FCSTD DOCUMENT  (FreeCAD 1.0R39285 (Git))
Label: pillarAssy_16.5m
License: All rights reserved
LicenseURL: https://en.wikipedia.org/wiki/All_rights_reserved
objects: Part::FeaturePython×104, Sketcher::SketchObject×88, Part::Extrusion×72, App::Part×38, Part::Cut×32, Part::Compound×21, Part::Mirroring×20, Part::Revolution×15, Spreadsheet::Sheet×13, Part::Feature×10, Part::Sweep×8, Part::MultiFuse×6, App::FeaturePython×6, Part::Cylinder×5, PartDesign::Pad×3, Part::Chamfer×2, Part::Loft×1, Assembly::JointGroup×1, Assembly::AssemblyObject×1, Part::Part2DObjectPython×1, +4 more types
note: 460 computed .brp shape members not serialized (recipe doc carries the construction recipe); baked Part::Feature solids carry a one-line shape summary decoded from their .brp

FEATURE [Sketcher::SketchObject] Sketch010
  ArcFitTolerance = 1e-06
  FullyConstrained = false
  MakeInternals = false
  Placement = pos=(0,0,0) rot=(1,0,0;1.5708rad)
  expr: Constraints[4] = Spreadsheet011.dia / 2 + 750
  sketch-geometry (3):
    g0: LineSegment StartX=-1399.77 StartY=148.205 StartZ=0 EndX=-2300 EndY=493.773 EndZ=0
    g1: LineSegment StartX=-2300 StartY=493.773 StartZ=0 EndX=-7732.99 EndY=1036.06 EndZ=0
    g2: LineSegment StartX=-7732.99 StartY=1036.06 StartZ=0 EndX=-9000 EndY=1036.06 EndZ=0
  constraints (7):
    c: Coincident(g0,g1)
    c: Coincident(g1,g2)
    c: Horizontal(g2)
    c: DistanceX(g0,g-1) = 2300
    c: DistanceX(g2,g-1) = 9000
    c: Angle(g0,g-1) = 0.366519
    c: Angle(g1,g-1) = 0.0994838
FEATURE [Sketcher::SketchObject] Sketch011
  ArcFitTolerance = 1e-06
  FullyConstrained = false
  MakeInternals = false
  Placement = pos=(-8500,0,0) rot=(0.57735,0.57735,0.57735;2.0944rad)
  sketch-geometry (1):
    g0: Circle CenterX=0.547565 CenterY=1032.56 CenterZ=0 NormalX=0 NormalY=0 NormalZ=1 AngleXU=0 Radius=108
  constraints (1):
    c: Diameter(g0) = 216
FEATURE [Part::Sweep] Sweep
  Frenet = true
  Sections = -> [Sketch011]
  Solid = true
  Spine = -> Sketch010 [Edge3,Edge2,Edge1]
  Transition = 1
FEATURE [Sketcher::SketchObject] Sketch012
  ArcFitTolerance = 1e-06
  AttachmentSupport = -> [Sweep]
  ExternalGeometry = -> [Sweep]
  FullyConstrained = true
  MakeInternals = false
  MapMode = 5
  Placement = pos=(-9000,0,0) rot=(0.57735,-0.57735,-0.57735;2.0944rad)
  sketch-geometry (1):
    g0: Circle CenterX=-0.547565 CenterY=1032.56 CenterZ=0 NormalX=0 NormalY=0 NormalZ=1 AngleXU=0 Radius=102
  constraints (2):
    c: Diameter(g0) = 204
    c: Coincident(g-3,g0)
FEATURE [Part::Sweep] Sweep001
  Frenet = true
  Sections = -> [Sketch012]
  Solid = true
  Spine = -> Sketch010 [Edge3,Edge2,Edge1]
  Transition = 1
FEATURE [Part::Cut] Cut004  label="Cut005"
  Base = -> Sweep
  Tool = -> Sweep001
FEATURE [Sketcher::SketchObject] Sketch003
  ArcFitTolerance = 1e-06
  FullyConstrained = false
  MakeInternals = false
  Placement = pos=(0,0,0) rot=(1,0,0;1.5708rad)
  sketch-geometry (4):
    g0: LineSegment StartX=-1564.35 StartY=456.2 StartZ=0 EndX=-1449.55 EndY=4.38241 EndZ=0
    g1: LineSegment StartX=-1449.55 StartY=4.38241 StartZ=0 EndX=-942.176 EndY=4.38241 EndZ=0
    g2: LineSegment StartX=-942.176 StartY=4.38241 StartZ=0 EndX=-834.777 EndY=456.2 EndZ=0
    g3: LineSegment StartX=-834.777 StartY=456.2 StartZ=0 EndX=-1564.35 EndY=456.2 EndZ=0
  constraints (6):
    c: Coincident(g0,g1)
    c: Horizontal(g1)
    c: Coincident(g1,g2)
    c: Coincident(g2,g3)
    c: Coincident(g3,g0)
    c: Horizontal(g3)
FEATURE [Part::Revolution] Revolve001
  Angle = 360
  Axis = (0,0,1)
  Base = (0,0,0)
  FaceMakerClass = Part::FaceMakerBullseye
  Solid = true
  Source = -> Sketch003
  Symmetric = false
FEATURE [Part::Cut] Cut005  label="Cut006"
  Base = -> Cut004
  Tool = -> Revolve001
FEATURE [Part::FeaturePython] Flange001  # WARN: FeaturePython — macro-defined, semantics opaque (R4)
  Placement = pos=(-9000,0.547565,1032.56) rot=(0,1,0;4.71239rad)
  dia = 4
  fittings = 00_Flange
  material = 0
  standard = 1
  expr: .Placement.Base.x = -Spreadsheet011.dia / 2 - 750
FEATURE [App::Part] Part037  label="sludgePipe"
  Group = -> [Flange001,Sketch012,Sketch003,Sketch011,Sketch010,Revolve001,Cut004,Sweep,Sweep001,Cut005]
  Origin = -> Origin061
  mass = 244.943
FEATURE [Sketcher::SketchObject] Sketch015
  ArcFitTolerance = 0
  FullyConstrained = true
  MakeInternals = false
  Placement = pos=(0,0,0) rot=(1,0,0;1.5708rad)
  expr: Constraints[11] = Spreadsheet001.dia / 2 - 460
  sketch-geometry (4):
    g0: LineSegment StartX=7785 StartY=0 StartZ=0 EndX=7790 EndY=0 EndZ=0
    g1: LineSegment StartX=7790 StartY=0 StartZ=0 EndX=7790 EndY=250 EndZ=0
    g2: LineSegment StartX=7790 StartY=250 StartZ=0 EndX=7785 EndY=250 EndZ=0
    g3: LineSegment StartX=7785 StartY=250 StartZ=0 EndX=7785 EndY=0 EndZ=0
  constraints (12):
    c: Coincident(g0,g1)
    c: Coincident(g1,g2)
    c: Coincident(g2,g3)
    c: Coincident(g3,g0)
    c: Horizontal(g0)
    c: Horizontal(g2)
    c: Vertical(g1)
    c: Vertical(g3)
    c: PointOnObject(g0,g-1)
    c: Distance(g2) = 5
    c: DistanceY(g1,g1) = 250
    c: DistanceX(g-1,g0) = 7790
FEATURE [Part::Revolution] Revolve006
  Angle = 360
  Axis = (0,0,1)
  Base = (0,0,0)
  FaceMakerClass = Part::FaceMakerBullseye
  Solid = true
  Source = -> Sketch015
  Symmetric = false
FEATURE [Sketcher::SketchObject] Sketch016
  ArcFitTolerance = 0
  FullyConstrained = true
  MakeInternals = false
  Placement = pos=(0,0,0) rot=(1,0,0;1.5708rad)
  sketch-geometry (3):
    g0: LineSegment StartX=-70 StartY=250 StartZ=0 EndX=70 EndY=250 EndZ=0
    g1: LineSegment StartX=70 StartY=250 StartZ=0 EndX=0 EndY=180 EndZ=0
    g2: LineSegment StartX=0 StartY=180 StartZ=0 EndX=-70 EndY=250 EndZ=0
  constraints (9):
    c: Horizontal(g0)
    c: Coincident(g0,g1)
    c: PointOnObject(g1,g-2)
    c: Coincident(g1,g2)
    c: Coincident(g2,g0)
    c: Angle(g1,g2) = 1.5708
    c: PointOnObject(g0,g-3)
    c: DistanceY(g1,g0) = 70
    c: Angle(g2,g-2) = 2.35619
FEATURE [Part::Extrusion] Extrude010
  Base = -> Sketch016
  Dir = (0,-1,2e-16)
  DirMode = 2
  FaceMakerClass = Part::FaceMakerBullseye
  FaceMakerMode = 3
  LengthFwd = 10000
  LengthRev = 0
  Solid = true
  Symmetric = false
FEATURE [Part::FeaturePython] Array006  # Draft array (typed FeaturePython)
  AlwaysSyncPlacement = false
  Angle = 360
  ArrayType = 1
  Axis = (0,0,1)
  Base = -> Extrude010
  Center = (0,0,0)
  Count = 300
  ExpandArray = false
  Fuse = false
  IntervalAxis = (0,0,0)
  IntervalX = (50,0,0)
  IntervalY = (0,50,0)
  IntervalZ = (0,0,50)
  NumberCircles = 3
  NumberPolar = 300
  NumberX = 2
  NumberY = 2
  NumberZ = 1
  PlacementList = 300 placements: [(0,0,0),(0,0,0),(0,0,0),(0,0,0),(0,0,0),(0,0,0),(0,0,0),(0,0,0),(0,0,0),(0,0,0),(0,0,0),(0,0,0),(0,0,0),(0,0,0),(0,0,0),(0,0,0),(0,0,0),(0,0,0),(0,0,0),(0,0,0),(0,0,0),(0,0,0),(0,0,0),(0,0,0),(0,0,0),(0,0,0),(0,0,0),(0,0,0),(0,0,0),(0,0,0),(0,0,0),(0,0,0),(0,0,0),(0,0,0),(0,0,0),(0,0,0),(0,0,0),(0,0,0),(0,0,0),(0,0,0),(0,0,0),(0,0,0),(0,0,0),(0,0,0),(0,0,0),(0,0,0),(0,0,0),(0,0,0),(0,0,0),(0,0,0),+250 more]
  RadialDistance = 50
  Symmetry = 1
  TangentialDistance = 25
  expr: NumberPolar = Spreadsheet001.dia / 55
FEATURE [Part::Cut] Cut007  label="weir"
  Base = -> Revolve006
  Placement = pos=(0,0,4730.4) rot=(0,0,1;0rad)
  Tool = -> Array006
FEATURE [Sketcher::SketchObject] Sketch017
  ArcFitTolerance = 0
  FullyConstrained = true
  MakeInternals = false
  Placement = pos=(0,0,0) rot=(1,0,0;1.5708rad)
  expr: .Constraints.h0 = Spreadsheet001.h0
  expr: Constraints[11] = Spreadsheet001.dia / 2 - (450 + 300)
  sketch-geometry (4):
    g0: LineSegment StartX=7495 StartY=80 StartZ=0 EndX=7500 EndY=80 EndZ=0
    g1: LineSegment StartX=7500 StartY=80 StartZ=0 EndX=7500 EndY=380 EndZ=0
    g2: LineSegment StartX=7500 StartY=380 StartZ=0 EndX=7495 EndY=380 EndZ=0
    g3: LineSegment StartX=7495 StartY=380 StartZ=0 EndX=7495 EndY=80 EndZ=0
  constraints (12):
    c: Coincident(g0,g1)
    c: Coincident(g1,g2)
    c: Coincident(g2,g3)
    c: Coincident(g3,g0)
    c: Horizontal(g0)
    c: Horizontal(g2)
    c: Vertical(g1)
    c: Vertical(g3)
    c: DistanceX(g2,g2) = 5
    c: DistanceY(g1,g1) = 300  'h0'
    c: DistanceY(g-3,g1) = 130
    c: Distance(g1,g-2) = 7500
FEATURE [Part::Revolution] Revolve007
  Angle = 360
  Axis = (0,0,1)
  Base = (0,0,0)
  FaceMakerClass = Part::FaceMakerBullseye
  Solid = true
  Source = -> Sketch017
  Symmetric = false
FEATURE [Part::FeaturePython] AngleSteel  # WARN: FeaturePython — macro-defined, semantics opaque (R4)
  A = 50
  B = 50
  L = 1000
  Placement = pos=(7500,0,474) rot=(0,1,0;1.5708rad)
  Solid = false
  g0 = 7.85
  mass = 0
  size = 7
  standard = SS_Equal
  t = 6
  expr: .Placement.Base.x = Spreadsheet001.dia / 2 - 750
FEATURE [Part::Revolution] Revolve008  label="Revolve002"
  Angle = 360
  Axis = (0,0,1)
  Base = (0,0,0)
  FaceMakerClass = Part::FaceMakerBullseye
  Placement = pos=(0,0,-94) rot=(0,0,1;0rad)
  Solid = false
  Source = -> AngleSteel
  Symmetric = false
FEATURE [Sketcher::SketchObject] Sketch018
  ArcFitTolerance = 0
  FullyConstrained = true
  MakeInternals = false
  Placement = pos=(0,0,0) rot=(1,0,0;1.5708rad)
  expr: Constraints[10] = Spreadsheet001.dia / 2 - (460 + 290)
  sketch-geometry (4):
    g0: LineSegment StartX=7500 StartY=80 StartZ=0 EndX=7790 EndY=-163.339 EndZ=0
    g1: LineSegment StartX=7790 StartY=-163.339 StartZ=0 EndX=7790 EndY=-6.69002 EndZ=0
    g2: LineSegment StartX=7790 StartY=-6.69002 StartZ=0 EndX=7500 EndY=236.649 EndZ=0
    g3: LineSegment StartX=7500 StartY=236.649 StartZ=0 EndX=7500 EndY=80 EndZ=0
  constraints (12):
    c: Coincident(g0,g1)
    c: Vertical(g1)
    c: Coincident(g1,g2)
    c: Coincident(g2,g3)
    c: Coincident(g3,g0)
    c: Vertical(g3)
    c: Parallel(g2,g0)
    c: DistanceX(g0,g0) = 290
    c: Distance(g1,g0) = 120
    c: Angle(g0,g3) = 2.26893
    c: Distance(g0,g-2) = 7500
    c: Distance(g0,g-1) = 80
FEATURE [Part::Extrusion] Extrude011
  Base = -> Sketch018
  Dir = (0,-1,2e-16)
  DirMode = 2
  FaceMakerClass = Part::FaceMakerBullseye
  FaceMakerMode = 3
  LengthFwd = 6
  LengthRev = 0
  Solid = true
  Symmetric = true
FEATURE [Spreadsheet::Sheet] Spreadsheet001  label="Spreadsheet"
  cells = A3='tankDia dia; B3(dia)=16500; A4='waterWay width; B4(W0)=450; A5='nonber of support; B5(n)=12; A6='buffleHight  h0; B6(h0)=300
FEATURE [Part::FeaturePython] AngleSteel001  # WARN: FeaturePython — macro-defined, semantics opaque (R4)
  A = 50
  B = 50
  L = 140
  Placement = pos=(7765,28,-150) rot=(0,0,1;3.14159rad)
  Solid = true
  g0 = 7.85
  mass = 0.620249
  size = 7
  standard = SS_Equal
  t = 6
  expr: .Placement.Base.x = Spreadsheet001.dia / 2 - 485
FEATURE [Part::Mirroring] Mirror  label="AngleSteel001 (mirrored)"
  Base = (4800,0,0)
  Normal = (0,-1,0)
  Source = -> AngleSteel001
FEATURE [Part::Compound] Compound041  label="support"
  Links = -> [AngleSteel001,Mirror,Extrude011]
FEATURE [Part::FeaturePython] Array001  # Draft array (typed FeaturePython)
  AlwaysSyncPlacement = false
  Angle = 360
  ArrayType = 1
  Axis = (0,0,1)
  Base = -> Compound041
  Center = (0,0,0)
  Count = 12
  ExpandArray = false
  Fuse = false
  IntervalAxis = (0,0,0)
  IntervalX = (50,0,0)
  IntervalY = (0,50,0)
  IntervalZ = (0,0,50)
  NumberCircles = 3
  NumberPolar = 12
  NumberX = 2
  NumberY = 2
  NumberZ = 1
  PlacementList = 12 placements: [(0,0,0),(0,0,0),(0,0,0),(0,0,0),(0,0,0),(0,0,0),(0,0,0),(0,0,0),(0,0,0),(0,0,0),(0,0,0),(0,0,0)]
  RadialDistance = 50
  ScaleList = (12) [(1,1,1),(1,1,1),(1,1,1),(1,1,1),(1,1,1),(1,1,1),(1,1,1),(1,1,1),(1,1,1),(1,1,1),(1,1,1),(1,1,1)]
  Symmetry = 1
  TangentialDistance = 25
  expr: NumberPolar = Spreadsheet001.n
FEATURE [Part::Compound] Compound042  label="buffle001"
  Links = -> [Revolve007,Revolve008]
  Placement = pos=(0,0,-20) rot=(0,0,1;0rad)
FEATURE [App::Part] Part038  label="buffle"
  Group = -> [Spreadsheet001,Revolve007,Sketch017,Sketch018,Sketch016,Extrude011,Extrude010,AngleSteel,Revolve008,AngleSteel001,Mirror,Compound041,Array001,Compound042]
  Origin = -> Origin062
  Placement = pos=(0,0,4689) rot=(0,0,1;0rad)
  mass = 804.437
FEATURE [Sketcher::SketchObject] Sketch019
  ArcFitTolerance = 0
  FullyConstrained = true
  MakeInternals = false
  Placement = pos=(0,0,0) rot=(1,0,0;1.5708rad)
  expr: .Constraints.r1 = Spreadsheet002.dia / 2 + 144
  expr: Constraints[20] = Spreadsheet002.dia / 2
  expr: Constraints[21] = .Constraints.r1
  expr: Constraints[22] = Spreadsheet002.l2
  sketch-geometry (8):
    g0: LineSegment StartX=569 StartY=0 StartZ=0 EndX=569 EndY=30 EndZ=0
    g1: LineSegment StartX=569 StartY=30 StartZ=0 EndX=425 EndY=30 EndZ=0
    g2: LineSegment StartX=415 StartY=0 StartZ=0 EndX=415 EndY=3101 EndZ=0
    g3: LineSegment StartX=415 StartY=3101 StartZ=0 EndX=569 EndY=3101 EndZ=0
    g4: LineSegment StartX=569 StartY=3101 StartZ=0 EndX=569 EndY=3071 EndZ=0
    g5: LineSegment StartX=569 StartY=3071 StartZ=0 EndX=425 EndY=3071 EndZ=0
    g6: LineSegment StartX=425 StartY=3071 StartZ=0 EndX=425 EndY=30 EndZ=0
    g7: LineSegment StartX=569 StartY=0 StartZ=0 EndX=415 EndY=0 EndZ=0
  constraints (24):
    c: Vertical(g0)
    c: Coincident(g0,g1)
    c: Horizontal(g1)
    c: Vertical(g2)
    c: Coincident(g2,g3)
    c: Horizontal(g3)
    c: Coincident(g3,g4)
    c: Vertical(g4)
    c: Coincident(g4,g5)
    c: Horizontal(g5)
    c: Coincident(g5,g6)
    c: Vertical(g6)
    c: Coincident(g0,g7)
    c: Horizontal(g7)
    c: Coincident(g1,g6)
    c: DistanceX(g-1,g0) = 569  'r1'
    c: DistanceY(g0,g0) = 30
    c: PointOnObject(g0,g-1)
    c: Coincident(g2,g7)
    c: DistanceX(g2,g1) = 10
    c: DistanceX(g-1,g1) = 425
    c: DistanceX(g-2,g3) = 569
    c: DistanceY(g-1,g3) = 3101
    c: DistanceY(g4,g4) = 30
FEATURE [Part::Revolution] Revolve009  label="bottom"
  Angle = 360
  Axis = (0,0,1)
  Base = (0,0,0)
  FaceMakerClass = Part::FaceMakerBullseye
  Solid = true
  Source = -> Sketch019
  Symmetric = false
FEATURE [Sketcher::SketchObject] Sketch020
  ArcFitTolerance = 0
  FullyConstrained = true
  MakeInternals = false
  Placement = pos=(0,0,0) rot=(1,0,0;1.5708rad)
  sketch-geometry (4):
    g0: LineSegment StartX=315 StartY=0 StartZ=0 EndX=415 EndY=0 EndZ=0
    g1: LineSegment StartX=415 StartY=0 StartZ=0 EndX=415 EndY=2950 EndZ=0
    g2: LineSegment StartX=415 StartY=2950 StartZ=0 EndX=315 EndY=2950 EndZ=0
    g3: LineSegment StartX=315 StartY=2950 StartZ=0 EndX=315 EndY=0 EndZ=0
  constraints (11):
    c: Coincident(g0,g1)
    c: Coincident(g1,g2)
    c: Coincident(g2,g3)
    c: Coincident(g3,g0)
    c: Horizontal(g0)
    c: Horizontal(g2)
    c: Vertical(g1)
    c: Vertical(g3)
    c: Distance(g0) = 100
    c: Coincident(g0,g-3)
    c: PointOnObject(g2,g-4)
FEATURE [Part::Revolution] Revolve010  label="covering"
  Angle = 360
  Axis = (0,0,1)
  Base = (0,0,0)
  FaceMakerClass = Part::FaceMakerBullseye
  Placement = pos=(0,0,936.6) rot=(0,0,1;0rad)
  Solid = true
  Source = -> Sketch020
  Symmetric = false
  mass = 1420.74
FEATURE [Sketcher::SketchObject] Sketch021
  ArcFitTolerance = 0
  FullyConstrained = true
  MakeInternals = false
  Placement = pos=(0,0,0) rot=(1,0,0;1.5708rad)
  expr: Constraints[8] = Spreadsheet002.t0
  expr: Constraints[9] = Spreadsheet002.l2
  sketch-geometry (4):
    g0: LineSegment StartX=415 StartY=3101 StartZ=0 EndX=569 EndY=3101 EndZ=0
    g1: LineSegment StartX=569 StartY=3101 StartZ=0 EndX=569 EndY=3106 EndZ=0
    g2: LineSegment StartX=569 StartY=3106 StartZ=0 EndX=415 EndY=3106 EndZ=0
    g3: LineSegment StartX=415 StartY=3106 StartZ=0 EndX=415 EndY=3101 EndZ=0
  constraints (12):
    c: Coincident(g0,g1)
    c: Coincident(g1,g2)
    c: Coincident(g2,g3)
    c: Coincident(g3,g0)
    c: Horizontal(g0)
    c: Horizontal(g2)
    c: Vertical(g1)
    c: Vertical(g3)
    c: DistanceY(g1,g1) = 5
    c: DistanceY(g-1,g0) = 3101
    c: PointOnObject(g0,g-3)
    c: PointOnObject(g-4,g1)
FEATURE [Part::Revolution] Revolve002  label="gasket"
  Angle = 360
  Axis = (0,0,1)
  Base = (0,0,0)
  FaceMakerClass = Part::FaceMakerBullseye
  Placement = pos=(0,0,1.3656e-08) rot=(0,0,1;0rad)
  Solid = true
  Source = -> Sketch021
  Symmetric = false
FEATURE [Sketcher::SketchObject] Sketch022
  ArcFitTolerance = 0
  FullyConstrained = true
  MakeInternals = false
  Placement = pos=(0,0,0) rot=(1,0,0;1.5708rad)
  expr: Constraints[12] = Spreadsheet002.l1
  sketch-geometry (6):
    g0: LineSegment StartX=569 StartY=2985 StartZ=0 EndX=425 EndY=2985 EndZ=0
    g1: LineSegment StartX=425 StartY=2985 StartZ=0 EndX=425 EndY=4405 EndZ=0
    g2: LineSegment StartX=415 StartY=4405 StartZ=0 EndX=415 EndY=2955 EndZ=0
    g3: LineSegment StartX=415 StartY=2955 StartZ=0 EndX=569 EndY=2955 EndZ=0
    g4: LineSegment StartX=569 StartY=2955 StartZ=0 EndX=569 EndY=2985 EndZ=0
    g5: LineSegment StartX=425 StartY=4405 StartZ=0 EndX=415 EndY=4405 EndZ=0
  constraints (17):
    c: Coincident(g0,g1)
    c: Vertical(g1)
    c: Vertical(g2)
    c: Coincident(g2,g3)
    c: Horizontal(g3)
    c: Coincident(g3,g4)
    c: Coincident(g4,g0)
    c: Vertical(g4)
    c: DistanceY(g4,g4) = 30
    c: Coincident(g3,g-3)
    c: DistanceX(g2,g0) = 10
    c: PointOnObject(g2,g-4)
    c: DistanceY(g3,g1) = 1450
    c: Coincident(g5,g1)
    c: Horizontal(g5)
    c: Coincident(g2,g5)
    c: Horizontal(g0)
FEATURE [Part::Revolution] Revolve003  label="top"
  Angle = 360
  Axis = (0,0,1)
  Base = (0,0,0)
  FaceMakerClass = Part::FaceMakerBullseye
  Solid = true
  Source = -> Sketch022
  Symmetric = false
FEATURE [Sketcher::SketchObject] Sketch023
  ArcFitTolerance = 0
  FullyConstrained = true
  MakeInternals = false
  Placement = pos=(0,0,0) rot=(1,0,0;1.5708rad)
  sketch-geometry (12):
    g0: LineSegment StartX=200 StartY=-1.8e-15 StartZ=0 EndX=406 EndY=-1.8e-15 EndZ=0
    g1: LineSegment StartX=406 StartY=-1.8e-15 StartZ=0 EndX=406 EndY=25 EndZ=0
    g2: LineSegment StartX=406 StartY=25 StartZ=0 EndX=200 EndY=25 EndZ=0
    g3: LineSegment StartX=0 StartY=175 StartZ=0 EndX=350 EndY=175 EndZ=0
    g4: LineSegment StartX=350 StartY=175 StartZ=0 EndX=350 EndY=200 EndZ=0
    g5: LineSegment StartX=350 StartY=200 StartZ=0 EndX=0 EndY=200 EndZ=0
    g6: LineSegment StartX=0 StartY=200 StartZ=0 EndX=0 EndY=175 EndZ=0
    g7: LineSegment StartX=242 StartY=25 StartZ=0 EndX=254 EndY=25 EndZ=0
    g8: LineSegment StartX=254 StartY=25 StartZ=0 EndX=254 EndY=175 EndZ=0
    g9: LineSegment StartX=254 StartY=175 StartZ=0 EndX=242 EndY=175 EndZ=0
    g10: LineSegment StartX=242 StartY=175 StartZ=0 EndX=242 EndY=25 EndZ=0
    g11: LineSegment StartX=200 StartY=25 StartZ=0 EndX=200 EndY=-3.6e-15 EndZ=0
  constraints (36):
    c: Coincident(g0,g1)
    c: Coincident(g1,g2)
    c: Horizontal(g0)
    c: Horizontal(g2)
    c: Vertical(g1)
    c: DistanceY(g1,g1) = 25
    c: DistanceX(g-1,g0) = 406
    c: Coincident(g3,g4)
    c: Coincident(g4,g5)
    c: Coincident(g5,g6)
    c: Coincident(g6,g3)
    c: Horizontal(g3)
    c: Horizontal(g5)
    c: Vertical(g4)
    c: Vertical(g6)
    c: PointOnObject(g3,g-2)
    c: DistanceY(g4,g4) = 25
    c: DistanceX(g5,g5) = 350
    c: DistanceY(g0,g4) = 200
    c: Coincident(g7,g8)
    c: Coincident(g8,g9)
    c: Coincident(g9,g10)
    c: Coincident(g10,g7)
    c: Horizontal(g7)
    c: Horizontal(g9)
    c: Vertical(g8)
    c: Vertical(g10)
    c: PointOnObject(g7,g2)
    c: PointOnObject(g8,g3)
    c: DistanceX(g9,g8) = 12
    c: Vertical(g11)
    c: Coincident(g2,g11)
    c: Coincident(g0,g11)
    c: DistanceX(g-1,g0) = 200
    c: DistanceX(g-2,g7) = 254
    c: PointOnObject(g0,g-1)
FEATURE [Part::Revolution] Revolve004
  Angle = 360
  Axis = (0,0,1)
  Base = (0,0,0)
  FaceMakerClass = Part::FaceMakerBullseye
  Solid = true
  Source = -> Sketch023
  Symmetric = false
FEATURE [Sketcher::SketchObject] Sketch024
  ArcFitTolerance = 0
  AttachmentSupport = -> [Revolve004]
  FullyConstrained = true
  MakeInternals = false
  MapMode = 5
  Placement = pos=(0,0,200) rot=(0,0,1;0rad)
  sketch-geometry (1):
    g0: Circle CenterX=0 CenterY=0 CenterZ=0 NormalX=0 NormalY=0 NormalZ=1 AngleXU=0 Radius=25
  constraints (2):
    c: Coincident(g0,g-1)
    c: Radius(g0) = 25
FEATURE [Part::Extrusion] Extrude012
  Base = -> Sketch024
  Dir = (0,0,1)
  DirMode = 2
  FaceMakerClass = Part::FaceMakerBullseye
  FaceMakerMode = 3
  LengthFwd = 25
  LengthRev = 0
  Reversed = true
  Solid = true
  Symmetric = false
FEATURE [Part::Cut] Cut008
  Base = -> Revolve004
  Tool = -> Extrude012
FEATURE [Sketcher::SketchObject] Sketch025
  ArcFitTolerance = 0
  AttachmentSupport = -> [Cut008]
  FullyConstrained = true
  MakeInternals = false
  MapMode = 5
  Placement = pos=(0,0,200) rot=(0,0,1;0rad)
  sketch-geometry (2):
    g0: Circle CenterX=277.164 CenterY=114.805 CenterZ=0 NormalX=0 NormalY=0 NormalZ=1 AngleXU=0 Radius=14
    g1: LineSegment [constr] StartX=0 StartY=0 StartZ=0 EndX=277.164 EndY=114.805 EndZ=0
  constraints (5):
    c: Coincident(g1,g-1)
    c: Coincident(g1,g0)
    c: Angle(g-1,g1) = 0.392699
    c: Distance(g1) = 300
    c: Radius(g0) = 14
FEATURE [Part::Extrusion] Extrude003
  Base = -> Sketch025
  Dir = (0,0,1)
  DirMode = 2
  FaceMakerClass = Part::FaceMakerBullseye
  FaceMakerMode = 3
  LengthFwd = 25
  LengthRev = 0
  Reversed = true
  Solid = true
  Symmetric = false
FEATURE [Part::FeaturePython] Array002  # Draft array (typed FeaturePython)
  AlwaysSyncPlacement = false
  Angle = 360
  ArrayType = 1
  Axis = (0,0,1)
  Base = -> Extrude003
  Center = (0,0,0)
  Count = 8
  ExpandArray = false
  Fuse = false
  IntervalAxis = (0,0,0)
  IntervalX = (50,0,0)
  IntervalY = (0,50,0)
  IntervalZ = (0,0,50)
  NumberCircles = 3
  NumberPolar = 8
  NumberX = 2
  NumberY = 2
  NumberZ = 1
  PlacementList = 8 placements: [(0,0,0),(0,0,0),(0,0,0),(0,0,0),(0,0,0),(0,0,0),(0,0,0),(0,0,0)]
  RadialDistance = 50
  ScaleList = (8) [(1,1,1),(1,1,1),(1,1,1),(1,1,1),(1,1,1),(1,1,1),(1,1,1),(1,1,1)]
  Symmetry = 1
  TangentialDistance = 25
FEATURE [Sketcher::SketchObject] Sketch026
  ArcFitTolerance = 0
  AttachmentSupport = -> [Revolve009]
  FullyConstrained = true
  MakeInternals = false
  MapMode = 5
  Placement = pos=(0,0,0) rot=(1,0,0;3.14159rad)
  sketch-geometry (2):
    g0: LineSegment [constr] StartX=0 StartY=0 StartZ=0 EndX=461.94 EndY=191.342 EndZ=0
    g1: Circle CenterX=461.94 CenterY=191.342 CenterZ=0 NormalX=0 NormalY=0 NormalZ=1 AngleXU=0 Radius=17.5
  constraints (5):
    c: Coincident(g0,g-1)
    c: Coincident(g1,g0)
    c: Radius(g1) = 17.5
    c: Distance(g0) = 500
    c: Angle(g-1,g0) = 0.392699
FEATURE [Part::Extrusion] Extrude013
  Base = -> Sketch026
  Dir = (0,0,-1)
  DirMode = 2
  FaceMakerClass = Part::FaceMakerBullseye
  FaceMakerMode = 3
  LengthFwd = 3000
  LengthRev = 0
  Reversed = true
  Solid = true
  Symmetric = false
FEATURE [Part::FeaturePython] Array003  # Draft array (typed FeaturePython)
  AlwaysSyncPlacement = false
  Angle = 360
  ArrayType = 1
  Axis = (0,0,1)
  Base = -> Extrude013
  Center = (0,0,0)
  Count = 8
  ExpandArray = false
  Fuse = false
  IntervalAxis = (0,0,0)
  IntervalX = (50,0,0)
  IntervalY = (0,50,0)
  IntervalZ = (0,0,50)
  NumberCircles = 3
  NumberPolar = 8
  NumberX = 2
  NumberY = 2
  NumberZ = 1
  PlacementList = 8 placements: [(0,0,0),(0,0,0),(0,0,0),(0,0,0),(0,0,0),(0,0,0),(0,0,0),(0,0,0)]
  RadialDistance = 50
  ScaleList = (8) [(1,1,1),(1,1,1),(1,1,1),(1,1,1),(1,1,1),(1,1,1),(1,1,1),(1,1,1)]
  Symmetry = 1
  TangentialDistance = 25
FEATURE [Part::Cut] Cut009  label="bottom001"
  Base = -> Revolve009
  Tool = -> Array003
FEATURE [Sketcher::SketchObject] Sketch027
  ArcFitTolerance = 0
  ExternalGeometry = -> [Revolve003]
  FullyConstrained = true
  MakeInternals = false
  Placement = pos=(0,0,0) rot=(1,0,0;1.5708rad)
  expr: Constraints[19] = Spreadsheet002.h0
  sketch-geometry (8):
    g0: LineSegment StartX=-45 StartY=3855 StartZ=0 EndX=45 EndY=3855 EndZ=0
    g1: LineSegment StartX=75 StartY=3885 StartZ=0 EndX=75 EndY=4125 EndZ=0
    g2: LineSegment StartX=45 StartY=4155 StartZ=0 EndX=-45 EndY=4155 EndZ=0
    g3: LineSegment StartX=-75 StartY=4125 StartZ=0 EndX=-75 EndY=3885 EndZ=0
    g4: ArcOfCircle CenterX=45 CenterY=4125 CenterZ=0 NormalX=0 NormalY=0 NormalZ=1 AngleXU=0 Radius=30 StartAngle=-1.07e-14 EndAngle=1.5708
    g5: ArcOfCircle CenterX=-45 CenterY=4125 CenterZ=0 NormalX=0 NormalY=0 NormalZ=1 AngleXU=0 Radius=30 StartAngle=1.5708 EndAngle=3.14159
    g6: ArcOfCircle CenterX=-45 CenterY=3885 CenterZ=0 NormalX=0 NormalY=0 NormalZ=1 AngleXU=0 Radius=30 StartAngle=3.14159 EndAngle=4.71239
    g7: ArcOfCircle CenterX=45 CenterY=3885 CenterZ=0 NormalX=0 NormalY=0 NormalZ=1 AngleXU=0 Radius=30 StartAngle=4.71239 EndAngle=6.28319
  constraints (20):
    c: Horizontal(g0)
    c: Horizontal(g2)
    c: Vertical(g1)
    c: Vertical(g3)
    c: Tangent(g1,g4) = -1.5708
    c: Tangent(g2,g4) = -1.5708
    c: Tangent(g2,g5) = -1.5708
    c: Tangent(g3,g5) = -1.5708
    c: Tangent(g0,g6) = -1.5708
    c: Tangent(g3,g6) = -1.5708
    c: Tangent(g0,g7) = -1.5708
    c: Tangent(g1,g7) = -1.5708
    c: DistanceY(g0,g2) = 300
    c: DistanceX(g3,g1) = 150
    c: DistanceX(g-1,g1) = 75
    c: Radius(g4) = 30
    c: Equal(g4,g5)
    c: Equal(g5,g6)
    c: Equal(g6,g7)
    c: DistanceY(g2,g-3) = 250
FEATURE [Part::Extrusion] Extrude014
  Base = -> Sketch027
  Dir = (0,-1,2e-16)
  DirMode = 2
  FaceMakerClass = Part::FaceMakerBullseye
  FaceMakerMode = 3
  LengthFwd = 500
  LengthRev = 0
  Solid = true
  Symmetric = false
FEATURE [Part::FeaturePython] Array007  # Draft array (typed FeaturePython)
  AlwaysSyncPlacement = false
  Angle = 360
  ArrayType = 1
  Axis = (0,0,1)
  Base = -> Extrude014
  Center = (0,0,0)
  Count = 4
  ExpandArray = false
  Fuse = false
  IntervalAxis = (0,0,0)
  IntervalX = (50,0,0)
  IntervalY = (0,50,0)
  IntervalZ = (0,0,50)
  NumberCircles = 3
  NumberPolar = 4
  NumberX = 2
  NumberY = 2
  NumberZ = 1
  PlacementList = 4 placements: [(0,0,0),(0,0,0),(0,0,0),(0,0,0)]
  RadialDistance = 50
  ScaleList = (4) [(1,1,1),(1,1,1),(1,1,1),(1,1,1)]
  Symmetry = 1
  TangentialDistance = 25
FEATURE [Part::Cut] Cut010  label="Cut009"
  Base = -> Revolve003
  Tool = -> Array007
FEATURE [Sketcher::SketchObject] Sketch028
  ArcFitTolerance = 0
  AttachmentSupport = -> [Cut010]
  FullyConstrained = true
  MakeInternals = false
  MapMode = 5
  Placement = pos=(0,0,2955) rot=(1,0,0;3.14159rad)
  sketch-geometry (2):
    g0: LineSegment [constr] StartX=0 StartY=0 StartZ=0 EndX=461.94 EndY=191.342 EndZ=0
    g1: Circle CenterX=461.94 CenterY=191.342 CenterZ=0 NormalX=0 NormalY=0 NormalZ=1 AngleXU=0 Radius=17.5
  constraints (5):
    c: Coincident(g0,g-1)
    c: Distance(g0) = 500
    c: Coincident(g1,g0)
    c: Radius(g1) = 17.5
    c: Angle(g-1,g0) = 0.392699
FEATURE [Part::Extrusion] Extrude015
  Base = -> Sketch028
  Dir = (0,0,-1)
  DirMode = 2
  FaceMakerClass = Part::FaceMakerBullseye
  FaceMakerMode = 3
  LengthFwd = 30
  LengthRev = 0
  Reversed = true
  Solid = true
  Symmetric = false
FEATURE [Part::Cut] Cut011
  Base = -> Cut010
  Tool = -> Extrude015
FEATURE [Part::FeaturePython] Array004  # Draft array (typed FeaturePython)
  AlwaysSyncPlacement = false
  Angle = 360
  ArrayType = 1
  Axis = (0,0,1)
  Base = -> Extrude015
  Center = (0,0,0)
  Count = 8
  ExpandArray = false
  Fuse = false
  IntervalAxis = (0,0,0)
  IntervalX = (50,0,0)
  IntervalY = (0,50,0)
  IntervalZ = (0,0,50)
  NumberCircles = 3
  NumberPolar = 8
  NumberX = 2
  NumberY = 2
  NumberZ = 1
  PlacementList = 8 placements: [(0,0,0),(0,0,0),(0,0,0),(0,0,0),(0,0,0),(0,0,0),(0,0,0),(0,0,0)]
  RadialDistance = 50
  ScaleList = (8) [(1,1,1),(1,1,1),(1,1,1),(1,1,1),(1,1,1),(1,1,1),(1,1,1),(1,1,1)]
  Symmetry = 1
  TangentialDistance = 25
FEATURE [Part::Cut] Cut012  label="top001"
  Base = -> Cut011
  Placement = pos=(0,0,151) rot=(0,0,1;0rad)
  Tool = -> Array004
  expr: .Placement.Base.z = <<Spreadsheet_centerPost>>.l2 - 2950
FEATURE [Spreadsheet::Sheet] Spreadsheet002  label="Spreadsheet_centerPost"
  cells = A2='top  l1; B2(l1)=1450; A3='bottom  l2; B3(l2)=3101; A4='base l3; B4(l3)=200; A5='gasket  t0; B5(t0)=5; A6='postDia; B6(dia)=850; A7='weirHighr h0; B7(h0)=250
FEATURE [Sketcher::SketchObject] Sketch029
  ArcFitTolerance = 1e-06
  AttachmentSupport = -> [Cut008]
  ExternalGeometry = -> [Cut008]
  FullyConstrained = false
  MakeInternals = false
  MapMode = 5
  Placement = pos=(0,0,25) rot=(0,0,1;0rad)
  sketch-geometry (4):
    g0: LineSegment StartX=-10 StartY=254 StartZ=0 EndX=10 EndY=254 EndZ=0
    g1: LineSegment StartX=10 StartY=254 StartZ=0 EndX=10 EndY=401.198 EndZ=0
    g2: LineSegment StartX=10 StartY=401.198 StartZ=0 EndX=-10 EndY=401.198 EndZ=0
    g3: LineSegment StartX=-10 StartY=401.198 StartZ=0 EndX=-10 EndY=254 EndZ=0
  constraints (10):
    c: Coincident(g0,g1)
    c: Coincident(g1,g2)
    c: Coincident(g2,g3)
    c: Coincident(g3,g0)
    c: Horizontal(g2)
    c: Vertical(g1)
    c: Vertical(g3)
    c: Symmetric(g0,g0,g-2)
    c: Distance(g2,g2) = 20
    c: Tangent(g0,g-3)
FEATURE [Part::Extrusion] Extrude016
  Base = -> Sketch029
  Dir = (0,0,1)
  DirMode = 2
  FaceMakerClass = Part::FaceMakerBullseye
  FaceMakerMode = 3
  LengthFwd = 150
  LengthRev = 0
  Solid = true
  Symmetric = false
FEATURE [Part::Chamfer] Chamfer
  Base = -> Extrude016
  EdgeLinks = -> Extrude016 [Edge10]
  Edges = 1 edges r=50: [Edge10]
FEATURE [Part::FeaturePython] Array005  # Draft array (typed FeaturePython)
  AlwaysSyncPlacement = false
  Angle = 360
  ArrayType = 1
  Axis = (0,0,1)
  Base = -> Chamfer
  Center = (0,0,200)
  Count = 8
  ExpandArray = false
  Fuse = false
  IntervalAxis = (0,0,0)
  IntervalX = (50,0,0)
  IntervalY = (0,50,0)
  IntervalZ = (0,0,50)
  NumberCircles = 3
  NumberPolar = 8
  NumberX = 2
  NumberY = 2
  NumberZ = 1
  PlacementList = 8 placements: [(0,0,0),(0,0,0),(0,0,-5.68434e-14),(0,0,0),(0,0,0),(0,0,0),(0,0,0),(0,0,0)]
  RadialDistance = 50
  ScaleList = (8) [(1,1,1),(1,1,1),(1,1,1),(1,1,1),(1,1,1),(1,1,1),(1,1,1),(1,1,1)]
  Symmetry = 1
  TangentialDistance = 25
FEATURE [App::Part] Part040  label="base"
  Group = -> [Sketch023,Extrude012,Sketch029,Chamfer,Sketch024,Extrude016,Revolve004,Cut008,Array005,Array002]
  Origin = -> Origin064
  Placement = pos=(0,0,4556) rot=(0,0,1;0rad)
  expr: .Placement.Base.z = Spreadsheet002.l1 + Spreadsheet002.l2 + 5
FEATURE [App::Part] Part039  label="centerPost001"
  Group = -> [Extrude003,Sketch025,Cut009,Cut010,Cut011,Extrude013,Revolve002,Revolve003,Revolve009,Extrude014,Extrude015,Array004,Sketch028,Sketch026,Sketch027,Sketch022,Sketch019,Sketch021,Array003,Array007,Cut012,Spreadsheet002,Part040]
  Origin = -> Origin063
  Placement = pos=(1.99e-13,0,799.9) rot=(0,0,1;0rad)
  mass = 1462.82
FEATURE [Spreadsheet::Sheet] Spreadsheet003  label="Spreadsheet_centerCage"
  cells = A2='cage width W0; B2(W0)=1800; A3='cageLength L0; B3(L0)=4736; A4='mainShape mShp; B4(mShp)='100x100x10; A5='mShp gage mg0; B5(mg0)=55; A6='mShp width mb0; B6(mb0)=100; A7='horizontalBeam hShp; B7(hShp)='150x75x9; A8='hShp gage hg; B8(hg)=75; A9='hb0; B9(hb0)=75; A10='lutticeBeam LShp; B10(LShp)='75x75x6; A11='luttice_widht Lb0; B11(Lb0)=75; A12='lutitice length ll; B12(ll)=2286.22434983485; A13='luttice angle sita; B13(sita)=42.1; A14='gusset Gta; B14(Gta)=300; A15='gussetThickness gt; B15(gt)=6; A16='lx; B16(lx)=-763.84930882715; A17='lz; B17(lz)=203.396300643037; A18='Divishon no; B18(n0)=3; A19='DivishonPitch p0; B19(p0)=1528.66666666667; A20='rakeWidth  rw; B20(rw)=750; A22='Angle; D22='Channel; A23='40x40x5; B23=40; C23=17; D23='75x40x5; E23=75; F23=40; G23=17; A24='50x50x5; B24=50; C24=30; D24='100x50x5; E24=100; F24=50; G24=30; A25='65x65x6; B25=65; C25=35; D25='125x65x6; E25=125; F25=65; G25=35; A26='75x75x6; B26=75; C26=40; D26='150x75x9; E26=150; F26=75; G26=40; A27='90x90x7; B27=90; C27=50; D27='180x75x7; E27=180; F27=75; G27=40; A28='100x100x10; B28=100; C28=55; F28=75; G28=40; A29='130x130x12; B29=130
FEATURE [Part::FeaturePython] AngleSteel002  label="mShp"  # WARN: FeaturePython — macro-defined, semantics opaque (R4)
  A = 100
  B = 100
  L = 4736
  Placement = pos=(-850,-850,0) rot=(0,0,1;1.5708rad)
  Solid = true
  g0 = 7.85
  size = 17
  standard = SS_Equal
  t = 7
  expr: .Placement.Base.x = -Spreadsheet003.W0 / 2 + Spreadsheet003.mb0 / 2
  expr: .Placement.Base.y = -Spreadsheet003.W0 / 2 + Spreadsheet003.mb0 / 2
  expr: L = Spreadsheet003.L0
FEATURE [Part::FeaturePython] Array008  # Draft array (typed FeaturePython)
  AlwaysSyncPlacement = false
  Angle = 360
  ArrayType = 1
  Axis = (0,0,1)
  Base = -> AngleSteel002
  Center = (0,0,0)
  Count = 4
  ExpandArray = false
  Fuse = false
  IntervalAxis = (0,0,0)
  IntervalX = (50,0,0)
  IntervalY = (0,50,0)
  IntervalZ = (0,0,50)
  NumberCircles = 3
  NumberPolar = 4
  NumberX = 2
  NumberY = 2
  NumberZ = 1
  PlacementList = 4 placements: [(-850,-850,0),(850,-850,0),(850,850,0),(-850,850,0)]
  RadialDistance = 50
  ScaleList = (4) [(1,1,1),(1,1,1),(1,1,1),(1,1,1)]
  Symmetry = 1
  TangentialDistance = 25
FEATURE [Part::FeaturePython] ChannelSteel  label="hShp"  # WARN: FeaturePython — macro-defined, semantics opaque (R4)
  B = 75
  H = 150
  L = 1600
  Placement = pos=(-800,-862.5,75) rot=(0.57735,0.57735,0.57735;2.0944rad)
  Solid = true
  g0 = 7.85
  size = 4
  standard = SS
  t1 = 6
  t2 = 8
  expr: .Placement.Base.x = -Spreadsheet003.W0 / 2 + Spreadsheet003.mb0
  expr: .Placement.Base.y = -Spreadsheet003.W0 / 2 + Spreadsheet003.hb0 / 2
  expr: .Placement.Base.z = Spreadsheet003.hg
  expr: L = Spreadsheet003.W0 - Spreadsheet003.mb0 * 2
FEATURE [Part::FeaturePython] Array009  label="hBeam"  # Draft array (typed FeaturePython)
  AlwaysSyncPlacement = false
  Angle = 360
  ArrayType = 0
  Axis = (0,0,1)
  Base = -> ChannelSteel
  Center = (0,0,0)
  Count = 4
  ExpandArray = false
  Fuse = false
  IntervalAxis = (0,0,0)
  IntervalX = (100,0,0)
  IntervalY = (0,100,0)
  IntervalZ = (0,0,1528.67)
  NumberCircles = 3
  NumberPolar = 5
  NumberX = 1
  NumberY = 1
  NumberZ = 4
  PlacementList = 4 placements: arithmetic series from (-800,-862.5,75) step (0,0,1528.67) to (-800,-862.5,4661)
  RadialDistance = 50
  ScaleList = (4) [(1,1,1),(1,1,1),(1,1,1),(1,1,1)]
  Symmetry = 1
  TangentialDistance = 25
  expr: .IntervalZ.z = Spreadsheet003.p0
  expr: NumberZ = Spreadsheet003.n0 + 1
FEATURE [Part::FeaturePython] AngleSteel003  label="LShp"  # WARN: FeaturePython — macro-defined, semantics opaque (R4)
  A = 75
  B = 75
  L = 1000
  Placement = pos=(0,0,0) rot=(-1,0,0;1.5708rad)
  Solid = false
  g0 = 7.85
  mass = 0
  size = 10
  standard = SS_Equal
  t = 6
FEATURE [Part::FeaturePython] ChannelSteel001  # WARN: FeaturePython — macro-defined, semantics opaque (R4)
  B = 75
  H = 150
  L = 680
  Placement = pos=(0,0,6e-15) rot=(0.57735,-0.57735,-0.57735;2.0944rad)
  Solid = true
  g0 = 7.85
  size = 4
  standard = SS
  t1 = 6
  t2 = 8
FEATURE [Sketcher::SketchObject] Sketch030
  ArcFitTolerance = 0
  AttachmentSupport = -> [ChannelSteel001]
  ExternalGeometry = -> [ChannelSteel001]
  FullyConstrained = false
  MakeInternals = false
  MapMode = 5
  Placement = pos=(7.5e-14,0,75) rot=(0,0,1;1.5708rad)
  sketch-geometry (3):
    g0: LineSegment StartX=37.5 StartY=0 StartZ=0 EndX=-38.6181 EndY=76.1181 EndZ=0
    g1: LineSegment StartX=-38.6181 StartY=0 StartZ=0 EndX=37.5 EndY=0 EndZ=0
    g2: LineSegment StartX=-38.6181 StartY=0 StartZ=0 EndX=-38.6181 EndY=76.1181 EndZ=0
  constraints (7):
    c: Coincident(g-3,g0)
    c: Coincident(g1,g0)
    c: Coincident(g2,g1)
    c: Coincident(g2,g0)
    c: Vertical(g2)
    c: Horizontal(g1)
    c: Angle(g0,g1) = 0.785398
FEATURE [Part::Extrusion] Extrude017
  Base = -> Sketch030
  Dir = (1.1e-15,0,1)
  DirMode = 2
  FaceMakerClass = Part::FaceMakerBullseye
  FaceMakerMode = 3
  LengthFwd = 150
  LengthRev = 0
  Reversed = true
  Solid = true
  Symmetric = false
FEATURE [Part::Mirroring] Mirror005  label="Extrude006 (mirrored)"
  Base = (-500,32.5,62.5)
  Normal = (-1,9e-16,0)
  Placement = pos=(299.54,0,0) rot=(0,0,1;0rad)
  Source = -> Extrude017
FEATURE [Part::Compound] Compound043  label="Compound003"
  Links = -> [Mirror005,Extrude017]
FEATURE [Part::Cut] Cut013  label="Cut010"
  Base = -> ChannelSteel001
  Placement = pos=(-363,-857,75) rot=(0,0,-1;0.785398rad)
  Tool = -> Compound043
  expr: .Placement.Base.x = -Spreadsheet003.W0 / 2 + 537
  expr: .Placement.Base.y = -Spreadsheet003.W0 / 2 + 43
FEATURE [Sketcher::SketchObject] Sketch031
  ArcFitTolerance = 0
  FullyConstrained = true
  MakeInternals = false
  MapMode = 5
  Placement = pos=(0,0,0) rot=(1,0,0;1.5708rad)
  expr: Constraints[10] = Spreadsheet003.W0 / 2
  expr: Constraints[15] = Spreadsheet003.hg
  expr: Constraints[9] = Spreadsheet003.hg * 2
  sketch-geometry (7):
    g0: LineSegment StartX=900 StartY=0 StartZ=0 EndX=900 EndY=150 EndZ=0
    g1: LineSegment StartX=900 StartY=150 StartZ=0 EndX=930 EndY=150 EndZ=0
    g2: LineSegment StartX=930 StartY=150 StartZ=0 EndX=999.298 EndY=104.199 EndZ=0
    g3: ArcOfCircle CenterX=980 CenterY=75 CenterZ=0 NormalX=0 NormalY=0 NormalZ=1 AngleXU=0 Radius=35 StartAngle=5.29641 EndAngle=7.26996
    g4: LineSegment StartX=999.298 StartY=45.8011 StartZ=0 EndX=930 EndY=0 EndZ=0
    g5: LineSegment StartX=930 StartY=0 StartZ=0 EndX=900 EndY=0 EndZ=0
    g6: Circle CenterX=980 CenterY=75 CenterZ=0 NormalX=0 NormalY=0 NormalZ=1 AngleXU=0 Radius=15
  constraints (19):
    c: Vertical(g0)
    c: Coincident(g0,g1)
    c: Horizontal(g1)
    c: Coincident(g1,g2)
    c: Tangent(g2,g3) = 1.5708
    c: Coincident(g4,g5)
    c: Coincident(g5,g0)
    c: Horizontal(g5)
    c: Coincident(g6,g3)
    c: DistanceY(g0,g0) = 150
    c: DistanceX(g-1,g0) = 900
    c: PointOnObject(g0,g-1)
    c: Vertical(g4,g1)
    c: DistanceX(g0,g3) = 80
    c: Tangent(g3,g4) = 1.5708
    c: DistanceY(g3,g1) = 75
    c: Radius(g6) = 15
    c: Radius(g3) = 35
    c: DistanceX(g0,g4) = 30
FEATURE [PartDesign::Pad] Pad
  Direction = (0,-1,0)
  Length = 48
  Length2 = 10
  Midplane = true
  Placement = pos=(0,0,0) rot=(1,0,0;1.5708rad)
  Profile = -> Sketch031
  ReferenceAxis = -> Sketch031 [N_Axis]
  Suppressed = false
  Type = 0
FEATURE [Sketcher::SketchObject] Sketch032
  ArcFitTolerance = 0
  ExternalGeometry = -> [Pad]
  FullyConstrained = true
  MakeInternals = false
  MapMode = 5
  Placement = pos=(0,0,8.9e-14) rot=(1,0,0;3.14159rad)
  sketch-geometry (4):
    g0: LineSegment StartX=900 StartY=-8 StartZ=0 EndX=1050 EndY=-8 EndZ=0
    g1: LineSegment StartX=1050 StartY=-8 StartZ=0 EndX=1050 EndY=8 EndZ=0
    g2: LineSegment StartX=1050 StartY=8 StartZ=0 EndX=900 EndY=8 EndZ=0
    g3: LineSegment StartX=900 StartY=8 StartZ=0 EndX=900 EndY=-8 EndZ=0
  constraints (12):
    c: Coincident(g0,g1)
    c: Coincident(g1,g2)
    c: Coincident(g2,g3)
    c: Coincident(g3,g0)
    c: Horizontal(g0)
    c: Horizontal(g2)
    c: Vertical(g1)
    c: Vertical(g3)
    c: Distance(g1) = 16
    c: PointOnObject(g2,g-4)
    c: DistanceY(g2,g-4) = 16
    c: DistanceX(g2,g2) = 150
FEATURE [Part::Extrusion] Extrude018
  Base = -> Sketch032
  Dir = (0,0,-1)
  DirMode = 2
  FaceMakerClass = Part::FaceMakerBullseye
  FaceMakerMode = 3
  LengthFwd = 150
  LengthRev = 0
  Reversed = true
  Solid = true
  Symmetric = false
FEATURE [Part::Cut] Cut014
  Base = -> Pad
  Placement = pos=(0,-391,0) rot=(0,0,1;0rad)
  Tool = -> Extrude018
  expr: .Placement.Base.y = -Spreadsheet003.rw / 2 - 16
FEATURE [Part::Mirroring] Mirror006  label="Cut001 (mirrored)"
  Base = (0,0,400)
  Normal = (0,-1,0)
  Source = -> Cut014
FEATURE [Part::Compound] Compound004
  Links = -> [Mirror006,Cut014]
FEATURE [Part::FeaturePython] AngleSteel004  label="LShp001"  # WARN: FeaturePython — macro-defined, semantics opaque (R4)
  A = 75
  B = 75
  L = 2286.22
  Placement = pos=(-850,-932.5,1603.67) rot=(0,1,0;2.30558rad)
  Solid = true
  g0 = 7.85
  size = 10
  standard = SS_Equal
  t = 6
  expr: .Placement.Base.x = -Spreadsheet003.W0 / 2 + Spreadsheet003.mb0 / 2
  expr: .Placement.Base.y = -Spreadsheet003.W0 / 2 - 32.5
  expr: .Placement.Base.z = Spreadsheet003.p0 + Spreadsheet003.hg
  expr: .Placement.Rotation.Angle = Spreadsheet003.sita + 90
  expr: L = Spreadsheet003.ll
FEATURE [Part::FeaturePython] Array010  # Draft array (typed FeaturePython)
  AlwaysSyncPlacement = false
  Angle = 360
  ArrayType = 0
  Axis = (0,0,1)
  Base = -> AngleSteel004
  Center = (0,0,0)
  Count = 3
  ExpandArray = false
  Fuse = false
  IntervalAxis = (0,0,0)
  IntervalX = (100,0,0)
  IntervalY = (0,100,0)
  IntervalZ = (0,0,1528.67)
  NumberCircles = 3
  NumberPolar = 5
  NumberX = 1
  NumberY = 1
  NumberZ = 3
  PlacementList = 3 placements: arithmetic series from (-850,-932.5,1603.67) step (0,0,1528.67) to (-850,-932.5,4661)
  RadialDistance = 50
  ScaleList = (3) [(1,1,1),(1,1,1),(1,1,1)]
  Symmetry = 1
  TangentialDistance = 25
  expr: .IntervalZ.z = Spreadsheet003.p0
  expr: NumberZ = Spreadsheet003.n0
FEATURE [Sketcher::SketchObject] Sketch033
  ArcFitTolerance = 0
  ExternalGeometry = -> [Compound004]
  FullyConstrained = true
  MakeInternals = false
  Placement = pos=(0,0,0) rot=(1,0,0;1.5708rad)
  expr: Constraints[17] = Spreadsheet003.p0
  sketch-geometry (7):
    g0: LineSegment StartX=900 StartY=1541.17 StartZ=0 EndX=900 EndY=1666.17 EndZ=0
    g1: LineSegment StartX=900 StartY=1666.17 StartZ=0 EndX=930 EndY=1666.17 EndZ=0
    g2: LineSegment StartX=930 StartY=1666.17 StartZ=0 EndX=995.018 EndY=1635.28 EndZ=0
    g3: ArcOfCircle CenterX=980 CenterY=1603.67 CenterZ=0 NormalX=0 NormalY=0 NormalZ=1 AngleXU=0 Radius=35 StartAngle=5.15587 EndAngle=7.41051
    g4: LineSegment StartX=995.018 StartY=1572.05 StartZ=0 EndX=930 EndY=1541.17 EndZ=0
    g5: LineSegment StartX=930 StartY=1541.17 StartZ=0 EndX=900 EndY=1541.17 EndZ=0
    g6: Circle CenterX=980 CenterY=1603.67 CenterZ=0 NormalX=0 NormalY=0 NormalZ=1 AngleXU=0 Radius=15
  constraints (19):
    c: Vertical(g0)
    c: Coincident(g0,g1)
    c: Horizontal(g1)
    c: Coincident(g1,g2)
    c: Tangent(g2,g3) = 1.5708
    c: Coincident(g4,g5)
    c: Coincident(g5,g0)
    c: Horizontal(g5)
    c: Coincident(g6,g3)
    c: Radius(g6) = 15
    c: Radius(g3) = 35
    c: DistanceX(g1,g1) = 30
    c: Distance(g3,g0) = 80
    c: Tangent(g3,g4) = 1.5708
    c: Equal(g5,g1)
    c: Equal(g4,g2)
    c: Distance(g0) = 125
    c: DistanceY(g-3,g3) = 1528.67
    c: Vertical(g-3,g3)
FEATURE [Part::Extrusion] Extrude019
  Base = -> Sketch033
  Dir = (0,-1,2e-16)
  DirMode = 2
  FaceMakerClass = Part::FaceMakerBullseye
  FaceMakerMode = 3
  LengthFwd = 16
  LengthRev = 0
  Placement = pos=(0,-391,0) rot=(0,0,1;0rad)
  Solid = true
  Symmetric = true
  expr: .Placement.Base.y = -Spreadsheet003.rw / 2 - 16
FEATURE [Part::Mirroring] Mirror007  label="Extrude (mirrored)"
  Base = (0,0,1500)
  Normal = (0,1,0)
  Source = -> Extrude019
FEATURE [Part::Compound] Compound005
  Links = -> [Mirror007,Extrude019]
FEATURE [Part::Compound] Compound006
  Links = -> [Compound005,Compound004]
FEATURE [Part::Mirroring] Mirror008  label="Compound006 (mirrored)"
  Base = (0,0,-1000)
  Normal = (1,0,0)
  Source = -> Compound006
FEATURE [Part::FeaturePython] ChannelSteel002  # WARN: FeaturePython — macro-defined, semantics opaque (R4)
  B = 75
  H = 150
  L = 1200
  Placement = pos=(500,0,4586) rot=(0,0,1;0rad)
  Solid = false
  g0 = 7.85
  mass = 0
  size = 4
  standard = SS
  t1 = 9
  t2 = 12.5
  expr: .Placement.Base.z = Spreadsheet003.L0 - 150
FEATURE [Part::Extrusion] Extrude020
  Base = -> ChannelSteel002
  Dir = (0,1,0)
  DirMode = 2
  FaceMakerClass = Part::FaceMakerBullseye
  FaceMakerMode = 3
  LengthFwd = 1334
  LengthRev = 0
  Solid = false
  Symmetric = true
FEATURE [Part::Compound] Compound008
FEATURE [Part::Cut] Cut015
  Base = -> Extrude020
  Tool = -> Compound008
FEATURE [Part::FeaturePython] Array011  # Draft array (typed FeaturePython)
  AlwaysSyncPlacement = false
  Angle = 360
  ArrayType = 1
  Axis = (0,0,1)
  Base = -> Cut013
  Center = (0,0,0)
  Count = 4
  ExpandArray = false
  Fuse = false
  IntervalAxis = (0,0,0)
  IntervalX = (50,0,0)
  IntervalY = (0,50,0)
  IntervalZ = (0,0,50)
  NumberCircles = 3
  NumberPolar = 4
  NumberX = 2
  NumberY = 2
  NumberZ = 1
  PlacementList = 4 placements: [(-363,-857,75),(857,-363,75),(363,857,75),(-857,363,75)]
  RadialDistance = 50
  ScaleList = (4) [(1,1,1),(1,1,1),(1,1,1),(1,1,1)]
  Symmetry = 1
  TangentialDistance = 25
FEATURE [Part::FeaturePython] ChannelSteel003  # WARN: FeaturePython — macro-defined, semantics opaque (R4)
  B = 75
  H = 150
  L = 1000
  Placement = pos=(-500,538,4661) rot=(0.57735,0.57735,0.57735;2.0944rad)
  Solid = true
  g0 = 7.85
  size = 4
  standard = SS
  t1 = 9
  t2 = 12.5
  expr: .Placement.Base.z = Spreadsheet003.L0 - Spreadsheet003.hg
FEATURE [Part::FeaturePython] Array012  # Draft array (typed FeaturePython)
  AlwaysSyncPlacement = false
  Angle = 360
  ArrayType = 0
  Axis = (0,0,1)
  Base = -> Array011
  Center = (0,0,0)
  Count = 4
  ExpandArray = false
  Fuse = false
  IntervalAxis = (0,0,0)
  IntervalX = (100,0,0)
  IntervalY = (0,100,0)
  IntervalZ = (0,0,1528.67)
  NumberCircles = 3
  NumberPolar = 5
  NumberX = 1
  NumberY = 1
  NumberZ = 4
  PlacementList = 4 placements: arithmetic series from (0,0,0) step (0,0,1528.67) to (0,0,4586)
  RadialDistance = 50
  ScaleList = (4) [(1,1,1),(1,1,1),(1,1,1),(1,1,1)]
  Symmetry = 1
  TangentialDistance = 25
  expr: .IntervalZ.z = Spreadsheet003.p0
FEATURE [Part::Mirroring] Mirror010  label="ChannelSteel003 (mirrored)"
  Base = (-300,0,0)
  Normal = (0,-1,0)
  Source = -> ChannelSteel003
FEATURE [Part::Feature] Part__Feature005  label="reducer"
  Placement = pos=(0,0,4586) rot=(0,0,1;0rad)
  shape: bbox 1029 x 1029 x 150 mm, 111 faces (baked)
  expr: .Placement.Base.z = Spreadsheet003.L0 - 150
FEATURE [Part::Feature] Part__Feature008  label="Compound017"
  shape: bbox 785.2 x 75 x 709.2 mm, 36 faces (baked)
FEATURE [Part::Feature] Part__Feature009  label="Compound018"
  shape: bbox 75 x 75 x 380 mm, 11 faces (baked)
FEATURE [Part::Compound] Compound044  label="Compound046"
  Links = -> [Array010,Array009]
FEATURE [Part::FeaturePython] Array013  # Draft array (typed FeaturePython)
  AlwaysSyncPlacement = false
  Angle = 360
  ArrayType = 1
  Axis = (0,0,1)
  Base = -> Compound044
  Center = (0,0,0)
  Count = 4
  ExpandArray = false
  Fuse = false
  IntervalAxis = (0,0,0)
  IntervalX = (50,0,0)
  IntervalY = (0,50,0)
  IntervalZ = (0,0,50)
  NumberCircles = 3
  NumberPolar = 4
  NumberX = 2
  NumberY = 2
  NumberZ = 1
  PlacementList = 4 placements: [(0,0,0),(0,0,0),(0,0,0),(0,0,0)]
  RadialDistance = 50
  ScaleList = (4) [(1,1,1),(1,1,1),(1,1,1),(1,1,1)]
  Symmetry = 1
  TangentialDistance = 25
FEATURE [Sketcher::SketchObject] Sketch034
  ArcFitTolerance = 1e-06
  AttachmentSupport = -> [Part__Feature009]
  FullyConstrained = false
  MakeInternals = false
  MapMode = 5
  Placement = pos=(0,0.033,0) rot=(1,0,0;1.5708rad)
  sketch-geometry (4):
    g0: LineSegment StartX=830.796 StartY=-231.462 StartZ=0 EndX=1616.25 EndY=-231.462 EndZ=0
    g1: LineSegment StartX=1616.25 StartY=-231.462 StartZ=0 EndX=1442.06 EndY=-936.829 EndZ=0
    g2: LineSegment StartX=1442.06 StartY=-936.829 StartZ=0 EndX=1006.47 EndY=-936.829 EndZ=0
    g3: LineSegment StartX=1006.47 StartY=-936.829 StartZ=0 EndX=830.796 EndY=-231.462 EndZ=0
  constraints (6):
    c: Horizontal(g0)
    c: Coincident(g0,g1)
    c: Coincident(g1,g2)
    c: Horizontal(g2)
    c: Coincident(g2,g3)
    c: Coincident(g3,g0)
FEATURE [Part::FeaturePython] AngleSteel005  label="AngleSteel003"  # WARN: FeaturePython — macro-defined, semantics opaque (R4)
  A = 75
  B = 75
  L = 5500
  Placement = pos=(1262.5,0,-231.5) rot=(0.57735,-0.57735,-0.57735;4.18879rad)
  Solid = false
  g0 = 7.85
  mass = 0
  size = 10
  standard = SS_Equal
  t = 6
  type = 00_Angle
FEATURE [Part::Sweep] Sweep002
  Frenet = true
  Placement = pos=(-44,0,1178.5) rot=(0,0,1;0rad)
  Sections = -> [AngleSteel005]
  Solid = true
  Spine = -> Sketch034 [Edge1,Edge2,Edge3,Edge4]
  Transition = 1
FEATURE [App::Part] Compound017  label="blade001"
  Group = -> [Part__Feature008,Part__Feature009,AngleSteel005,Sketch034,Sweep002]
  Origin = -> Origin066
  Placement = pos=(23,0,-1177.59) rot=(0,0,1;0rad)
FEATURE [Part::FeaturePython] Array014  # Draft array (typed FeaturePython)
  AlwaysSyncPlacement = false
  Angle = 360
  ArrayType = 1
  Axis = (0,0,1)
  Base = -> Compound017
  Center = (0,0,0)
  Count = 2
  ExpandArray = false
  Fuse = true
  IntervalAxis = (0,0,0)
  IntervalX = (50,0,0)
  IntervalY = (0,50,0)
  IntervalZ = (0,0,50)
  NumberCircles = 3
  NumberPolar = 2
  NumberX = 2
  NumberY = 2
  NumberZ = 1
  PlacementList = 2 placements: [(23,0,-1177.59),(-23,2.81669e-15,-1177.59)]
  RadialDistance = 50
  ScaleList = (2) [(1,1,1),(1,1,1)]
  Symmetry = 1
  TangentialDistance = 25
FEATURE [Part::Mirroring] Mirror011  label="Cut002 (mirrored)"
  Base = (0,0,0)
  Normal = (1,0,0)
  Source = -> Cut015
FEATURE [Part::Compound] Compound045  label="Compound047"
  Links = -> [Array008,AngleSteel003,Mirror008,Array012,Mirror010,Part__Feature005,Array013,Array014,Mirror011]
FEATURE [App::Part] Part041  label="centerCage"
  Group = -> [Spreadsheet003,ChannelSteel,Array009,AngleSteel002,Array008,AngleSteel003,ChannelSteel001,Compound043,Sketch030,Mirror005,Extrude017,Cut013,Sketch031,Pad,Sketch032,Extrude018,Cut014,Mirror006,Compound004,AngleSteel004,Array010,Sketch033,Extrude019,Mirror007,Compound005,Compound006,Mirror008,Compound008,Extrude020,ChannelSteel002,Cut015,ChannelSteel003,Array011,Array012,Mirror010,Compound017,+6 more]
  Origin = -> Origin065
  Placement = pos=(0,0,970) rot=(0,0,1;0rad)
  mass = 1513.41
FEATURE [Sketcher::SketchObject] Sketch035
  ArcFitTolerance = 0
  FullyConstrained = true
  MakeInternals = false
  sketch-geometry (5):
    g0: LineSegment StartX=-640 StartY=-650 StartZ=0 EndX=-640 EndY=650 EndZ=0
    g1: LineSegment StartX=-640 StartY=650 StartZ=0 EndX=640 EndY=650 EndZ=0
    g2: LineSegment StartX=640 StartY=650 StartZ=0 EndX=640 EndY=-650 EndZ=0
    g3: LineSegment StartX=640 StartY=-650 StartZ=0 EndX=-640 EndY=-650 EndZ=0
    g4: GeomPoint [constr] X=0 Y=0 Z=0
  constraints (12):
    c: Coincident(g0,g1)
    c: Coincident(g1,g2)
    c: Coincident(g2,g3)
    c: Coincident(g3,g0)
    c: Horizontal(g1)
    c: Horizontal(g3)
    c: Vertical(g0)
    c: Vertical(g2)
    c: Symmetric(g1,g0,g4)
    c: Coincident(g4,g-1)
    c: DistanceY(g2,g2) = 1300
    c: DistanceX(g1,g1) = 1280
FEATURE [Part::FeaturePython] HShapeSteel002  label="HShapeSteel003"  # WARN: FeaturePython — macro-defined, semantics opaque (R4)
  B = 150
  H = 150
  L = 1000
  Placement = pos=(530,0,-150) rot=(0,0,1;0rad)
  Solid = false
  g0 = 7.85
  mass = 0
  size = 2
  standard = SS_Wide
  t1 = 7
  t2 = 10
FEATURE [Part::Sweep] Sweep006
  Frenet = true
  Sections = -> [HShapeSteel002]
  Solid = true
  Spine = -> Sketch035 [Edge3,Edge2,Edge1,Edge4]
  Transition = 1
FEATURE [Part::FeaturePython] HShapeSteel003  label="HShapeSteel004"  # WARN: FeaturePython — macro-defined, semantics opaque (R4)
  B = 150
  H = 150
  L = 1000
  Placement = pos=(607.98,425,-75) rot=(0.57735,0.57735,0.57735;2.0944rad)
  Solid = true
  g0 = 7.85
  mass = 31.5089
  size = 2
  standard = SS_Wide
  t1 = 7
  t2 = 10
FEATURE [Part::FeaturePython] Clone001  label="HShapeSteel005"  # Draft clone (typed FeaturePython)
  AttacherType = Attacher::AttachEngine3D
  Fuse = false
  Objects = -> [HShapeSteel003]
  Placement = pos=(607.98,-425,-75) rot=(0.57735,0.57735,0.57735;2.0944rad)
  Scale = (1,1,1)
FEATURE [Part::FeaturePython] HShapeSteel004  label="HShapeSteel006"  # WARN: FeaturePython — macro-defined, semantics opaque (R4)
  B = 150
  H = 150
  L = 1000
  Placement = pos=(1607.98,-500,-150) rot=(0,0,1;1.5708rad)
  Solid = false
  g0 = 7.85
  mass = 0
  size = 2
  standard = SS_Wide
  t1 = 7
  t2 = 10
FEATURE [Part::FeaturePython] HShapeSteel005  label="HShapeSteel007"  # WARN: FeaturePython — macro-defined, semantics opaque (R4)
  B = 150
  H = 194
  L = 1000
  Placement = pos=(1900,-500,-194) rot=(0,0,1;1.5708rad)
  Solid = false
  g0 = 7.85
  mass = 0
  size = 1
  standard = SS_Medium
  t1 = 6
  t2 = 9
FEATURE [Part::Loft] Loft
  Closed = false
  MaxDegree = 5
  Ruled = false
  Sections = -> [HShapeSteel004,HShapeSteel005]
  Solid = true
FEATURE [Part::Extrusion] Extrude021
  Base = -> HShapeSteel005
  Dir = (-1,-2e-16,0)
  DirMode = 2
  FaceMakerClass = Part::FaceMakerBullseye
  FaceMakerMode = 3
  LengthFwd = 6600
  LengthRev = 0
  Reversed = true
  Solid = true
  Symmetric = false
  expr: LengthFwd = Spreadsheet004.L0
FEATURE [Part::MultiFuse] Fusion002  label="Fusion"
  Shapes = -> [HShapeSteel003,Clone001]
FEATURE [Part::MultiFuse] Fusion003  label="Fusion002"
  Shapes = -> [Extrude021,Loft]
FEATURE [Part::FeaturePython] Clone002  label="Fusion003"  # Draft clone (typed FeaturePython)
  AttacherType = Attacher::AttachEngine3D
  Fuse = false
  Objects = -> [Fusion003]
  Placement = pos=(-9.09e-13,850,6.6e-14) rot=(0,0,1;0rad)
  Scale = (1,1,1)
FEATURE [Part::Mirroring] Mirror012  label="Fusion (mirrored)"
  Base = (0,0,0)
  Normal = (1,0,0)
  Source = -> Fusion002
FEATURE [Spreadsheet::Sheet] Spreadsheet004  label="Spreadsheet_bridge"
  cells = A2='tankdia   dia; B2(dia)=16500; A3='L0; B3(L0)==dia / 2 - 1650; A4='no of bram n; B4(n)=9; A5='hight; B5(hight)=450
FEATURE [Sketcher::SketchObject] Sketch036
  ArcFitTolerance = 0
  FullyConstrained = true
  MakeInternals = false
  sketch-geometry (4):
    g0: LineSegment StartX=-1150 StartY=-1150 StartZ=0 EndX=-1150 EndY=1150 EndZ=0
    g1: LineSegment StartX=-1150 StartY=1150 StartZ=0 EndX=1150 EndY=1150 EndZ=0
    g2: LineSegment StartX=1150 StartY=1150 StartZ=0 EndX=1150 EndY=-1150 EndZ=0
    g3: LineSegment StartX=-1150 StartY=-1150 StartZ=0 EndX=1150 EndY=-1150 EndZ=0
  constraints (12):
    c: Vertical(g0)
    c: Coincident(g0,g1)
    c: Horizontal(g1)
    c: Coincident(g1,g2)
    c: Vertical(g2)
    c: DistanceX(g1,g1) = 2300
    c: DistanceX(g-2,g1) = 1150
    c: Coincident(g3,g0)
    c: Coincident(g3,g2)
    c: Horizontal(g3)
    c: DistanceY(g2,g2) = 2300
    c: DistanceY(g-1,g1) = 1150
FEATURE [Part::FeaturePython] ChannelSteel005  # WARN: FeaturePython — macro-defined, semantics opaque (R4)
  B = 75
  H = 150
  L = 1000
  Placement = pos=(-1150,855.871,-150) rot=(0,0,1;0rad)
  Solid = false
  g0 = 7.85
  mass = 0
  size = 3
  standard = SS
  t1 = 6.5
  t2 = 10
FEATURE [Part::Sweep] Sweep007
  Frenet = true
  Sections = -> [ChannelSteel005]
  Solid = true
  Spine = -> Sketch036 [Edge2,Edge3,Edge4,Edge1]
  Transition = 1
FEATURE [Part::FeaturePython] AngleSteel007  # WARN: FeaturePython — macro-defined, semantics opaque (R4)
  A = 75
  B = 75
  L = 700
  Placement = pos=(1800,350,-37.5) rot=(1,0,0;1.5708rad)
  Solid = true
  g0 = 7.85
  size = 10
  standard = SS_Equal
  t = 6
FEATURE [Part::FeaturePython] Array017  # Draft array (typed FeaturePython)
  AlwaysSyncPlacement = false
  Angle = 360
  ArrayType = 0
  Axis = (0,0,1)
  Base = -> AngleSteel007
  Center = (0,0,0)
  Count = 9
  ExpandArray = false
  Fuse = false
  IntervalAxis = (0,0,0)
  IntervalX = (700,0,0)
  IntervalY = (0,100,0)
  IntervalZ = (0,0,100)
  NumberCircles = 3
  NumberPolar = 5
  NumberX = 9
  NumberY = 1
  NumberZ = 1
  PlacementList = 9 placements: arithmetic series from (1800,350,-37.5) step (700,0,0) to (7400,350,-37.5)
  RadialDistance = 50
  ScaleList = (9) [(1,1,1),(1,1,1),(1,1,1),(1,1,1),(1,1,1),(1,1,1),(1,1,1),(1,1,1),(1,1,1)]
  Symmetry = 1
  TangentialDistance = 25
  expr: NumberX = Spreadsheet004.n
FEATURE [Part::Compound] Compound046  label="Compound048"
  Links = -> [Fusion003,Clone002]
FEATURE [Part::Compound] Compound047  label="Compound001"
  Links = -> [Compound046,Array017]
FEATURE [Part::FeaturePython] HShapeSteel006  label="HShapeSteel008"  # WARN: FeaturePython — macro-defined, semantics opaque (R4)
  B = 150
  H = 194
  L = 850
  Placement = pos=(8425,425,-97) rot=(1,0,0;1.5708rad)
  Solid = true
  g0 = 7.85
  size = 1
  standard = SS_Medium
  t1 = 6
  t2 = 9
  expr: .Placement.Base.x = Spreadsheet004.dia / 2 + 175
FEATURE [Sketcher::SketchObject] Sketch037
  ArcFitTolerance = 0
  ExternalGeometry = -> [Sketch036]
  FullyConstrained = false
  MakeInternals = false
  MapMode = 5
  Placement = pos=(0,0,1.342e-13) rot=(0,0,1;0rad)
  expr: Constraints[28] = Spreadsheet004.dia / 2 + 250
  sketch-geometry (12):
    g0: LineSegment StartX=0 StartY=1150 StartZ=0 EndX=1150 EndY=1150 EndZ=0
    g1: LineSegment StartX=1150 StartY=1150 StartZ=0 EndX=1150 EndY=500 EndZ=0
    g2: LineSegment StartX=1150 StartY=500 StartZ=0 EndX=8500 EndY=500 EndZ=0
    g3: LineSegment StartX=8500 StartY=-500 StartZ=0 EndX=1150 EndY=-500 EndZ=0
    g4: LineSegment StartX=1150 StartY=-500 StartZ=0 EndX=1150 EndY=-1150 EndZ=0
    g5: LineSegment StartX=1150 StartY=-1150 StartZ=0 EndX=0 EndY=-1150 EndZ=0
    g6: LineSegment StartX=0 StartY=-1150 StartZ=0 EndX=0 EndY=-600 EndZ=0
    g7: LineSegment StartX=0 StartY=600 StartZ=0 EndX=606.738 EndY=600 EndZ=0
    g8: LineSegment StartX=606.738 StartY=600 StartZ=0 EndX=606.738 EndY=-600 EndZ=0
    g9: LineSegment StartX=606.738 StartY=-600 StartZ=0 EndX=0 EndY=-600 EndZ=0
    g10: LineSegment StartX=0 StartY=600 StartZ=0 EndX=0 EndY=1150 EndZ=0
    g11: LineSegment StartX=8500 StartY=-500 StartZ=0 EndX=8500 EndY=500 EndZ=0
  constraints (31):
    c: Horizontal(g0)
    c: Coincident(g0,g1)
    c: Vertical(g1)
    c: Coincident(g1,g2)
    c: Horizontal(g2)
    c: Horizontal(g3)
    c: Coincident(g3,g4)
    c: Coincident(g4,g5)
    c: PointOnObject(g5,g-2)
    c: Horizontal(g5)
    c: Coincident(g5,g6)
    c: Coincident(g10,g0)
    c: Vertical(g6)
    c: Coincident(g-3,g0)
    c: Coincident(g4,g-3)
    c: Vertical(g4)
    c: Horizontal(g7)
    c: Coincident(g7,g8)
    c: Vertical(g8)
    c: Coincident(g8,g9)
    c: Horizontal(g9)
    c: Coincident(g6,g9)
    c: Coincident(g10,g7)
    c: Vertical(g10)
    c: Coincident(g11,g3)
    c: Coincident(g11,g2)
    c: DistanceY(g11,g11) = 1000
    c: Symmetric(g3,g2,g-1)
    c: DistanceX(g-1,g3) = 8500
    c: Symmetric(g6,g7,g-1)
    c: DistanceY(g8,g8) = 1200
FEATURE [Part::Extrusion] Extrude022
  Base = -> Sketch037
  Dir = (0,0,1)
  DirMode = 2
  FaceMakerClass = Part::FaceMakerBullseye
  FaceMakerMode = 3
  LengthFwd = 4.5
  LengthRev = 0
  Solid = true
  Symmetric = false
FEATURE [Part::FeaturePython] BasePlate  # WARN: FeaturePython — macro-defined, semantics opaque (R4)
  B = 150
  D = 20
  H = 150
  b1 = 30
  h1 = 45
  sface = 0
FEATURE [Part::Extrusion] Extrude023
  Base = -> BasePlate
  Dir = (0,0,1)
  DirMode = 2
  FaceMakerClass = Part::FaceMakerBullseye
  FaceMakerMode = 3
  LengthFwd = 10
  LengthRev = 0
  Solid = true
  Symmetric = false
FEATURE [Part::FeaturePython] H_Shape  # WARN: FeaturePython — macro-defined, semantics opaque (R4)
  B = 150
  H = 150
  L = 256
  Solid = true
  g0 = 7.85
  size = 2
  standard = SS_Wide
  expr: L = Spreadsheet004.hight - 194
FEATURE [Part::MultiFuse] Fusion007  label="PostH"
  Placement = pos=(-8425,-425,-450) rot=(0,0,1;1.5708rad)
  Shapes = -> [Extrude023,H_Shape]
  expr: .Placement.Base.x = -Spreadsheet004.dia / 2 - 175
  expr: .Placement.Base.z = -Spreadsheet004.hight
FEATURE [Sketcher::SketchObject] Sketch038
  ArcFitTolerance = 0
  FullyConstrained = false
  MakeInternals = false
  MapMode = 5
  Placement = pos=(0,0,1.342e-13) rot=(0,0,1;0rad)
  expr: Constraints[6] = Spreadsheet004.dia / 2 + 250
  sketch-geometry (3):
    g0: LineSegment StartX=8500 StartY=-425 StartZ=0 EndX=8500 EndY=-925 EndZ=0
    g1: LineSegment StartX=8500 StartY=-925 StartZ=0 EndX=7000 EndY=-925 EndZ=0
    g2: LineSegment StartX=7000 StartY=-925 StartZ=0 EndX=7000 EndY=-428 EndZ=0
  constraints (9):
    c: Vertical(g0)
    c: Coincident(g0,g1)
    c: Horizontal(g1)
    c: Coincident(g1,g2)
    c: Vertical(g2)
    c: DistanceX(g1,g1) = 1500
    c: DistanceX(g-1,g0) = 8500
    c: Distance(g0,g-1) = 425
    c: DistanceY(g0,g0) = 500
FEATURE [Part::FeaturePython] ChannelSteel006  # WARN: FeaturePython — macro-defined, semantics opaque (R4)
  B = 75
  H = 150
  L = 1000
  Placement = pos=(7075,-671.206,-150) rot=(0,0,1;3.14159rad)
  Solid = false
  g0 = 7.85
  mass = 0
  size = 3
  standard = SS
  t1 = 6.5
  t2 = 10
  expr: .Placement.Base.x = Spreadsheet004.dia / 2 - 1175
FEATURE [Part::FeaturePython] Array018  # Draft array (typed FeaturePython)
  AlwaysSyncPlacement = false
  Angle = 360
  ArrayType = 1
  Axis = (0,0,1)
  Base = -> Compound047
  Center = (0,0,0)
  Count = 2
  ExpandArray = false
  Fuse = true
  IntervalAxis = (0,0,0)
  IntervalX = (50,0,0)
  IntervalY = (0,50,0)
  IntervalZ = (0,0,50)
  NumberCircles = 3
  NumberPolar = 2
  NumberX = 2
  NumberY = 2
  NumberZ = 1
  PlacementList = 2 placements: [(0,0,0),(0,0,0)]
  RadialDistance = 50
  ScaleList = (2) [(1,1,1),(1,1,1)]
  Symmetry = 1
  TangentialDistance = 25
FEATURE [Part::FeaturePython] Channel  # WARN: FeaturePython — macro-defined, semantics opaque (R4)
  Placement = pos=(0,-1123.5,5) rot=(0,0,1;0rad)
  Reverse = false
  g0 = 7.85
  h = 1100
  k = 90
  l1 = 1120
  l2 = 245
  p = 1000
  spec = 0
  type = 6
FEATURE [Part::FeaturePython] Channel001  # WARN: FeaturePython — macro-defined, semantics opaque (R4)
  Placement = pos=(0,1125,5) rot=(0,0,1;0rad)
  Reverse = true
  g0 = 7.85
  h = 1100
  k = -90
  l1 = 1120
  l2 = 245
  p = 1000
  spec = 0
  type = 6
FEATURE [Part::FeaturePython] Channel002  # WARN: FeaturePython — macro-defined, semantics opaque (R4)
  Placement = pos=(0,1125,5) rot=(0,0,1;0rad)
  Reverse = true
  g0 = 7.85
  h = 1100
  k = -90
  l1 = 1120
  l2 = 245
  p = 1000
  spec = 0
  type = 6
FEATURE [Part::FeaturePython] Corner  # WARN: FeaturePython — macro-defined, semantics opaque (R4)
  Placement = pos=(1119.4,-870,5) rot=(0,0,-1;4.71239rad)
  Reverse = false
  g0 = 7.85
  h = 1100
  k = -90
  l1 = 400
  l2 = 4860
  p = 1000
  spec = 0
  type = 2
  expr: l2 = Spreadsheet004.dia / 2 - 3390
FEATURE [Part::FeaturePython] Channel003  # WARN: FeaturePython — macro-defined, semantics opaque (R4)
  Placement = pos=(7750,-886.772,5) rot=(0,0,1;0rad)
  Reverse = false
  g0 = 7.85
  h = 1100
  k = 90
  l1 = 720
  l2 = 245
  p = 1000
  spec = 0
  type = 6
  expr: .Placement.Base.x = Spreadsheet004.dia / 2 - 500
FEATURE [Part::FeaturePython] Corner001  # WARN: FeaturePython — macro-defined, semantics opaque (R4)
  Placement = pos=(5980,-469.271,5) rot=(0,0,1;0rad)
  Reverse = false
  g0 = 7.85
  h = 1100
  k = -90
  l1 = 1050
  l2 = 165
  p = 1000
  spec = 0
  type = 2
  expr: .Placement.Base.x = Spreadsheet004.dia / 2 - 2270
FEATURE [Part::FeaturePython] Corner002  # WARN: FeaturePython — macro-defined, semantics opaque (R4)
  Placement = pos=(1119.4,874.21,5) rot=(0,0,-1;1.5708rad)
  Reverse = true
  g0 = 7.85
  h = 1100
  k = 90
  l1 = 400
  l2 = 7375
  p = 1000
  spec = 0
  type = 2
  expr: l2 = Spreadsheet004.dia / 2 - 875
FEATURE [Part::FeaturePython] Corner003  # WARN: FeaturePython — macro-defined, semantics opaque (R4)
  Placement = pos=(-1118.86,-871.912,5) rot=(0,0,-1;4.71239rad)
  Reverse = true
  g0 = 7.85
  h = 1100
  k = 90
  l1 = 400
  l2 = 7380
  p = 1000
  spec = 0
  type = 2
  expr: l2 = Spreadsheet004.dia / 2 - 870
FEATURE [Part::FeaturePython] Corner004  # WARN: FeaturePython — macro-defined, semantics opaque (R4)
  Placement = pos=(-1120.15,876.348,5) rot=(0,0,-1;1.5708rad)
  Reverse = false
  g0 = 7.85
  h = 1100
  k = -90
  l1 = 400
  l2 = 7380
  p = 1000
  spec = 0
  type = 2
  expr: l2 = Spreadsheet004.dia / 2 - 870
FEATURE [Part::Sweep] Sweep008
  Frenet = false
  Sections = -> [ChannelSteel006]
  Solid = true
  Spine = -> Sketch038 [Edge3,Edge2,Edge1]
  Transition = 1
FEATURE [Sketcher::SketchObject] Sketch039
  ArcFitTolerance = 0
  AttachmentSupport = -> [Sweep008]
  FullyConstrained = true
  MakeInternals = false
  MapMode = 5
  Placement = pos=(0,0,-1.112e-13) rot=(0,0,1;0rad)
  expr: Constraints[9] = Spreadsheet004.dia / 2 + 250
  sketch-geometry (4):
    g0: LineSegment StartX=7000 StartY=-925 StartZ=0 EndX=8500 EndY=-925 EndZ=0
    g1: LineSegment StartX=8500 StartY=-500 StartZ=0 EndX=7000 EndY=-500 EndZ=0
    g2: LineSegment StartX=7000 StartY=-500 StartZ=0 EndX=7000 EndY=-925 EndZ=0
    g3: LineSegment StartX=8500 StartY=-925 StartZ=0 EndX=8500 EndY=-500 EndZ=0
  constraints (12):
    c: Coincident(g1,g2)
    c: Coincident(g2,g0)
    c: Horizontal(g0)
    c: Horizontal(g1)
    c: Vertical(g2)
    c: Coincident(g3,g0)
    c: Coincident(g3,g1)
    c: Vertical(g3)
    c: Distance(g1,g-1) = 500
    c: DistanceX(g-1,g0) = 8500
    c: DistanceX(g0,g0) = 1500
    c: DistanceY(g3,g3) = 425
FEATURE [Part::Extrusion] Extrude024
  Base = -> Sketch039
  Dir = (0,0,1)
  DirMode = 2
  FaceMakerClass = Part::FaceMakerBullseye
  FaceMakerMode = 3
  LengthFwd = 4.5
  LengthRev = 0
  Solid = true
  Symmetric = false
FEATURE [Part::FeaturePython] Array019  # Draft array (typed FeaturePython)
  AlwaysSyncPlacement = false
  Angle = 360
  ArrayType = 0
  Axis = (0,0,1)
  Base = -> Fusion007
  Center = (0,0,0)
  Count = 4
  ExpandArray = false
  Fuse = true
  IntervalAxis = (0,0,0)
  IntervalX = (16850,0,0)
  IntervalY = (0,850,0)
  IntervalZ = (0,0,100)
  NumberCircles = 3
  NumberPolar = 5
  NumberX = 2
  NumberY = 2
  NumberZ = 1
  PlacementList = 4 placements: [(-8425,-425,-450),(-8425,425,-450),(8425,-425,-450),(8425,425,-450)]
  RadialDistance = 50
  ScaleList = (4) [(1,1,1),(1,1,1),(1,1,1),(1,1,1)]
  Symmetry = 1
  TangentialDistance = 25
  expr: .IntervalX.x = Spreadsheet004.dia + 350
FEATURE [Part::FeaturePython] Array020  # Draft array (typed FeaturePython)
  AlwaysSyncPlacement = false
  Angle = 360
  ArrayType = 1
  Axis = (0,0,1)
  Base = -> Extrude022
  Center = (0,0,750)
  Count = 2
  ExpandArray = false
  Fuse = true
  IntervalAxis = (0,0,0)
  IntervalX = (50,0,0)
  IntervalY = (0,50,0)
  IntervalZ = (0,0,50)
  NumberCircles = 3
  NumberPolar = 2
  NumberX = 2
  NumberY = 2
  NumberZ = 1
  PlacementList = 2 placements: [(0,0,0),(0,0,0)]
  RadialDistance = 50
  ScaleList = (2) [(1,1,1),(1,1,1)]
  Symmetry = 1
  TangentialDistance = 25
FEATURE [Part::Compound] Compound048  label="Compound049"
  Links = -> [Mirror012,HShapeSteel006,Sweep007,Sweep006,Sweep008,Extrude024,Array018,Array019,Array020]
FEATURE [App::Part] Part042  label="bridge001"
  Group = -> [Sketch037,HShapeSteel002,HShapeSteel003,ChannelSteel005,AngleSteel007,Mirror012,Compound046,Compound047,Array017,Extrude021,Extrude022,HShapeSteel004,Clone001,Clone002,HShapeSteel005,HShapeSteel006,Loft,Sweep007,Sweep006,Fusion003,Fusion002,Sketch035,Sketch036,Extrude023,BasePlate,H_Shape,Fusion007,Sketch038,ChannelSteel006,Sweep008,Sketch039,Extrude024,Array018,Array019,Array020,Compound048]
  Origin = -> Origin067
FEATURE [Part::Compound] Compound049  label="Compound050"
  Links = -> [Channel,Channel001,Channel002,Corner,Channel003,Corner001,Corner002,Corner003,Corner004]
FEATURE [App::Part] Part044  label="handrail"
  Group = -> [Channel,Channel001,Channel002,Corner,Channel003,Corner001,Corner002,Corner003,Corner004,Compound049]
  Origin = -> Origin069
FEATURE [App::Part] Part043  label="bridge"
  Group = -> [Part042,Spreadsheet004,Part044]
  Origin = -> Origin068
  Placement = pos=(0,0,5896.5) rot=(0,0,1;0rad)
  mass = 2505.75
FEATURE [Part::Feature] Part__Feature027  label="driveUnit"
  Placement = pos=(0,0,5556) rot=(0,0,1;0rad)
  mass = 829.84
  shape: bbox 1200 x 1200 x 927 mm, 1930 faces, 8 solids (baked)
FEATURE [Part::FeaturePython] Single_flange_straight_pipe  # WARN: FeaturePython — macro-defined, semantics opaque (R4)
  L = 600
  Placement = pos=(8066.82,0,4883) rot=(0,0,1;0rad)
  dia = 6
  fittings = 06_Single_flange_straight_pipe
  material = 0
  standard = 0
  standard2 = 1
FEATURE [Part::FeaturePython] SquarePipe  # WARN: FeaturePython — macro-defined, semantics opaque (R4)
  A = 125
  B = 125
  L = 6500
  Placement = pos=(0,0,0) rot=(0,-1,0;1.5708rad)
  Solid = true
  g0 = 7.85
  mass = 119.175
  size = 39
  standard = SS
  t = 1
  expr: L = Spreadsheet006.L0
FEATURE [Sketcher::SketchObject] Sketch045
  ArcFitTolerance = 0
  AttachmentSupport = -> [SquarePipe]
  ExternalGeometry = -> [SquarePipe]
  FullyConstrained = true
  MakeInternals = false
  MapMode = 5
  Placement = pos=(-6500,0,0) rot=(0,-1,0;1.5708rad)
  sketch-geometry (4):
    g0: LineSegment StartX=-62.5 StartY=-62.5 StartZ=0 EndX=62.5 EndY=-62.5 EndZ=0
    g1: LineSegment StartX=62.5 StartY=-62.5 StartZ=0 EndX=62.5 EndY=62.5 EndZ=0
    g2: LineSegment StartX=62.5 StartY=62.5 StartZ=0 EndX=-62.5 EndY=62.5 EndZ=0
    g3: LineSegment StartX=-62.5 StartY=62.5 StartZ=0 EndX=-62.5 EndY=-62.5 EndZ=0
  constraints (11):
    c: Coincident(g0,g1)
    c: Coincident(g1,g2)
    c: Coincident(g2,g3)
    c: Coincident(g3,g0)
    c: Horizontal(g0)
    c: Horizontal(g2)
    c: Vertical(g3)
    c: DistanceX(g2,g2) = 125
    c: Equal(g1,g0)
    c: PointOnObject(g-4,g2)
    c: Tangent(g-3,g1) = -1.5708
FEATURE [Part::Extrusion] Extrude031
  Base = -> Sketch045
  Dir = (-1,0,2e-16)
  DirMode = 2
  FaceMakerClass = Part::FaceMakerBullseye
  FaceMakerMode = 3
  LengthFwd = 6
  LengthRev = 0
  Solid = true
  Symmetric = false
FEATURE [Part::FeaturePython] Clone  label="Extrude032"  # Draft clone (typed FeaturePython)
  AttacherType = Attacher::AttachEngine3D
  Fuse = false
  Objects = -> [Extrude031]
  Placement = pos=(6506,0,0) rot=(0,0,1;0rad)
  Scale = (1,1,1)
  expr: .Placement.Base.x = Spreadsheet006.L0 + 6
FEATURE [Spreadsheet::Sheet] Spreadsheet006
  cells = A1='tankDia   D0; B1(D0)=16500; A2='bufflePosition bp; B2(bp)=1750; A3='beamLength L; B3(L0)==D0 / 2 - bp; A4='bradeWidth W0; B4(W0)==w1 * n0; A5='brade      n0; B5(n0)=6; A6='brade     w1; B6(w1)=960; A7='senterCage width cw; B7(cw)=1620
FEATURE [Sketcher::SketchObject] Sketch046  label="skimmerBrade"
  ArcFitTolerance = 0
  FullyConstrained = true
  MakeInternals = false
  Placement = pos=(0,0,0) rot=(1,0,0;1.5708rad)
  sketch-geometry (7):
    g0: LineSegment StartX=6 StartY=62.5 StartZ=0 EndX=36 EndY=62.5 EndZ=0
    g1: LineSegment StartX=36 StartY=62.5 StartZ=0 EndX=100.694 EndY=26.1551 EndZ=0
    g2: ArcOfCircle CenterX=86 CenterY=0 CenterZ=0 NormalX=0 NormalY=0 NormalZ=1 AngleXU=0 Radius=30 StartAngle=5.22424 EndAngle=7.34213
    g3: LineSegment StartX=100.694 StartY=-26.1551 StartZ=0 EndX=36 EndY=-62.5 EndZ=0
    g4: LineSegment StartX=36 StartY=-62.5 StartZ=0 EndX=6 EndY=-62.5 EndZ=0
    g5: LineSegment StartX=6 StartY=-62.5 StartZ=0 EndX=6 EndY=62.5 EndZ=0
    g6: Circle CenterX=86 CenterY=0 CenterZ=0 NormalX=0 NormalY=0 NormalZ=1 AngleXU=0 Radius=13
  constraints (17):
    c: Horizontal(g0)
    c: Coincident(g0,g1)
    c: Tangent(g1,g2) = 1.5708
    c: Coincident(g3,g4)
    c: Coincident(g4,g5)
    c: Coincident(g5,g0)
    c: PointOnObject(g6,g-1)
    c: Coincident(g0,g-3)
    c: Coincident(g4,g-3)
    c: Horizontal(g4)
    c: DistanceX(g0,g0) = 30
    c: Equal(g0,g4)
    c: Coincident(g2,g6)
    c: DistanceX(g4,g2) = 80
    c: Diameter(g6) = 26
    c: Radius(g2) = 30
    c: Tangent(g2,g3) = 1.5708
FEATURE [Part::Extrusion] Extrude032  label="Extrude033"
  Base = -> Sketch046
  Dir = (0,-1,2e-16)
  DirMode = 2
  FaceMakerClass = Part::FaceMakerBullseye
  FaceMakerMode = 3
  LengthFwd = 10
  LengthRev = 0
  Solid = true
  Symmetric = true
FEATURE [Sketcher::SketchObject] Sketch047
  ArcFitTolerance = 0
  FullyConstrained = false
  MakeInternals = false
  Placement = pos=(0,0,0) rot=(1,0,0;1.5708rad)
  sketch-geometry (7):
    g0: ArcOfCircle CenterX=81.7032 CenterY=0 CenterZ=0 NormalX=0 NormalY=0 NormalZ=1 AngleXU=0 Radius=30 StartAngle=2.05435 EndAngle=4.1734
    g1: LineSegment StartX=67.7553 StartY=26.5604 StartZ=0 EndX=131.703 EndY=60.1419 EndZ=0
    g2: LineSegment StartX=131.703 StartY=60.1419 StartZ=0 EndX=161.703 EndY=60.1419 EndZ=0
    g3: LineSegment StartX=161.703 StartY=60.1419 StartZ=0 EndX=161.703 EndY=-64.8581 EndZ=0
    g4: LineSegment StartX=161.703 StartY=-64.8581 StartZ=0 EndX=131.703 EndY=-64.8581 EndZ=0
    g5: LineSegment StartX=131.703 StartY=-64.8581 StartZ=0 EndX=66.3053 EndY=-25.7469 EndZ=0
    g6: Circle CenterX=81.7032 CenterY=0 CenterZ=0 NormalX=0 NormalY=0 NormalZ=1 AngleXU=0 Radius=13
  constraints (17):
    c: PointOnObject(g0,g-1)
    c: Coincident(g1,g2)
    c: Horizontal(g2)
    c: Coincident(g2,g3)
    c: Coincident(g3,g4)
    c: Coincident(g4,g5)
    c: Tangent(g0,g5) = 1.5708
    c: Tangent(g0,g1) = 1.5708
    c: Vertical(g3)
    c: Distance(g0,g3) = 80
    c: Horizontal(g4)
    c: DistanceX(g2,g2) = 30
    c: Equal(g2,g4)
    c: Radius(g0) = 30
    c: Coincident(g6,g0)
    c: Diameter(g6) = 26
    c: DistanceY(g3,g3) = 125
FEATURE [Part::Extrusion] Extrude033  label="Extrude034"
  Base = -> Sketch047
  Dir = (0,-1,2e-16)
  DirMode = 2
  FaceMakerClass = Part::FaceMakerBullseye
  FaceMakerMode = 3
  LengthFwd = 6
  LengthRev = 0
  Placement = pos=(0,9,0) rot=(0,0,1;0rad)
  Solid = true
  Symmetric = true
FEATURE [Sketcher::SketchObject] Sketch048
  ArcFitTolerance = 0
  AttachmentSupport = -> [Extrude033]
  ExternalGeometry = -> [Extrude033]
  FullyConstrained = false
  MakeInternals = false
  MapMode = 5
  Placement = pos=(161.703,9,0) rot=(0.57735,0.57735,0.57735;2.0944rad)
  sketch-geometry (4):
    g0: LineSegment StartX=-59 StartY=-64.8581 StartZ=0 EndX=41 EndY=-64.8581 EndZ=0
    g1: LineSegment StartX=41 StartY=-64.8581 StartZ=0 EndX=41 EndY=60.1419 EndZ=0
    g2: LineSegment StartX=41 StartY=60.1419 StartZ=0 EndX=-59 EndY=60.1419 EndZ=0
    g3: LineSegment StartX=-59 StartY=60.1419 StartZ=0 EndX=-59 EndY=-64.8581 EndZ=0
  constraints (8):
    c: Coincident(g0,g3)
    c: Coincident(g2,g3)
    c: Coincident(g0,g1)
    c: Coincident(g1,g2)
    c: DistanceY(g1,g1) = 125
    c: Horizontal(g2)
    c: Horizontal(g0)
    c: PointOnObject(g-3,g2)
FEATURE [Part::Extrusion] Extrude034  label="Extrude035"
  Base = -> Sketch048
  Dir = (1,0,0)
  DirMode = 2
  FaceMakerClass = Part::FaceMakerBullseye
  FaceMakerMode = 3
  LengthFwd = 10
  LengthRev = 0
  Solid = true
  Symmetric = false
FEATURE [Part::Feature] Part__Feature  label="CNROK75-U_b"
  shape: bbox 47.01 x 65.51 x 70.01 mm, 58 faces (baked)
FEATURE [Part::Feature] Part__Feature028  label="CNROK75-U_w"
  shape: bbox 41.3 x 78.6 x 78.6 mm, 86 faces (baked)
FEATURE [App::Part] CNROK75_U  label="CNROK75-U"
  Group = -> [Part__Feature,Part__Feature028]
  Origin = -> Origin003
  Placement = pos=(-6450,2.9e-14,-118.52) rot=(1,0,0;1.5708rad)
  expr: .Placement.Base.x = -Spreadsheet006.L0 + 50
FEATURE [Part::FeaturePython] Clone003  label="Extrude036"  # Draft clone (typed FeaturePython)
  AttacherType = Attacher::AttachEngine3D
  Fuse = false
  Objects = -> [Extrude033]
  Placement = pos=(0,-9,0) rot=(0,0,1;0rad)
  Scale = (1,1,1)
FEATURE [App::Part] Part046  label="gusset002"
  Group = -> [Sketch047,Sketch048,Extrude033,Extrude034,Clone003]
  Origin = -> Origin071
  Placement = pos=(4,0,0) rot=(0,0,1;0rad)
FEATURE [Part::Feature] Part__Feature002  label="HNS3L_1"
  shape: bbox 64 x 7.5 x 21.75 mm, 15 faces (baked)
FEATURE [Part::Feature] Part__Feature003  label="HNS3L_2"
  shape: bbox 64 x 7.5 x 21.75 mm, 12 faces (baked)
FEATURE [App::Part] HNS3L
  Group = -> [Part__Feature002,Part__Feature003]
  Origin = -> Origin073
  Placement = pos=(-430,-8,115) rot=(1,0,0;3.14159rad)
  expr: .Placement.Base.x = -Spreadsheet006.w1 / 2 + 50
FEATURE [Sketcher::SketchObject] Sketch049
  ArcFitTolerance = 0
  FullyConstrained = true
  MakeInternals = false
  Placement = pos=(0,0,0) rot=(1,0,0;1.5708rad)
  expr: Constraints[10] = Spreadsheet006.w1
  sketch-geometry (5):
    g0: LineSegment StartX=-480 StartY=-107.5 StartZ=0 EndX=-480 EndY=107.5 EndZ=0
    g1: LineSegment StartX=-480 StartY=107.5 StartZ=0 EndX=480 EndY=107.5 EndZ=0
    g2: LineSegment StartX=480 StartY=107.5 StartZ=0 EndX=480 EndY=-107.5 EndZ=0
    g3: LineSegment StartX=480 StartY=-107.5 StartZ=0 EndX=-480 EndY=-107.5 EndZ=0
    g4: GeomPoint [constr] X=0 Y=0 Z=0
  constraints (12):
    c: Coincident(g0,g1)
    c: Coincident(g1,g2)
    c: Coincident(g2,g3)
    c: Coincident(g3,g0)
    c: Horizontal(g1)
    c: Horizontal(g3)
    c: Vertical(g0)
    c: Vertical(g2)
    c: Symmetric(g1,g0,g4)
    c: Coincident(g4,g-1)
    c: Distance(g1) = 960
    c: DistanceY(g2,g2) = 215
FEATURE [Part::Extrusion] Extrude035  label="Extrude037"
  Base = -> Sketch049
  Dir = (0,-1,2e-16)
  DirMode = 2
  FaceMakerClass = Part::FaceMakerBullseye
  FaceMakerMode = 3
  LengthFwd = 5
  LengthRev = 0
  Placement = pos=(0,-4.5,-12) rot=(0,0,1;0rad)
  Solid = true
  Symmetric = false
FEATURE [Part::FeaturePython] Clone004  label="HNS3L001"  # Draft clone (typed FeaturePython)
  AttacherType = Attacher::AttachEngine3D
  Fuse = false
  Objects = -> [HNS3L]
  Placement = pos=(366,-8,115) rot=(1,0,0;3.14159rad)
  Scale = (1,1,1)
  expr: .Placement.Base.x = Spreadsheet006.w1 / 2 - 114
FEATURE [Sketcher::SketchObject] Sketch050
  ArcFitTolerance = 0
  FullyConstrained = true
  MakeInternals = false
  Placement = pos=(0,0,0) rot=(1,0,0;1.5708rad)
  expr: Constraints[11] = Spreadsheet006.w1
  sketch-geometry (5):
    g0: LineSegment StartX=-480 StartY=-37.5 StartZ=0 EndX=-480 EndY=37.5 EndZ=0
    g1: LineSegment StartX=-480 StartY=37.5 StartZ=0 EndX=480 EndY=37.5 EndZ=0
    g2: LineSegment StartX=480 StartY=37.5 StartZ=0 EndX=480 EndY=-37.5 EndZ=0
    g3: LineSegment StartX=480 StartY=-37.5 StartZ=0 EndX=-480 EndY=-37.5 EndZ=0
    g4: GeomPoint [constr] X=0 Y=0 Z=0
  constraints (12):
    c: Coincident(g0,g1)
    c: Coincident(g1,g2)
    c: Coincident(g2,g3)
    c: Coincident(g3,g0)
    c: Horizontal(g1)
    c: Horizontal(g3)
    c: Vertical(g0)
    c: Vertical(g2)
    c: Symmetric(g1,g0,g4)
    c: Coincident(g4,g-1)
    c: DistanceY(g2,g2) = 75
    c: DistanceX(g3,g3) = 960
FEATURE [Part::Extrusion] Extrude036  label="Extrude038"
  Base = -> Sketch050
  Dir = (0,-1,2e-16)
  DirMode = 2
  FaceMakerClass = Part::FaceMakerBullseye
  FaceMakerMode = 3
  LengthFwd = 3
  LengthRev = 0
  Placement = pos=(0,-9.5,70) rot=(0,0,1;0rad)
  Solid = true
  Symmetric = false
FEATURE [Sketcher::SketchObject] Sketch051
  ArcFitTolerance = 0
  AttachmentSupport = -> [Extrude035]
  ExternalGeometry = -> [Extrude035,Extrude036]
  FullyConstrained = true
  MakeInternals = false
  MapMode = 5
  Placement = pos=(-480,-4.5,-12) rot=(0.57735,-0.57735,-0.57735;2.0944rad)
  sketch-geometry (4):
    g0: LineSegment StartX=2.4e-14 StartY=107.5 StartZ=0 EndX=-3 EndY=107.5 EndZ=0
    g1: LineSegment StartX=-3 StartY=107.5 StartZ=0 EndX=-3 EndY=44.5 EndZ=0
    g2: LineSegment StartX=-3 StartY=44.5 StartZ=0 EndX=2.4e-14 EndY=44.5 EndZ=0
    g3: LineSegment StartX=2.4e-14 StartY=44.5 StartZ=0 EndX=2.4e-14 EndY=107.5 EndZ=0
  constraints (11):
    c: Coincident(g0,g1)
    c: Coincident(g1,g2)
    c: Coincident(g2,g3)
    c: Coincident(g3,g0)
    c: Horizontal(g0)
    c: Horizontal(g2)
    c: Vertical(g1)
    c: Vertical(g3)
    c: DistanceX(g0,g0) = 3
    c: Coincident(g0,g-3)
    c: Horizontal(g1,g-4)
FEATURE [Part::Extrusion] Extrude037  label="Extrude039"
  Base = -> Sketch051
  Dir = (-1,0,0)
  DirMode = 2
  FaceMakerClass = Part::FaceMakerBullseye
  FaceMakerMode = 3
  LengthFwd = 960
  LengthRev = 0
  Reversed = true
  Solid = true
  Symmetric = false
  expr: LengthFwd = Spreadsheet006.w1
FEATURE [Sketcher::SketchObject] Sketch052
  ArcFitTolerance = 0
  AttachmentSupport = -> [Extrude035]
  FullyConstrained = false
  MakeInternals = false
  MapMode = 5
  Placement = pos=(-480,-4.5,-12) rot=(0.57735,-0.57735,-0.57735;2.0944rad)
  sketch-geometry (8):
    g0: LineSegment StartX=-104.645 StartY=156.908 StartZ=0 EndX=-4.64507 EndY=156.908 EndZ=0
    g1: LineSegment StartX=3.35493 StartY=148.908 StartZ=0 EndX=3.35493 EndY=130.908 EndZ=0
    g2: LineSegment StartX=3.35493 StartY=130.908 StartZ=0 EndX=0.354931 EndY=130.908 EndZ=0
    g3: LineSegment StartX=0.354931 StartY=130.908 StartZ=0 EndX=0.354931 EndY=148.908 EndZ=0
    g4: LineSegment StartX=-4.64507 StartY=153.908 StartZ=0 EndX=-104.645 EndY=153.908 EndZ=0
    g5: LineSegment StartX=-104.645 StartY=153.908 StartZ=0 EndX=-104.645 EndY=156.908 EndZ=0
    g6: ArcOfCircle CenterX=-4.64507 CenterY=148.908 CenterZ=0 NormalX=0 NormalY=0 NormalZ=1 AngleXU=0 Radius=5 StartAngle=3.3e-15 EndAngle=1.5708
    g7: ArcOfCircle CenterX=-4.64507 CenterY=148.908 CenterZ=0 NormalX=0 NormalY=0 NormalZ=1 AngleXU=0 Radius=8 StartAngle=-1.8e-15 EndAngle=1.5708
  constraints (19):
    c: Horizontal(g0)
    c: Vertical(g1)
    c: Coincident(g1,g2)
    c: Horizontal(g2)
    c: Coincident(g2,g3)
    c: Vertical(g3)
    c: Horizontal(g4)
    c: Coincident(g4,g5)
    c: Coincident(g5,g0)
    c: Vertical(g5)
    c: DistanceX(g2,g2) = 3
    c: Tangent(g3,g6) = -1.5708
    c: Tangent(g4,g6) = -1.5708
    c: Tangent(g1,g7) = 1.5708
    c: Tangent(g0,g7) = 1.5708
    c: Coincident(g6,g7)
    c: DistanceX(g4,g4) = 100
    c: DistanceY(g3,g3) = 18
    c: Radius(g6) = 5
FEATURE [Part::Extrusion] Extrude038  label="Extrude040"
  Base = -> Sketch052
  Dir = (-1,0,0)
  DirMode = 2
  FaceMakerClass = Part::FaceMakerBullseye
  FaceMakerMode = 3
  LengthFwd = 80
  LengthRev = 0
  Placement = pos=(34,0,0) rot=(0,0,1;0rad)
  Reversed = true
  Solid = true
  Symmetric = false
FEATURE [Part::FeaturePython] Clone005  label="Extrude041"  # Draft clone (typed FeaturePython)
  AttacherType = Attacher::AttachEngine3D
  Fuse = false
  Objects = -> [Extrude038]
  Placement = pos=(830,0,0) rot=(0,0,1;0rad)
  Scale = (1,1,1)
  expr: .Placement.Base.x = Spreadsheet006.w1 - (50 + 46 + 34)
FEATURE [App::Part] Part003  label="brade001"
  Group = -> [Sketch049,Extrude035,Clone004,HNS3L,Sketch050,Extrude036,Sketch051,Extrude037,Sketch052,Extrude038,Clone005]
  Origin = -> Origin074
  Placement = pos=(-5940,-100,-207.547) rot=(0,0,1;0rad)
  expr: .Placement.Base.x = -Spreadsheet006.L0 + 560
FEATURE [Part::FeaturePython] Array023  label="brade002"  # Draft array (typed FeaturePython)
  AlwaysSyncPlacement = false
  Angle = 360
  ArrayType = 0
  Axis = (0,0,1)
  Base = -> Part003
  Center = (0,0,0)
  Count = 6
  ExpandArray = false
  Fuse = false
  IntervalAxis = (0,0,0)
  IntervalX = (960,0,0)
  IntervalY = (0,100,0)
  IntervalZ = (0,0,100)
  NumberCircles = 3
  NumberPolar = 5
  NumberX = 6
  NumberY = 1
  NumberZ = 1
  PlacementList = 6 placements: arithmetic series from (-5940,-100,-207.547) step (960,0,0) to (-1140,-100,-207.547)
  RadialDistance = 50
  ScaleList = (6) [(1,1,1),(1,1,1),(1,1,1),(1,1,1),(1,1,1),(1,1,1)]
  Symmetry = 1
  TangentialDistance = 25
  expr: .IntervalX.x = Spreadsheet006.w1
  expr: NumberX = <<Spreadsheet006>>.n0
FEATURE [Part::FeaturePython] ChannelSteel008  # WARN: FeaturePython — macro-defined, semantics opaque (R4)
  B = 75
  H = 150
  L = 1000
  Placement = pos=(176,0,-75) rot=(0,0,1;0rad)
  Solid = false
  g0 = 7.85
  mass = 0
  size = 3
  standard = SS
  t1 = 6.5
  t2 = 10
FEATURE [Part::Extrusion] Extrude039  label="Extrude042"
  Base = -> ChannelSteel008
  Dir = (0,1,0)
  DirMode = 2
  FaceMakerClass = Part::FaceMakerBullseye
  FaceMakerMode = 3
  LengthFwd = 1620
  LengthRev = 0
  Solid = false
  Symmetric = true
  expr: LengthFwd = Spreadsheet006.cw
FEATURE [Sketcher::SketchObject] Sketch053
  ArcFitTolerance = 0
  FullyConstrained = true
  MakeInternals = false
  MapMode = 5
  Placement = pos=(0,0,62.5) rot=(0,0,1;0rad)
  sketch-geometry (6):
    g0: LineSegment StartX=-2985 StartY=62.5 StartZ=0 EndX=-2985 EndY=112.5 EndZ=0
    g1: ArcOfCircle CenterX=-3000 CenterY=112.5 CenterZ=0 NormalX=0 NormalY=0 NormalZ=1 AngleXU=0 Radius=15 StartAngle=0 EndAngle=1.98689
    g2: LineSegment StartX=-3006.06 StartY=126.22 StartZ=0 EndX=-3105 EndY=82.5 EndZ=0
    g3: LineSegment StartX=-3105 StartY=82.5 StartZ=0 EndX=-3105 EndY=62.5 EndZ=0
    g4: LineSegment StartX=-3105 StartY=62.5 StartZ=0 EndX=-2985 EndY=62.5 EndZ=0
    g5: Circle CenterX=-3000 CenterY=112.5 CenterZ=0 NormalX=0 NormalY=0 NormalZ=1 AngleXU=0 Radius=7.5
  constraints (16):
    c: Tangent(g0,g1) = -1.5708
    c: Coincident(g2,g3)
    c: Vertical(g3)
    c: Coincident(g3,g4)
    c: Coincident(g4,g0)
    c: Coincident(g5,g1)
    c: Diameter(g5) = 15
    c: Radius(g1) = 15
    c: Vertical(g0)
    c: Tangent(g1,g2) = -1.5708
    c: Horizontal(g4)
    c: DistanceY(g3,g3) = 20
    c: DistanceX(g4,g4) = 120
    c: DistanceY(g0,g1) = 50
    c: DistanceY(g-1,g0) = 62.5
    c: DistanceX(g-2,g1) = -3000
FEATURE [Part::Extrusion] Extrude040  label="Extrude043"
  Base = -> Sketch053
  Dir = (0,0,1)
  DirMode = 2
  FaceMakerClass = Part::FaceMakerBullseye
  FaceMakerMode = 3
  LengthFwd = 6
  LengthRev = 0
  Placement = pos=(0,0,-62.5) rot=(0,0,1;0rad)
  Solid = true
  Symmetric = true
FEATURE [Part::Mirroring] Mirror018  label="Extrude020 (mirrored)"
  Base = (-3100,0,0)
  Normal = (0,-1,0)
  Source = -> Extrude040
FEATURE [App::Part] Part045  label="hontai"
  Group = -> [Sketch046,Clone,SquarePipe,Sketch045,Extrude031,Extrude032,Sketch053,Extrude040,Mirror018]
  Origin = -> Origin070
FEATURE [Part::Compound] Compound051  label="hontai001"
  Links = -> [Part045]
FEATURE [Sketcher::SketchObject] Sketch054
  ArcFitTolerance = 0
  AttachmentSupport = -> [Extrude039]
  FullyConstrained = false
  MakeInternals = false
  MapMode = 5
  Placement = pos=(0,0,75) rot=(0,0,1;0rad)
  sketch-geometry (7):
    g0: LineSegment StartX=176 StartY=810 StartZ=0 EndX=156 EndY=810 EndZ=0
    g1: LineSegment StartX=156 StartY=810 StartZ=0 EndX=118.097 EndY=782.845 EndZ=0
    g2: ArcOfCircle CenterX=126 CenterY=771.813 CenterZ=0 NormalX=0 NormalY=0 NormalZ=1 AngleXU=0 Radius=13.5708 StartAngle=2.19246 EndAngle=4.21323
    g3: LineSegment StartX=119.504 StartY=759.898 StartZ=0 EndX=156 EndY=740 EndZ=0
    g4: LineSegment StartX=156 StartY=740 StartZ=0 EndX=176 EndY=740 EndZ=0
    g5: LineSegment StartX=176 StartY=740 StartZ=0 EndX=176 EndY=810 EndZ=0
    g6: Circle CenterX=126 CenterY=771.813 CenterZ=0 NormalX=0 NormalY=0 NormalZ=1 AngleXU=0 Radius=7.5
  constraints (16):
    c: Horizontal(g0)
    c: Coincident(g0,g1)
    c: Tangent(g1,g2) = -1.5708
    c: Coincident(g3,g4)
    c: Horizontal(g4)
    c: Coincident(g4,g5)
    c: Coincident(g5,g0)
    c: Vertical(g5)
    c: Coincident(g6,g2)
    c: Diameter(g6) = 15
    c: Coincident(g0,g-3)
    c: DistanceY(g5,g5) = 70
    c: Tangent(g2,g3) = -1.5708
    c: Vertical(g0,g3)
    c: DistanceX(g0,g0) = 20
    c: Distance(g2,g5) = 50
FEATURE [Part::Extrusion] Extrude041  label="Extrude044"
  Base = -> Sketch054
  Dir = (0,0,1)
  DirMode = 2
  FaceMakerClass = Part::FaceMakerBullseye
  FaceMakerMode = 3
  LengthFwd = 6
  LengthRev = 0
  Placement = pos=(0,0,-75) rot=(0,0,1;0rad)
  Solid = true
  Symmetric = true
FEATURE [Part::Mirroring] Mirror002  label="Extrude021 (mirrored)"
  Base = (1000,0,0)
  Normal = (0,-1,0)
  Source = -> Extrude041
FEATURE [Spreadsheet::Sheet] Spreadsheet007  label="Spreadsheet002"
  cells = A2='rodDia dia; B2(dia)=12; C2='thickness; D2(t0)=6; A3='length L0; B3(L0)=3195; C3='l1; D3(l1)==L0 - (dia * 5 + 500); B4='l; C4='l1; D4='a; E4='b; F4='c; G4='e; H4='f; I4='g; J4='h; K4='i; L4='r; A5='forkEndR; B5=80; D5=25; E5=10; F5=14; G5=16; H5=13; I5=40; J5=5; K5=13; L5=15; A6='turnBackle; B6=100; C6=20; D6=30; E6=16; F6=22; A7='forkEndL; B7=60; D7=25; E7=10; F7=13; G7=16; H7=13; I7=20; L7=15; A8=1; B8=2; C8=3; D8=4; E8=5; F8=6; G8=7; H8=8; I8=9; J8=10; K8=11; L8=12; A9='turnBackle; A10='d; B10='l; C10='l1; D10='a; E10='b; F10='c; G10='t0; A11=10; B11=75; C11=15; D11=24; E11=13; F11=17; G11=6; A12=12; B12=100; C12=20; D12=30; E12=16; F12=22; G12=6; A13=16; B13=125; C13=24; D13=36; E13=20; F13=27; G13=9; A14=20; B14=150; C14=28; D14=42; E14=23; F14=33; G14=9; A15=22; B15=175; C15=33; D15=48; E15=27; F15=37; G15=9; A16=24; B16=200; C16=38; D16=54; E16=30; F16=42; G16=12; A17=30; B17=250; C17=47; D17=66; E17=37; F17=52; G17=12; A18='forkEnd_L; A19='d; B19='l; C19='a; D19='b; E19='c; F19='e; G19='f; H19='g; I19='r; A20=10; B20=50; C20=20; D20=7; E20=10; F20=12; G20=10; H20=15; I20=12; A21=12; B21=60; C21=25; D21=10; E21=13; F21=16; G21=13; H21=20; I21=15; A22=16; B22=75; C22=30; D22=13; E22=16; F22=20; G22=16; H22=25; I22=19; A23=20; B23=90; C23=40; D23=16; E23=20; F23=24; G23=20; H23=30; I23=23; A24=22; B24=100; C24=45; D24=20; E24=23; F24=28; G24=23; H24=35; I24=27; A25=24; B25=115; C25=50; D25=23; E25=26; F25=32; G25=26; H25=40; I25=30; A26=30; B26=140; C26=65; D26=30; E26=33; F26=40; G26=33; H26=50; I26=38; A27='forkEnd_R; A28='d; B28='l; C28='a; D28='b; E28='c; F28='r; G28='e; H28='f; I28='g; J28='h; K28='i; A29=10; +76 more cells
FEATURE [Sketcher::SketchObject] Sketch055
  ArcFitTolerance = 0
  FullyConstrained = true
  MakeInternals = false
  Placement = pos=(0,0,0) rot=(1,0,0;1.5708rad)
  expr: Constraints[11] = Spreadsheet007.I5 + Spreadsheet007.dia * 2
  expr: Constraints[1] = Spreadsheet007.F5 / 2
  expr: Constraints[3] = Spreadsheet007.L5
  sketch-geometry (5):
    g0: Circle CenterX=0 CenterY=0 CenterZ=0 NormalX=0 NormalY=0 NormalZ=1 AngleXU=0 Radius=7
    g1: ArcOfCircle CenterX=0 CenterY=0 CenterZ=0 NormalX=0 NormalY=0 NormalZ=1 AngleXU=0 Radius=15 StartAngle=4.71239 EndAngle=7.85398
    g2: LineSegment StartX=-4.87e-14 StartY=15 StartZ=0 EndX=-64 EndY=15 EndZ=0
    g3: LineSegment StartX=-64 StartY=15 StartZ=0 EndX=-64 EndY=-15 EndZ=0
    g4: LineSegment StartX=-64 StartY=-15 StartZ=0 EndX=0 EndY=-15 EndZ=0
  constraints (12):
    c: Coincident(g0,g-1)
    c: Radius(g0) = 7
    c: Coincident(g1,g0)
    c: Radius(g1) = 15
    c: Horizontal(g2)
    c: Coincident(g2,g3)
    c: Vertical(g3)
    c: Coincident(g3,g4)
    c: Horizontal(g4)
    c: Tangent(g1,g2) = -1.5708
    c: Tangent(g1,g4) = -1.5708
    c: Distance(g2) = 64
FEATURE [Part::Cylinder] Cylinder002  label="円柱001"
  Angle = 360
  AttacherType = Attacher::AttachEngine3D
  FirstAngle = 0
  Height = 500
  Placement = pos=(-24,0,0) rot=(0,-1,0;1.5708rad)
  Radius = 6
  SecondAngle = 0
  expr: .Placement.Base.x = -Spreadsheet007.dia * 2
  expr: Radius = Spreadsheet007.dia / 2
FEATURE [Sketcher::SketchObject] Sketch056
  ArcFitTolerance = 0
  FullyConstrained = true
  MakeInternals = false
  Placement = pos=(0,0,0) rot=(1,0,0;1.5708rad)
  expr: Constraints[10] = Spreadsheet007.C6
  expr: Constraints[11] = Spreadsheet007.B6
  expr: Constraints[12] = Spreadsheet007.D6 / 2
  expr: Constraints[13] = Spreadsheet007.F6 / 2
  expr: Constraints[14] = Spreadsheet007.B6 / 2
  expr: Constraints[17] = Spreadsheet007.C6
  sketch-geometry (6):
    g0: LineSegment StartX=-50 StartY=0 StartZ=0 EndX=-50 EndY=11 EndZ=0
    g1: LineSegment StartX=-50 StartY=11 StartZ=0 EndX=-30 EndY=15 EndZ=0
    g2: LineSegment StartX=-30 StartY=15 StartZ=0 EndX=30 EndY=15 EndZ=0
    g3: LineSegment StartX=30 StartY=15 StartZ=0 EndX=50 EndY=11 EndZ=0
    g4: LineSegment StartX=50 StartY=11 StartZ=0 EndX=50 EndY=0 EndZ=0
    g5: LineSegment StartX=50 StartY=0 StartZ=0 EndX=-50 EndY=0 EndZ=0
  constraints (18):
    c: PointOnObject(g0,g-1)
    c: Vertical(g0)
    c: Coincident(g0,g1)
    c: Coincident(g1,g2)
    c: Horizontal(g2)
    c: Coincident(g2,g3)
    c: Coincident(g3,g4)
    c: PointOnObject(g4,g-1)
    c: Vertical(g4)
    c: Coincident(g4,g5)
    c: DistanceX(g2,g3) = 20
    c: DistanceX(g0,g3) = 100
    c: Distance(g1,g5) = 15
    c: Distance(g4) = 11
    c: DistanceX(g-1,g4) = 50
    c: Horizontal(g0,g3)
    c: Coincident(g5,g0)
    c: DistanceX(g0,g1) = 20
FEATURE [Part::Revolution] Revolve013
  Angle = 360
  Axis = (-1,0,0)
  AxisLink = -> Sketch056 [Edge6]
  Base = (-50,0,0)
  FaceMakerClass = Part::FaceMakerBullseye
  Solid = true
  Source = -> Sketch056
  Symmetric = false
FEATURE [Sketcher::SketchObject] Sketch057
  ArcFitTolerance = 0
  FullyConstrained = false
  MakeInternals = false
  Placement = pos=(0,0,0) rot=(0.57735,0.57735,0.57735;2.0944rad)
  expr: Constraints[16] = Spreadsheet007.F6
  expr: Constraints[17] = Spreadsheet007.F6 / 2
  sketch-geometry (8):
    g0: LineSegment StartX=-11 StartY=39.685 StartZ=0 EndX=-26 EndY=39.685 EndZ=0
    g1: LineSegment StartX=-26 StartY=39.685 StartZ=0 EndX=-26 EndY=-39.3666 EndZ=0
    g2: LineSegment StartX=-26 StartY=-39.3666 StartZ=0 EndX=-11 EndY=-39.3666 EndZ=0
    g3: LineSegment StartX=-11 StartY=-39.3666 StartZ=0 EndX=-11 EndY=39.685 EndZ=0
    g4: LineSegment StartX=11 StartY=39.685 StartZ=0 EndX=26 EndY=39.685 EndZ=0
    g5: LineSegment StartX=26 StartY=39.685 StartZ=0 EndX=26 EndY=-40.315 EndZ=0
    g6: LineSegment StartX=26 StartY=-40.315 StartZ=0 EndX=11 EndY=-40.315 EndZ=0
    g7: LineSegment StartX=11 StartY=-40.315 StartZ=0 EndX=11 EndY=39.685 EndZ=0
  constraints (22):
    c: Coincident(g0,g1)
    c: Coincident(g1,g2)
    c: Coincident(g2,g3)
    c: Coincident(g3,g0)
    c: Horizontal(g0)
    c: Horizontal(g2)
    c: Vertical(g1)
    c: Vertical(g3)
    c: Coincident(g4,g5)
    c: Coincident(g5,g6)
    c: Coincident(g6,g7)
    c: Coincident(g7,g4)
    c: Horizontal(g4)
    c: Horizontal(g6)
    c: Vertical(g5)
    c: Vertical(g7)
    c: DistanceX(g0,g4) = 22
    c: Distance(g-1,g7) = 11
    c: Distance(g5) = 80
    c: Distance(g4) = 15
    c: Distance(g0) = 15
    c: Horizontal(g0,g4)
FEATURE [Part::Extrusion] Extrude042  label="Extrude045"
  Base = -> Sketch057
  Dir = (1,0,0)
  DirMode = 2
  FaceMakerClass = Part::FaceMakerBullseye
  FaceMakerMode = 3
  LengthFwd = 300
  LengthRev = 0
  Solid = true
  Symmetric = true
FEATURE [Part::Cut] Cut016
  Base = -> Revolve013
  Tool = -> Extrude042
FEATURE [Sketcher::SketchObject] Sketch058
  ArcFitTolerance = 0
  FullyConstrained = true
  MakeInternals = false
  Placement = pos=(0,0,0) rot=(1,0,0;1.5708rad)
  expr: Constraints[17] = Spreadsheet007.E6
  expr: Constraints[18] = Spreadsheet007.B6 - 2 * Spreadsheet007.C6
  expr: Constraints[19] = (Spreadsheet007.B6 - 2 * Spreadsheet007.C6) / 2
  expr: Constraints[20] = Spreadsheet007.E6 / 2
  sketch-geometry (9):
    g0: LineSegment StartX=30 StartY=3 StartZ=0 EndX=30 EndY=-3 EndZ=0
    g1: LineSegment StartX=25 StartY=-8 StartZ=0 EndX=-25 EndY=-8 EndZ=0
    g2: LineSegment StartX=-30 StartY=-3 StartZ=0 EndX=-30 EndY=3 EndZ=0
    g3: LineSegment StartX=-25 StartY=8 StartZ=0 EndX=25 EndY=8 EndZ=0
    g4: GeomPoint [constr] X=0 Y=0 Z=0
    g5: ArcOfCircle CenterX=-25 CenterY=3 CenterZ=0 NormalX=0 NormalY=0 NormalZ=1 AngleXU=0 Radius=5 StartAngle=1.5708 EndAngle=3.14159
    g6: ArcOfCircle CenterX=-25 CenterY=-3 CenterZ=0 NormalX=0 NormalY=0 NormalZ=1 AngleXU=0 Radius=5 StartAngle=3.14159 EndAngle=4.71239
    g7: ArcOfCircle CenterX=25 CenterY=-3 CenterZ=0 NormalX=0 NormalY=0 NormalZ=1 AngleXU=0 Radius=5 StartAngle=4.71239 EndAngle=6.28319
    g8: ArcOfCircle CenterX=25 CenterY=3 CenterZ=0 NormalX=0 NormalY=0 NormalZ=1 AngleXU=0 Radius=5 StartAngle=-4.09e-14 EndAngle=1.5708
  constraints (21):
    c: Horizontal(g1)
    c: Horizontal(g3)
    c: Vertical(g0)
    c: Vertical(g2)
    c: Coincident(g4,g-1)
    c: Tangent(g3,g5) = 1.5708
    c: Tangent(g2,g5) = 1.5708
    c: Tangent(g1,g6) = 1.5708
    c: Tangent(g2,g6) = 1.5708
    c: Tangent(g1,g7) = 1.5708
    c: Tangent(g0,g7) = 1.5708
    c: Tangent(g0,g8) = 1.5708
    c: Tangent(g3,g8) = 1.5708
    c: Radius(g8) = 5
    c: Equal(g8,g7)
    c: Equal(g7,g6)
    c: Equal(g6,g5)
    c: DistanceY(g1,g3) = 16
    c: DistanceX(g2,g0) = 60
    c: Distance(g4,g2) = 30
    c: Distance(g4,g1) = 8
FEATURE [Part::Extrusion] Extrude043  label="Extrude046"
  Base = -> Sketch058
  Dir = (0,-1,2e-16)
  DirMode = 2
  FaceMakerClass = Part::FaceMakerBullseye
  FaceMakerMode = 3
  LengthFwd = 60
  LengthRev = 0
  Solid = true
  Symmetric = true
FEATURE [Part::Cut] Cut017
  Base = -> Cut016
  Tool = -> Extrude043
FEATURE [Sketcher::SketchObject] Sketch059
  ArcFitTolerance = 0
  FullyConstrained = true
  MakeInternals = false
  Placement = pos=(0,0,0) rot=(0.57735,0.57735,0.57735;2.0944rad)
  expr: Constraints[1] = Spreadsheet007.dia / 2
  sketch-geometry (1):
    g0: Circle CenterX=0 CenterY=0 CenterZ=0 NormalX=0 NormalY=0 NormalZ=1 AngleXU=0 Radius=6
  constraints (2):
    c: Coincident(g0,g-1)
    c: Radius(g0) = 6
FEATURE [Part::Extrusion] Extrude044  label="Extrude047"
  Base = -> Sketch059
  Dir = (1,0,0)
  DirMode = 2
  FaceMakerClass = Part::FaceMakerBullseye
  FaceMakerMode = 3
  LengthFwd = 300
  LengthRev = 0
  Solid = true
  Symmetric = true
FEATURE [Part::Cut] Cut018  label="turnBackle001"
  Base = -> Cut017
  Placement = pos=(-530,0,0) rot=(0,0,1;0rad)
  Tool = -> Extrude044
  expr: .Placement.Base.x = -(Spreadsheet007.dia * 2.5 + 500)
FEATURE [Part::Cylinder] Cylinder003  label="rod001"
  Angle = 360
  AttacherType = Attacher::AttachEngine3D
  FirstAngle = 0
  Height = 2635
  Placement = pos=(-536,0,-1.37e-13) rot=(0,-1,0;1.5708rad)
  Radius = 6
  SecondAngle = 0
  expr: .Placement.Base.x = -(Spreadsheet007.dia * 3 + 500)
  expr: Height = Spreadsheet007.l1
  expr: Radius = Spreadsheet007.dia / 2
FEATURE [Part::Extrusion] Extrude045  label="Extrude048"
  Base = -> Sketch055
  Dir = (0,-1,2e-16)
  DirMode = 2
  FaceMakerClass = Part::FaceMakerBullseye
  FaceMakerMode = 3
  LengthFwd = 6
  LengthRev = 0
  Placement = pos=(0,9,0) rot=(0,0,1;0rad)
  Solid = true
  Symmetric = true
  expr: .Placement.Base.y = Spreadsheet007.dia / 2 + Spreadsheet007.t0 / 2
  expr: LengthFwd = Spreadsheet007.t0
FEATURE [Part::FeaturePython] Clone006  label="Extrude049"  # Draft clone (typed FeaturePython)
  AttacherType = Attacher::AttachEngine3D
  Fuse = false
  Objects = -> [Extrude045]
  Placement = pos=(-3195,9,0) rot=(0,1,0;3.14159rad)
  Scale = (1,1,1)
  expr: .Placement.Base.x = -Spreadsheet007.L0
  expr: .Placement.Base.y = Spreadsheet007.t0 / 2 + Spreadsheet007.dia / 2
FEATURE [App::Part] Part048  label="TurnBackleB"
  Group = -> [Spreadsheet007,Sketch055,Cylinder002,Extrude045,Revolve013,Sketch057,Cut017,Cut016,Extrude042,Extrude043,Extrude044,Sketch058,Sketch056,Sketch059,Cut018,Cylinder003,Clone006]
  Origin = -> Origin007
  Placement = pos=(-1778.27,238.926,0) rot=(1,0,0;4.71239rad)
FEATURE [Part::Compound] Compound052  label="trunBackle"
  Links = -> [Part048]
  Placement = pos=(-4690.78,487.977,0) rot=(0,0,1;2.9339rad)
FEATURE [Part::Mirroring] Mirror003  label="trunBackle (mirrored)"
  Base = (1000,0,0)
  Normal = (0,-1,0)
  Source = -> Compound052
FEATURE [App::Part] Part047  label="skimmerBrade001"
  Group = -> [Part046,Part045,CNROK75_U,Compound051,Spreadsheet006,Part003,Array023,ChannelSteel008,Extrude039,Sketch054,Extrude041,Mirror002,Part048,Compound052,Mirror003]
  Origin = -> Origin072
  Placement = pos=(-1076.02,0,5204.79) rot=(0,0,1;0rad)
  mass = 104.213
FEATURE [Part::FeaturePython] Flange  # WARN: FeaturePython — macro-defined, semantics opaque (R4)
  Placement = pos=(0,0,0) rot=(0.57735,0.57735,0.57735;2.0944rad)
  dia = 6
  fittings = 00_Flange
  material = 0
  standard = 1
FEATURE [Part::FeaturePython] Ring  # WARN: FeaturePython — macro-defined, semantics opaque (R4)
  D = 360
  Placement = pos=(0,0,0) rot=(0,1,0;1.5708rad)
  d = 315
  sface = 0
FEATURE [Part::Extrusion] Extrude046  label="Extrude050"
  Base = -> Ring
  Dir = (1,0,0)
  DirMode = 2
  FaceMakerClass = Part::FaceMakerBullseye
  FaceMakerMode = 3
  LengthFwd = 380
  LengthRev = 0
  Reversed = true
  Solid = true
  Symmetric = false
FEATURE [App::Part] Part049  label="pipeSkimmerBrg"
  Group = -> [Ring,Extrude046,Flange]
  Origin = -> Origin075
  Placement = pos=(7931,-1.1983e-12,0) rot=(0,0,1;0rad)
  mass = 86.9914
  expr: .Placement.Base.x = Spreadsheet008.L0 - Spreadsheet008.l1 + Spreadsheet008.l1 - 300 + Spreadsheet008.l4 - 19
FEATURE [Part::FeaturePython] Straight_tube  # WARN: FeaturePython — macro-defined, semantics opaque (R4)
  L = 6150
  Placement = pos=(1480,0,0) rot=(0,0,1;0rad)
  dia = 16
  fittings = 05_Straight pipe
  material = 1
  standard = 1
  expr: .Placement.Base.x = Spreadsheet008.l4 - 320
  expr: L = Spreadsheet008.L0 - 300
FEATURE [Sketcher::SketchObject] Sketch060
  ArcFitTolerance = 0
  FullyConstrained = true
  MakeInternals = false
  Placement = pos=(0,0,0) rot=(1,0,0;1.5708rad)
  expr: Constraints[35] = Spreadsheet008.L0 - 400
  sketch-geometry (12):
    g0: LineSegment StartX=6030 StartY=159.25 StartZ=0 EndX=6050 EndY=159.25 EndZ=0
    g1: LineSegment StartX=6050 StartY=159.25 StartZ=0 EndX=6050 EndY=164.25 EndZ=0
    g2: LineSegment StartX=6050 StartY=164.25 StartZ=0 EndX=6030 EndY=164.25 EndZ=0
    g3: LineSegment StartX=6030 StartY=164.25 StartZ=0 EndX=6030 EndY=159.25 EndZ=0
    g4: LineSegment StartX=0 StartY=159.25 StartZ=0 EndX=0 EndY=169.25 EndZ=0
    g5: LineSegment StartX=0 StartY=169.25 StartZ=0 EndX=19 EndY=169.25 EndZ=0
    g6: LineSegment StartX=19 StartY=169.25 StartZ=0 EndX=19 EndY=164.25 EndZ=0
    g7: LineSegment StartX=19 StartY=164.25 StartZ=0 EndX=31 EndY=164.25 EndZ=0
    g8: LineSegment StartX=31 StartY=164.25 StartZ=0 EndX=31 EndY=169.25 EndZ=0
    g9: LineSegment StartX=31 StartY=169.25 StartZ=0 EndX=50 EndY=169.25 EndZ=0
    g10: LineSegment StartX=50 StartY=169.25 StartZ=0 EndX=50 EndY=159.25 EndZ=0
    g11: LineSegment StartX=50 StartY=159.25 StartZ=0 EndX=0 EndY=159.25 EndZ=0
  constraints (36):
    c: Coincident(g0,g1)
    c: Coincident(g1,g2)
    c: Coincident(g2,g3)
    c: Coincident(g3,g0)
    c: Horizontal(g0)
    c: Horizontal(g2)
    c: Vertical(g1)
    c: Vertical(g3)
    c: DistanceY(g-1,g0) = 159.25
    c: DistanceY(g1,g1) = 5
    c: DistanceX(g2,g2) = 20
    c: Vertical(g4)
    c: Coincident(g4,g5)
    c: Horizontal(g5)
    c: Coincident(g5,g6)
    c: Vertical(g6)
    c: Coincident(g6,g7)
    c: Coincident(g7,g8)
    c: Coincident(g8,g9)
    c: Coincident(g9,g10)
    c: Coincident(g10,g11)
    c: Coincident(g11,g4)
    c: Horizontal(g11)
    c: Vertical(g10)
    c: Horizontal(g7)
    c: Horizontal(g9)
    c: Vertical(g8)
    c: DistanceY(g10,g10) = 10
    c: DistanceY(g7,g8) = 5
    c: Horizontal(g8,g5)
    c: DistanceX(g11,g11) = 50
    c: DistanceX(g7,g7) = 12
    c: DistanceX(g5,g5) = 19
    c: DistanceY(g-1,g4) = 159.25
    c: Vertical(g-1,g4)
    c: DistanceX(g-1,g0) = 6050
FEATURE [Part::Revolution] Revolve014
  Angle = 360
  Axis = (1,0,0)
  Base = (0,0,0)
  FaceMakerClass = Part::FaceMakerBullseye
  Placement = pos=(1500,0,0) rot=(0,0,1;0rad)
  Solid = true
  Source = -> Sketch060
  Symmetric = false
  expr: .Placement.Base.x = Spreadsheet008.l4 - 300
FEATURE [Spreadsheet::Sheet] Spreadsheet008  label="Spreadsheet_pipeSkimmer"
  cells = A2='tankDia  D0; B2(D0)=13000; A3='fullLength L0; B3(L0)=6450; A4='length       l1; B4(l1)=170; A5='越流堰数 n0; B5(n0)=4; A6='越流堰長 l3; B6(l3)=1200; A7='開閉台  h2; B7(h2)=1061; A8='開閉台 位置 l2; B8(l2)=430; A9='軸受位置 l4; B9(l4)=1800
FEATURE [Sketcher::SketchObject] Sketch061
  ArcFitTolerance = 0
  FullyConstrained = false
  MakeInternals = false
  Placement = pos=(0,0,0) rot=(0.57735,0.57735,0.57735;2.0944rad)
  sketch-geometry (3):
    g0: LineSegment StartX=0 StartY=0 StartZ=0 EndX=114.659 EndY=220.257 EndZ=0
    g1: LineSegment StartX=0 StartY=0 StartZ=0 EndX=-114.659 EndY=220.257 EndZ=0
    g2: ArcOfCircle CenterX=0 CenterY=0 CenterZ=0 NormalX=0 NormalY=0 NormalZ=1 AngleXU=0 Radius=248.314 StartAngle=1.09083 EndAngle=2.05076
  constraints (7):
    c: Coincident(g-1,g0)
    c: Coincident(g1,g0)
    c: Coincident(g2,g0)
    c: Coincident(g2,g1)
    c: Coincident(g2,g0)
    c: Angle(g0,g-2) = 0.479966
    c: Angle(g0,g1) = 0.959931
FEATURE [Part::Extrusion] Extrude047  label="Extrude051"
  Base = -> Sketch061
  Dir = (1,0,0)
  DirMode = 2
  FaceMakerClass = Part::FaceMakerBullseye
  FaceMakerMode = 3
  LengthFwd = 1200
  LengthRev = 0
  Placement = pos=(-200,0,0) rot=(0,0,1;0rad)
  Solid = true
  Symmetric = false
  expr: LengthFwd = Spreadsheet008.l3
FEATURE [Part::FeaturePython] Array024  # Draft array (typed FeaturePython)
  AlwaysSyncPlacement = false
  Angle = 360
  ArrayType = 0
  Axis = (0,0,1)
  Base = -> Extrude047
  Center = (0,0,0)
  Count = 4
  ExpandArray = false
  Fuse = false
  IntervalAxis = (0,0,0)
  IntervalX = (1250,0,0)
  IntervalY = (0,100,0)
  IntervalZ = (0,0,100)
  NumberCircles = 3
  NumberPolar = 5
  NumberX = 4
  NumberY = 1
  NumberZ = 1
  Placement = pos=(1781,0,0) rot=(0,0,1;0rad)
  PlacementList = 4 placements: arithmetic series from (-200,0,0) step (1250,0,0) to (3550,0,0)
  RadialDistance = 50
  ScaleList = (4) [(1,1,1),(1,1,1),(1,1,1),(1,1,1)]
  Symmetry = 1
  TangentialDistance = 25
  expr: .IntervalX.x = Spreadsheet008.l3 + 50
  expr: .Placement.Base.x = Spreadsheet008.l4 - 19
  expr: NumberX = Spreadsheet008.n0
FEATURE [Part::Cut] Cut019
  Base = -> Straight_tube
  Tool = -> Array024
FEATURE [Sketcher::SketchObject] Sketch062
  ArcFitTolerance = 0
  FullyConstrained = false
  MakeInternals = false
  Placement = pos=(-30,0,0) rot=(0.57735,0.57735,0.57735;2.0944rad)
  expr: .Placement.Base.x = -30
  sketch-geometry (3):
    g0: LineSegment StartX=0 StartY=0 StartZ=0 EndX=-124.513 EndY=239.188 EndZ=0
    g1: LineSegment StartX=0 StartY=0 StartZ=0 EndX=124.513 EndY=239.188 EndZ=0
    g2: ArcOfCircle CenterX=0 CenterY=0 CenterZ=0 NormalX=0 NormalY=0 NormalZ=1 AngleXU=0 Radius=269.656 StartAngle=1.09083 EndAngle=2.05076
  constraints (7):
    c: Coincident(g0,g-1)
    c: Coincident(g1,g0)
    c: Coincident(g2,g1)
    c: Coincident(g2,g0)
    c: Coincident(g2,g0)
    c: Angle(g1,g0) = 0.959931
    c: Angle(g1,g-2) = 0.479966
FEATURE [Part::Extrusion] Extrude048  label="Extrude052"
  Base = -> Sketch062
  Dir = (1,0,0)
  DirMode = 2
  FaceMakerClass = Part::FaceMakerBullseye
  FaceMakerMode = 3
  LengthFwd = 70
  LengthRev = 0
  Placement = pos=(1455,0,0) rot=(0,0,1;0rad)
  Reversed = true
  Solid = true
  Symmetric = false
  expr: .Placement.Base.x = -25 + Spreadsheet008.l4 - 320
  expr: LengthFwd = Spreadsheet008.l1 - 100
FEATURE [Part::Cut] Cut020
  Base = -> Cut019
  Tool = -> Extrude048
FEATURE [Sketcher::SketchObject] Sketch063
  ArcFitTolerance = 0
  FullyConstrained = true
  MakeInternals = false
  Placement = pos=(0,0,0) rot=(0.57735,0.57735,0.57735;2.0944rad)
  sketch-geometry (6):
    g0: LineSegment [constr] StartX=0 StartY=0 StartZ=0 EndX=247.487 EndY=247.487 EndZ=0
    g1: Circle CenterX=247.487 CenterY=247.487 CenterZ=0 NormalX=0 NormalY=0 NormalZ=1 AngleXU=0 Radius=7.5
    g2: ArcOfCircle CenterX=247.487 CenterY=247.487 CenterZ=0 NormalX=0 NormalY=0 NormalZ=1 AngleXU=0 Radius=20 StartAngle=5.62869 EndAngle=8.50848
    g3: LineSegment StartX=235.312 StartY=263.354 StartZ=0 EndX=74.8903 EndY=140.258 EndZ=0
    g4: LineSegment StartX=263.354 StartY=235.312 StartZ=0 EndX=140.258 EndY=74.8903 EndZ=0
    g5: ArcOfCircle CenterX=0 CenterY=0 CenterZ=0 NormalX=0 NormalY=0 NormalZ=1 AngleXU=0 Radius=159 StartAngle=0.490434 EndAngle=1.08036
  constraints (15):
    c: Coincident(g0,g-1)
    c: Angle(g-1,g0) = 0.785398
    c: Coincident(g1,g0)
    c: Radius(g1) = 7.5
    c: Coincident(g2,g1)
    c: Coincident(g5,g3)
    c: Coincident(g5,g4)
    c: Coincident(g5,g0)
    c: Tangent(g2,g3) = -1.5708
    c: Tangent(g2,g4) = 1.5708
    c: Equal(g4,g3)
    c: Radius(g5) = 159
    c: Angle(g3,g4) = 0.261799
    c: Distance(g5,g1) = 350
    c: Radius(g2) = 20
FEATURE [Part::Extrusion] Extrude049  label="Extrude053"
  Base = -> Sketch063
  Dir = (1,0,0)
  DirMode = 2
  FaceMakerClass = Part::FaceMakerBullseye
  FaceMakerMode = 3
  LengthFwd = 6
  LengthRev = 0
  Placement = pos=(0,0,0) rot=(0,-0.977851,0.209302;0rad)
  Solid = true
  Symmetric = true
FEATURE [App::Part] Part052  label="arm"
  Group = -> [Sketch063,Extrude049]
  Origin = -> Origin078
  Placement = pos=(7490,0,0) rot=(1,0,0;1.8326rad)
  expr: .Placement.Base.x = Spreadsheet008.L0 - Spreadsheet008.l2 + Spreadsheet008.l4 - 330
FEATURE [Sketcher::SketchObject] Sketch064
  ArcFitTolerance = 0
  FullyConstrained = false
  MakeInternals = false
  MapMode = 5
  Placement = pos=(1611,0,0) rot=(0.57735,-0.57735,-0.57735;2.0944rad)
  expr: .Placement.Base.x = -Spreadsheet008.l1 + Spreadsheet008.l4 - 19
  sketch-geometry (1):
    g0: Circle CenterX=0 CenterY=0 CenterZ=0 NormalX=0 NormalY=0 NormalZ=1 AngleXU=0 Radius=159.25
  constraints (1):
    c: Coincident(g0,g-1)
FEATURE [Part::Extrusion] Extrude050  label="Extrude054"
  Base = -> Sketch064
  Dir = (-1,0,0)
  DirMode = 2
  FaceMakerClass = Part::FaceMakerBullseye
  FaceMakerMode = 3
  LengthFwd = 6
  LengthRev = 0
  Placement = pos=(-301,0.8,0) rot=(0,0,1;0rad)
  Solid = true
  Symmetric = false
FEATURE [Part::Feature] Part__Feature029  label="電動トップハンドル_LTKD-01 v5"
  Placement = pos=(0,-389.711,-5.7e-14) rot=(1,0,0;1.5708rad)
  shape: bbox 555.2 x 557.2 x 1150 mm, 73 faces (baked)
FEATURE [App::Part] Part053  label="開閉台"
  Group = -> [Part__Feature029]
  Origin = -> Origin079
  Placement = pos=(0,-400,0) rot=(0,0,1;3.14159rad)
FEATURE [Sketcher::SketchObject] Sketch065
  ArcFitTolerance = 0
  FullyConstrained = false
  MakeInternals = false
  Placement = pos=(0,0,0) rot=(0.57735,0.57735,0.57735;2.0944rad)
  sketch-geometry (5):
    g0: Circle CenterX=0 CenterY=0 CenterZ=0 NormalX=0 NormalY=0 NormalZ=1 AngleXU=0 Radius=7.5
    g1: ArcOfCircle CenterX=0 CenterY=0 CenterZ=0 NormalX=0 NormalY=0 NormalZ=1 AngleXU=0 Radius=20 StartAngle=3.14159 EndAngle=6.28319
    g2: LineSegment StartX=-20 StartY=9.32106e-06 StartZ=0 EndX=-20 EndY=80 EndZ=0
    g3: LineSegment StartX=-20 StartY=80 StartZ=0 EndX=20 EndY=80 EndZ=0
    g4: LineSegment StartX=20 StartY=80 StartZ=0 EndX=20 EndY=3.56439e-05 EndZ=0
  constraints (13):
    c: Coincident(g0,g-1)
    c: Coincident(g1,g0)
    c: Radius(g1) = 20
    c: Radius(g0) = 7.5
    c: Vertical(g2)
    c: Coincident(g2,g3)
    c: Horizontal(g3)
    c: Coincident(g3,g4)
    c: Vertical(g4)
    c: Coincident(g1,g4)
    c: Coincident(g1,g2)
    c: DistanceY(g-1,g3) = 80
    c: DistanceX(g3,g3) = 40
FEATURE [Part::Extrusion] Extrude051  label="Extrude055"
  Base = -> Sketch065
  Dir = (1,0,0)
  DirMode = 2
  FaceMakerClass = Part::FaceMakerBullseye
  FaceMakerMode = 3
  LengthFwd = 40
  LengthRev = 0
  Solid = true
  Symmetric = true
FEATURE [Sketcher::SketchObject] Sketch066
  ArcFitTolerance = 0
  ExternalGeometry = -> [Extrude051]
  FullyConstrained = false
  MakeInternals = false
  MapMode = 5
  Placement = pos=(0,-20,0) rot=(1,0,0;1.5708rad)
  sketch-geometry (4):
    g0: LineSegment StartX=-5 StartY=-25.0355 StartZ=0 EndX=5 EndY=-25.0355 EndZ=0
    g1: LineSegment StartX=5 StartY=-25.0355 StartZ=0 EndX=5 EndY=60 EndZ=0
    g2: LineSegment StartX=5 StartY=60 StartZ=0 EndX=-5 EndY=60 EndZ=0
    g3: LineSegment StartX=-5 StartY=60 StartZ=0 EndX=-5 EndY=-25.0355 EndZ=0
  constraints (11):
    c: Coincident(g0,g1)
    c: Coincident(g1,g2)
    c: Coincident(g2,g3)
    c: Coincident(g3,g0)
    c: Horizontal(g0)
    c: Horizontal(g2)
    c: Vertical(g1)
    c: Vertical(g3)
    c: Distance(g1,g-3) = 20
    c: DistanceX(g0,g0) = 10
    c: DistanceX(g0,g-1) = 5
FEATURE [Part::Extrusion] Extrude052  label="Extrude056"
  Base = -> Sketch066
  Dir = (0,-1,2e-16)
  DirMode = 2
  FaceMakerClass = Part::FaceMakerBullseye
  FaceMakerMode = 3
  LengthFwd = 50
  LengthRev = 0
  Reversed = true
  Solid = true
  Symmetric = false
FEATURE [Part::Cut] Cut021
  Base = -> Extrude051
  Tool = -> Extrude052
FEATURE [Sketcher::SketchObject] Sketch067
  ArcFitTolerance = 0
  FullyConstrained = true
  MakeInternals = false
  MapMode = 5
  Placement = pos=(0,0,80) rot=(0,0,1;0rad)
  sketch-geometry (1):
    g0: Circle CenterX=0 CenterY=0 CenterZ=0 NormalX=0 NormalY=0 NormalZ=1 AngleXU=0 Radius=15
  constraints (2):
    c: Coincident(g0,g-1)
    c: Radius(g0) = 15
FEATURE [Part::Extrusion] Extrude053  label="Extrude057"
  Base = -> Sketch067
  Dir = (0,0,1)
  DirMode = 2
  FaceMakerClass = Part::FaceMakerBullseye
  FaceMakerMode = 3
  LengthFwd = 350
  LengthRev = 0
  Solid = true
  Symmetric = false
FEATURE [Part::FeaturePython] Clone007  label="Cut022"  # Draft clone (typed FeaturePython)
  AttacherType = Attacher::AttachEngine3D
  Fuse = false
  Objects = -> [Cut021]
  Placement = pos=(-1.83e-13,0,510) rot=(0,1,0;3.14159rad)
  Scale = (1,1,1)
FEATURE [App::Part] Part054  label="rod"
  Group = -> [Cut021,Clone007,Sketch066,Sketch065,Sketch067,Extrude051,Extrude052,Extrude053]
  Origin = -> Origin080
  Placement = pos=(7801,-303,175) rot=(1,0,0;6.17882rad)
  expr: .Placement.Base.x = Spreadsheet008.L0 - Spreadsheet008.l2 + Spreadsheet008.l4 - 19
FEATURE [Sketcher::SketchObject] Sketch068
  ArcFitTolerance = 0
  FullyConstrained = false
  MakeInternals = false
  Placement = pos=(0,0,0) rot=(0.57735,0.57735,0.57735;2.0944rad)
  sketch-geometry (5):
    g0: Circle CenterX=0 CenterY=0 CenterZ=0 NormalX=0 NormalY=0 NormalZ=1 AngleXU=0 Radius=7.5
    g1: ArcOfCircle CenterX=0 CenterY=0 CenterZ=0 NormalX=0 NormalY=0 NormalZ=1 AngleXU=0 Radius=20 StartAngle=3.14864 EndAngle=6.2925
    g2: LineSegment StartX=-19.9995 StartY=-0.141043 StartZ=0 EndX=-19.9995 EndY=80 EndZ=0
    g3: LineSegment StartX=-19.9995 StartY=80 StartZ=0 EndX=19.9991 EndY=80 EndZ=0
    g4: LineSegment StartX=19.9991 StartY=80 StartZ=0 EndX=19.9991 EndY=0.186233 EndZ=0
  constraints (12):
    c: Coincident(g0,g-1)
    c: Coincident(g1,g0)
    c: Vertical(g2)
    c: Coincident(g2,g3)
    c: Horizontal(g3)
    c: Coincident(g3,g4)
    c: Vertical(g4)
    c: Coincident(g1,g4)
    c: Coincident(g1,g2)
    c: Radius(g0) = 7.5
    c: Radius(g1) = 20
    c: DistanceY(g-1,g3) = 80
FEATURE [Part::Extrusion] Extrude054  label="Extrude058"
  Base = -> Sketch068
  Dir = (1,0,0)
  DirMode = 2
  FaceMakerClass = Part::FaceMakerBullseye
  FaceMakerMode = 3
  LengthFwd = 9
  LengthRev = 0
  Solid = true
  Symmetric = true
FEATURE [Part::Cylinder] Cylinder  label="円柱"
  Angle = 360
  AttacherType = Attacher::AttachEngine3D
  FirstAngle = 0
  Height = 1061
  Placement = pos=(0,0,80) rot=(0,0,1;0rad)
  Radius = 15
  SecondAngle = 0
  expr: Height = Spreadsheet008.h2
FEATURE [App::Part] Part006  label="rod002"
  Group = -> [Sketch068,Cylinder,Extrude054]
  Origin = -> Origin006
  Placement = pos=(7801,-250,682) rot=(0,0,1;0rad)
  expr: .Placement.Base.x = Spreadsheet008.L0 - Spreadsheet008.l2 + Spreadsheet008.l4 - 19
FEATURE [Part::Compound] Compound003  label="開閉台01"
  Links = -> [Part053]
  Placement = pos=(7801,-250,1061) rot=(0.999778,-0.016584,0;2e-06rad)
  expr: .Placement.Base.x = Spreadsheet008.L0 - Spreadsheet008.l2 + Spreadsheet008.l4 - 19
  expr: .Placement.Base.z = Spreadsheet008.h2
FEATURE [Part::FeaturePython] Straight_tube001  # WARN: FeaturePython — macro-defined, semantics opaque (R4)
  L = 170
  Placement = pos=(1480,0,0) rot=(0,0,1;3.14159rad)
  dia = 16
  fittings = 05_Straight pipe
  material = 0
  standard = 0
  expr: .Placement.Base.x = Spreadsheet008.l4 - 320
  expr: L = Spreadsheet008.l1
FEATURE [Part::Cut] Cut022  label="Cut004"
  Base = -> Straight_tube001
  Refine = true
  Tool = -> Extrude048
FEATURE [App::Part] Part050  label="pipe"
  Group = -> [Sketch060,Revolve014,Part052,Extrude047,Extrude048,Cut020,Cut019,Straight_tube,Array024,Sketch061,Sketch062,Sketch064,Straight_tube001,Cut022,Extrude050]
  Origin = -> Origin076
FEATURE [Part::Compound] Compound001  label="pipeSkimmerBody"
  Links = -> [Part050]
  Placement = pos=(-7.28528e-06,0,0) rot=(0,-0.552174,0.703636;0rad)
  mass = 288.081
FEATURE [App::Part] Part007  label="pipeSkimmerControlDevice"
  Group = -> [Part053,Compound003,Part054,Part006]
  Origin = -> Origin081
  Placement = pos=(-311,0,0) rot=(0,0,1;0rad)
  mass = 120
FEATURE [App::Part] Part051  label="pipeSkimmer"
  Group = -> [Part050,Part049,Spreadsheet008,Compound001,Part007]
  Origin = -> Origin077
  Placement = pos=(107.59,0,4883) rot=(0,0,1;0rad)
FEATURE [Part::FeaturePython] AngleSteel012  label="AngleSteel014"  # WARN: FeaturePython — macro-defined, semantics opaque (R4)
  A = 75
  B = 75
  L = 650
  Placement = pos=(487.5,-325,712.5) rot=(0.57735,-0.57735,-0.57735;4.18879rad)
  Solid = true
  g0 = 7.85
  mass = 4.45263
  size = 10
  standard = SS_Equal
  t = 6
  expr: .Placement.Base.x = Spreadsheet009.H0 - Spreadsheet009.h1 + 37.5
  expr: .Placement.Base.y = -Spreadsheet009.W0 / 2 + 75
  expr: .Placement.Base.z = Spreadsheet009.H0 - 37.5
  expr: L = Spreadsheet009.W0 - 150
FEATURE [Part::FeaturePython] Clone008  label="AngleSteel011"  # Draft clone (typed FeaturePython)
  AttacherType = Attacher::AttachEngine3D
  Fuse = false
  Objects = -> [AngleSteel012]
  Placement = pos=(37.5,-325,262.5) rot=(0.57735,-0.57735,-0.57735;4.18879rad)
  Scale = (1,1,1)
  expr: .Placement.Base.y = -Spreadsheet009.W0 / 2 + 75
  expr: .Placement.Base.z = Spreadsheet009.h1 - 37.5
FEATURE [Part::FeaturePython] Clone009  label="AngleSteel012"  # Draft clone (typed FeaturePython)
  AttacherType = Attacher::AttachEngine3D
  Fuse = false
  Objects = -> [AngleSteel012]
  Placement = pos=(37.5,-325,37.5) rot=(-1,0,0;1.5708rad)
  Scale = (1,1,1)
  expr: .Placement.Base.y = -Spreadsheet009.W0 / 2 + 75
FEATURE [Part::FeaturePython] Clone010  label="AngleSteel006"  # Draft clone (typed FeaturePython)
  AttacherType = Attacher::AttachEngine3D
  Fuse = false
  Objects = -> [AngleSteel012]
  Placement = pos=(7062.5,-325,37.54) rot=(0.57735,0.57735,0.57735;4.18879rad)
  Scale = (1,1,1)
  expr: .Placement.Base.x = Spreadsheet009.L0 - 37.5
  expr: .Placement.Base.y = -Spreadsheet009.W0 / 2 + 75
FEATURE [Part::FeaturePython] Clone011  label="AngleSteel005"  # Draft clone (typed FeaturePython)
  AttacherType = Attacher::AttachEngine3D
  Fuse = false
  Objects = -> [AngleSteel012]
  Placement = pos=(487.5,-325,37.5) rot=(-1,0,0;1.5708rad)
  Scale = (1,1,1)
  expr: .Placement.Base.x = Spreadsheet009.H0 - Spreadsheet009.h1 + 37.5
  expr: .Placement.Base.y = -Spreadsheet009.W0 / 2 + 75
FEATURE [Part::FeaturePython] Array025  label="bottmMember"  # Draft array (typed FeaturePython)
  AlwaysSyncPlacement = false
  Angle = 360
  ArrayType = 0
  Axis = (0,0,1)
  Base = -> Clone011
  Center = (0,0,0)
  Count = 10
  ExpandArray = false
  Fuse = false
  IntervalAxis = (0,0,0)
  IntervalX = (680.556,0,0)
  IntervalY = (0,100,0)
  IntervalZ = (0,0,100)
  NumberCircles = 3
  NumberPolar = 5
  NumberX = 10
  NumberY = 1
  NumberZ = 1
  PlacementList = 10 placements: arithmetic series from (487.5,-325,37.5) step (680.556,0,0) to (6612.5,-325,37.5)
  RadialDistance = 50
  ScaleList = (10) [(1,1,1),(1,1,1),(1,1,1),(1,1,1),(1,1,1),(1,1,1),(1,1,1),(1,1,1),(1,1,1),(1,1,1)]
  Symmetry = 1
  TangentialDistance = 25
  expr: .IntervalX.x = Spreadsheet009.p0
  expr: NumberX = Spreadsheet009.n0
FEATURE [Part::FeaturePython] Clone012  label="AngleSteel013"  # Draft clone (typed FeaturePython)
  AttacherType = Attacher::AttachEngine3D
  Fuse = false
  Objects = -> [AngleSteel012]
  Placement = pos=(6612.5,-325,712.5) rot=(0,0.707107,0.707107;3.14159rad)
  Scale = (1,1,1)
  expr: .Placement.Base.x = Spreadsheet009.L0 - (Spreadsheet009.H0 - Spreadsheet009.h1) - 37.5
  expr: .Placement.Base.y = -Spreadsheet009.W0 / 2 + 75
  expr: .Placement.Base.z = Spreadsheet009.H0 - 37.5
FEATURE [Part::FeaturePython] Array026  label="topMember"  # Draft array (typed FeaturePython)
  AlwaysSyncPlacement = false
  Angle = 360
  ArrayType = 0
  Axis = (0,0,1)
  Base = -> AngleSteel012
  Center = (0,0,0)
  Count = 9
  ExpandArray = false
  Fuse = false
  IntervalAxis = (0,0,0)
  IntervalX = (680.556,0,0)
  IntervalY = (0,100,0)
  IntervalZ = (0,0,100)
  NumberCircles = 3
  NumberPolar = 5
  NumberX = 9
  NumberY = 1
  NumberZ = 1
  PlacementList = 9 placements: arithmetic series from (487.5,-325,712.5) step (680.556,0,0) to (5931.94,-325,712.5)
  RadialDistance = 50
  ScaleList = (9) [(1,1,1),(1,1,1),(1,1,1),(1,1,1),(1,1,1),(1,1,1),(1,1,1),(1,1,1),(1,1,1)]
  Symmetry = 1
  TangentialDistance = 25
  expr: .IntervalX.x = <<Spreadsheet009>>.p0
  expr: NumberX = Spreadsheet009.n0 - 1
FEATURE [Sketcher::SketchObject] Sketch070
  ArcFitTolerance = 0
  FullyConstrained = false
  MakeInternals = false
  Placement = pos=(0,0,0) rot=(1,0,0;1.5708rad)
  sketch-geometry (7):
    g0: LineSegment StartX=0 StartY=36.614 StartZ=0 EndX=0 EndY=161.614 EndZ=0
    g1: LineSegment StartX=0 StartY=161.614 StartZ=0 EndX=-30 EndY=161.614 EndZ=0
    g2: LineSegment StartX=-30 StartY=161.614 StartZ=0 EndX=-95.0179 EndY=130.728 EndZ=0
    g3: ArcOfCircle CenterX=-80 CenterY=99.114 CenterZ=0 NormalX=0 NormalY=0 NormalZ=1 AngleXU=0 Radius=35 StartAngle=2.01427 EndAngle=4.26891
    g4: LineSegment StartX=-95.0179 StartY=67.4997 StartZ=0 EndX=-30 EndY=36.614 EndZ=0
    g5: LineSegment StartX=-30 StartY=36.614 StartZ=0 EndX=0 EndY=36.614 EndZ=0
    g6: Circle CenterX=-80 CenterY=99.114 CenterZ=0 NormalX=0 NormalY=0 NormalZ=1 AngleXU=0 Radius=15
  constraints (18):
    c: Vertical(g0)
    c: Coincident(g0,g1)
    c: Horizontal(g1)
    c: Coincident(g1,g2)
    c: Tangent(g2,g3) = -1.5708
    c: Coincident(g4,g5)
    c: Coincident(g5,g0)
    c: Coincident(g6,g3)
    c: Horizontal(g5)
    c: PointOnObject(g0,g-2)
    c: DistanceY(g0,g0) = 125
    c: Equal(g1,g5)
    c: DistanceX(g1,g1) = 30
    c: Tangent(g3,g4) = -1.5708
    c: Distance(g3,g0) = 80
    c: Radius(g6) = 15
    c: Radius(g3) = 35
    c: Equal(g2,g4)
FEATURE [Part::Extrusion] Extrude056  label="bracketBottom"
  Base = -> Sketch070
  Dir = (0,-1,2e-16)
  DirMode = 2
  FaceMakerClass = Part::FaceMakerBullseye
  FaceMakerMode = 3
  LengthFwd = 16
  LengthRev = 0
  Reversed = true
  Solid = true
  Symmetric = false
FEATURE [Part::FeaturePython] AngleSteel013  label="AngleSteel002"  # WARN: FeaturePython — macro-defined, semantics opaque (R4)
  A = 75
  B = 75
  L = 972.747
  Placement = pos=(471.291,-37.5,728.865) rot=(0,1,0;2.35256rad)
  Solid = true
  g0 = 7.85
  mass = 6.66352
  size = 10
  standard = SS_Equal
  t = 6
  expr: .Placement.Base.x = Spreadsheet009.H0 - Spreadsheet009.h1 + Spreadsheet009.lx
  expr: .Placement.Base.z = Spreadsheet009.H0 - Spreadsheet009.lz
  expr: .Placement.Rotation.Angle = Spreadsheet009.sita + 90
  expr: L = Spreadsheet009.l2 - 40
FEATURE [Part::FeaturePython] Array027  label="diagonalMember"  # Draft array (typed FeaturePython)
  AlwaysSyncPlacement = false
  Angle = 360
  ArrayType = 0
  Axis = (0,0,1)
  Base = -> AngleSteel013
  Center = (0,0,0)
  Count = 9
  ExpandArray = false
  Fuse = false
  IntervalAxis = (0,0,0)
  IntervalX = (680.556,0,0)
  IntervalY = (0,100,0)
  IntervalZ = (0,0,100)
  NumberCircles = 3
  NumberPolar = 5
  NumberX = 9
  NumberY = 1
  NumberZ = 1
  PlacementList = 9 placements: arithmetic series from (471.291,-37.5,728.865) step (680.556,0,0) to (5915.74,-37.5,728.865)
  RadialDistance = 50
  ScaleList = (9) [(1,1,1),(1,1,1),(1,1,1),(1,1,1),(1,1,1),(1,1,1),(1,1,1),(1,1,1),(1,1,1)]
  Symmetry = 1
  TangentialDistance = 25
  expr: .IntervalX.x = Spreadsheet009.p0
  expr: NumberX = Spreadsheet009.n0 - 1
FEATURE [Part::FeaturePython] AngleSteel014  label="AngleSteel015"  # WARN: FeaturePython — macro-defined, semantics opaque (R4)
  A = 75
  B = 75
  L = 720
  Placement = pos=(487.5,43.5,15) rot=(0,0,1;1.5708rad)
  Solid = true
  g0 = 7.85
  mass = 4.93215
  size = 10
  standard = SS_Equal
  t = 6
  expr: .Placement.Base.x = Spreadsheet009.H0 - Spreadsheet009.h1 + 37.5
  expr: L = Spreadsheet009.H0 - 30
FEATURE [Part::FeaturePython] Array028  label="verticalMember"  # Draft array (typed FeaturePython)
  AlwaysSyncPlacement = false
  Angle = 360
  ArrayType = 0
  Axis = (0,0,1)
  Base = -> AngleSteel014
  Center = (0,0,0)
  Count = 10
  ExpandArray = false
  Fuse = false
  IntervalAxis = (0,0,0)
  IntervalX = (680.556,0,0)
  IntervalY = (0,100,0)
  IntervalZ = (0,0,100)
  NumberCircles = 3
  NumberPolar = 5
  NumberX = 10
  NumberY = 1
  NumberZ = 1
  PlacementList = 10 placements: arithmetic series from (487.5,43.5,15) step (680.556,0,0) to (6612.5,43.5,15)
  RadialDistance = 50
  ScaleList = (10) [(1,1,1),(1,1,1),(1,1,1),(1,1,1),(1,1,1),(1,1,1),(1,1,1),(1,1,1),(1,1,1),(1,1,1)]
  Symmetry = 1
  TangentialDistance = 25
  expr: .IntervalX.x = Spreadsheet009.p0
  expr: NumberX = Spreadsheet009.n0
FEATURE [Sketcher::SketchObject] Sketch071
  ArcFitTolerance = 0
  AttachmentSupport = -> [XZ_Plane083]
  FullyConstrained = true
  MakeInternals = false
  MapMode = 5
  Placement = pos=(0,0,0) rot=(1,0,0;1.5708rad)
  expr: Constraints[12] = Spreadsheet009.L0
  expr: Constraints[15] = Spreadsheet009.h1
  expr: Constraints[16] = Spreadsheet009.H0
  sketch-geometry (6):
    g0: LineSegment StartX=0 StartY=0 StartZ=0 EndX=0 EndY=300 EndZ=0
    g1: LineSegment StartX=0 StartY=300 StartZ=0 EndX=450 EndY=750 EndZ=0
    g2: LineSegment StartX=450 StartY=750 StartZ=0 EndX=6650 EndY=750 EndZ=0
    g3: LineSegment StartX=6650 StartY=750 StartZ=0 EndX=7100 EndY=300 EndZ=0
    g4: LineSegment StartX=7100 StartY=300 StartZ=0 EndX=7100 EndY=0 EndZ=0
    g5: LineSegment StartX=7100 StartY=0 StartZ=0 EndX=0 EndY=0 EndZ=0
  constraints (18):
    c: PointOnObject(g0,g-2)
    c: PointOnObject(g0,g-2)
    c: Coincident(g0,g1)
    c: Coincident(g1,g2)
    c: Horizontal(g2)
    c: Coincident(g2,g3)
    c: Coincident(g3,g4)
    c: PointOnObject(g4,g-1)
    c: Vertical(g4)
    c: Coincident(g4,g5)
    c: Coincident(g5,g0)
    c: Horizontal(g5)
    c: Distance(g5) = 7100
    c: Angle(g-2,g1) = 2.35619
    c: Angle(g2,g3) = 2.35619
    c: DistanceY(g0,g0) = 300
    c: Distance(g2,g5) = 750
    c: Equal(g4,g0)
FEATURE [Sketcher::SketchObject] Sketch069
  ArcFitTolerance = 0
  ExternalGeometry = -> [Sketch071,AngleSteel012]
  FullyConstrained = true
  MakeInternals = false
  Placement = pos=(0,0,0) rot=(1,0,0;1.5708rad)
  expr: Constraints[12] = (Spreadsheet009.L0 - (Spreadsheet009.H0 - Spreadsheet009.h1)) / (Spreadsheet009.n0 - 1) - 150
  sketch-geometry (6):
    g0: LineSegment StartX=1238.89 StartY=750 StartZ=0 EndX=1238.89 EndY=780 EndZ=0
    g1: LineSegment StartX=1238.89 StartY=780 StartZ=0 EndX=1093.59 EndY=878.931 EndZ=0
    g2: ArcOfCircle CenterX=1073.89 CenterY=850 CenterZ=0 NormalX=0 NormalY=0 NormalZ=1 AngleXU=0 Radius=35 StartAngle=0.97303 EndAngle=3.14159
    g3: Circle CenterX=1073.89 CenterY=850 CenterZ=0 NormalX=0 NormalY=0 NormalZ=1 AngleXU=0 Radius=15
    g4: LineSegment StartX=1038.89 StartY=850 StartZ=0 EndX=1038.89 EndY=750 EndZ=0
    g5: LineSegment StartX=1038.89 StartY=750 StartZ=0 EndX=1238.89 EndY=750 EndZ=0
  constraints (16):
    c: Coincident(g0,g1)
    c: Tangent(g1,g2) = -1.5708
    c: Coincident(g3,g2)
    c: Vertical(g0)
    c: DistanceY(g0,g0) = 30
    c: Radius(g3) = 15
    c: Radius(g2) = 35
    c: DistanceX(g2,g0) = 200
    c: PointOnObject(g4,g-3)
    c: PointOnObject(g0,g-3)
    c: Coincident(g5,g4)
    c: Coincident(g5,g0)
    c: DistanceX(g-4,g4) = 588.889
    c: Vertical(g4)
    c: Tangent(g4,g2) = -1.5708
    c: DistanceY(g4,g2) = 100
FEATURE [Part::Extrusion] Extrude055  label="bracketTop"
  Base = -> Sketch069
  Dir = (0,-1,2e-16)
  DirMode = 2
  FaceMakerClass = Part::FaceMakerBullseye
  FaceMakerMode = 3
  LengthFwd = 16
  LengthRev = 0
  Reversed = true
  Solid = true
  Symmetric = false
FEATURE [Spreadsheet::Sheet] Spreadsheet009
  cells = A2='L0; B2(L0)=7100; A3='H0; B3(H0)=750; A4='h1; B4(h1)=300; A5='W0; B5(W0)=800; A6='div n0; B6(n0)=10; A7='p0; B7(p0)=680.555555555556; A8='sita; B8(sita)=44.7918766079527; A9='l2; B9(l2)=1012.74669300745; A10='lx; B10(lx)=21.2913359841632; A11='lz; B11(lz)=21.1347820431032; A12='beta; B12(beta)=5.7; A13='picketFence  pl; B13(pk)=1000; A14='bradePosition br; B14(br)=800; A15='no of brade n0; B15(n00)=7; A16='bradeSpacing; B16(brs)=960
FEATURE [Part::FeaturePython] AngleSteel015  label="AngleSteel016"  # WARN: FeaturePython — macro-defined, semantics opaque (R4)
  A = 75
  B = 75
  L = 1000
  Placement = pos=(0,0,0) rot=(0,0,1;1.5708rad)
  Solid = false
  g0 = 7.85
  mass = 0
  size = 10
  standard = SS_Equal
  t = 6
FEATURE [Part::Sweep] Sweep009  label="mainMaterial"
  Frenet = false
  Sections = -> [AngleSteel015]
  Solid = true
  Spine = -> Sketch071 [Edge6,Edge5,Edge4,Edge3,Edge2,Edge1]
  Transition = 1
FEATURE [Part::Compound] Compound054  label="rake"
  Links = -> [Sweep009,Array028,Array027,Extrude056,Extrude055]
  Placement = pos=(0,-400,0) rot=(0,0,1;0rad)
  expr: .Placement.Base.y = -Spreadsheet009.W0 / 2
FEATURE [Part::Mirroring] Mirror019  label="rake001"
  Base = (0,-8.88e-14,400)
  Normal = (0,-1,0)
  Source = -> Compound054
FEATURE [Part::FeaturePython] AngleSteel016  label="AngleSteel017"  # WARN: FeaturePython — macro-defined, semantics opaque (R4)
  A = 50
  B = 50
  L = 200
  Placement = pos=(25,0,0) rot=(0,0,1;0rad)
  Solid = true
  g0 = 7.85
  mass = 0.88607
  size = 7
  standard = SS_Equal
  t = 6
FEATURE [Sketcher::SketchObject] Sketch072
  ArcFitTolerance = 0
  FullyConstrained = false
  MakeInternals = false
  Placement = pos=(0,0,0) rot=(1,0,0;1.5708rad)
  expr: Constraints[6] = Spreadsheet009.beta
  sketch-geometry (3):
    g0: LineSegment StartX=0 StartY=0 StartZ=0 EndX=64.1183 EndY=6.39986 EndZ=0
    g1: LineSegment StartX=64.1183 StartY=6.39986 StartZ=0 EndX=64.1183 EndY=0 EndZ=0
    g2: LineSegment StartX=64.1183 StartY=0 StartZ=0 EndX=0 EndY=0 EndZ=0
  constraints (7):
    c: Coincident(g-1,g0)
    c: Coincident(g0,g1)
    c: Vertical(g1)
    c: Coincident(g1,g2)
    c: Coincident(g2,g0)
    c: Horizontal(g2)
    c: Angle(g2,g0) = 0.0994838
FEATURE [Part::Extrusion] Extrude057  label="Extrude059"
  Base = -> Sketch072
  Dir = (0,-1,2e-16)
  DirMode = 2
  FaceMakerClass = Part::FaceMakerBullseye
  FaceMakerMode = 3
  LengthFwd = 50
  LengthRev = 0
  Solid = true
  Symmetric = true
FEATURE [Part::Cut] Cut023
  Base = -> AngleSteel016
  Placement = pos=(450,0,750) rot=(0,1,0;0.099484rad)
  Tool = -> Extrude057
  expr: .Placement.Base.x = Spreadsheet009.H0 - Spreadsheet009.h1
  expr: .Placement.Base.z = Spreadsheet009.H0
FEATURE [Part::FeaturePython] Array029  label="picketFenceReciever"  # Draft array (typed FeaturePython)
  AlwaysSyncPlacement = false
  Angle = 360
  ArrayType = 0
  Axis = (0,0,1)
  Base = -> Cut023
  Center = (0,0,0)
  Count = 10
  ExpandArray = false
  Fuse = false
  IntervalAxis = (0,0,0)
  IntervalX = (680.556,0,0)
  IntervalY = (0,100,0)
  IntervalZ = (0,0,100)
  NumberCircles = 3
  NumberPolar = 5
  NumberX = 10
  NumberY = 1
  NumberZ = 1
  PlacementList = 10 placements: arithmetic series from (450,0,750) step (680.556,0,0) to (6575,0,750)
  RadialDistance = 50
  ScaleList = (10) [(1,1,1),(1,1,1),(1,1,1),(1,1,1),(1,1,1),(1,1,1),(1,1,1),(1,1,1),(1,1,1),(1,1,1)]
  Symmetry = 1
  TangentialDistance = 25
  expr: .IntervalX.x = Spreadsheet009.p0
  expr: NumberX = Spreadsheet009.n0
FEATURE [Part::FeaturePython] AngleSteel017  label="AngleSteel018"  # WARN: FeaturePython — macro-defined, semantics opaque (R4)
  A = 50
  B = 50
  L = 1500
  Placement = pos=(25,0,0) rot=(0,0,1;1.5708rad)
  Solid = true
  g0 = 7.85
  mass = 6.64552
  size = 7
  standard = SS_Equal
  t = 6
FEATURE [App::Part] Part057  label="Part001"
  Group = -> [AngleSteel017]
  Origin = -> Origin084
  Placement = pos=(450.993,50,760) rot=(0,1,0;0.099484rad)
  expr: .Placement.Base.x = Spreadsheet009.H0 - Spreadsheet009.h1 + 10 * sin(Spreadsheet009.beta)
  expr: .Placement.Base.z = Spreadsheet009.H0 + 10
FEATURE [Part::FeaturePython] Array030  # Draft array (typed FeaturePython)
  AlwaysSyncPlacement = false
  Angle = 360
  ArrayType = 0
  Axis = (0,0,1)
  Base = -> Part057
  Center = (0,0,0)
  Count = 10
  ExpandArray = false
  Fuse = false
  IntervalAxis = (0,0,0)
  IntervalX = (680.556,0,0)
  IntervalY = (0,100,0)
  IntervalZ = (0,0,100)
  NumberCircles = 3
  NumberPolar = 5
  NumberX = 10
  NumberY = 1
  NumberZ = 1
  PlacementList = 10 placements: arithmetic series from (450.993,50,760) step (680.556,0,0) to (6575.99,50,760)
  RadialDistance = 50
  ScaleList = (10) [(1,1,1),(1,1,1),(1,1,1),(1,1,1),(1,1,1),(1,1,1),(1,1,1),(1,1,1),(1,1,1),(1,1,1)]
  Symmetry = 1
  TangentialDistance = 25
  expr: .IntervalX.x = Spreadsheet009.p0
  expr: NumberX = Spreadsheet009.n0
FEATURE [Sketcher::SketchObject] Sketch073
  ArcFitTolerance = 0
  FullyConstrained = true
  MakeInternals = false
  Placement = pos=(0,0,0) rot=(1,0,0;1.5708rad)
  expr: Constraints[11] = Spreadsheet009.beta
  expr: Constraints[1] = Spreadsheet009.H0 + Spreadsheet009.pk / cos(Spreadsheet009.beta)
  expr: Constraints[2] = Spreadsheet009.H0 - Spreadsheet009.h1 + (Spreadsheet009.pk + 10) * sin(Spreadsheet009.beta) - 20
  expr: Constraints[3] = Spreadsheet009.L0
  sketch-geometry (4):
    g0: LineSegment StartX=530.313 StartY=1754.97 StartZ=0 EndX=7630.31 EndY=1046.29 EndZ=0
    g1: LineSegment StartX=7630.31 StartY=1046.29 StartZ=0 EndX=7630.31 EndY=2554.97 EndZ=0
    g2: LineSegment StartX=530.313 StartY=1754.97 StartZ=0 EndX=530.313 EndY=2554.97 EndZ=0
    g3: LineSegment StartX=530.313 StartY=2554.97 StartZ=0 EndX=7630.31 EndY=2554.97 EndZ=0
  constraints (12):
    c: Coincident(g0,g1)
    c: DistanceY(g-1,g0) = 1754.97
    c: DistanceX(g-1,g0) = 530.313
    c: DistanceX(g0,g1) = 7100
    c: Vertical(g1)
    c: Coincident(g0,g2)
    c: Vertical(g2)
    c: Coincident(g2,g3)
    c: Horizontal(g3)
    c: Coincident(g1,g3)
    c: DistanceY(g2,g2) = 800
    c: Angle(g0,g3) = 0.0994838
FEATURE [Part::Extrusion] Extrude058  label="Extrude060"
  Base = -> Sketch073
  Dir = (0,-1,2e-16)
  DirMode = 2
  FaceMakerClass = Part::FaceMakerBullseye
  FaceMakerMode = 3
  LengthFwd = 200
  LengthRev = 0
  Solid = true
  Symmetric = true
FEATURE [Part::Cut] Cut024  label="picketFence"
  Base = -> Array030
  Tool = -> Extrude058
FEATURE [App::Part] Part056  label="RakeArm"
  Group = -> [AngleSteel015,Sketch071,Sweep009,AngleSteel014,Array028,AngleSteel013,Array027,Sketch070,Extrude056,Sketch069,Extrude055,Compound054,Mirror019,AngleSteel012,Array026,Clone012,Clone011,Array025,Clone010,Clone009,Clone008,Sketch072,Extrude057,AngleSteel016,Cut023,Array029,Part057,Array030,Sketch073,Extrude058,Cut024]
  Origin = -> Origin083
FEATURE [Part::FeaturePython] AngleSteel006  label="AngleSteel019"  # WARN: FeaturePython — macro-defined, semantics opaque (R4)
  A = 75
  B = 75
  L = 1000
  Placement = pos=(0,0,0) rot=(0.707107,0.707107,0;3.14159rad)
  Solid = false
  g0 = 7.85
  mass = 0
  size = 10
  standard = SS_Equal
  t = 6
FEATURE [Part::Extrusion] Extrude059  label="Extrude061"
  Base = -> AngleSteel006
  Dir = (1,-2e-16,1e-16)
  DirMode = 2
  FaceMakerClass = Part::FaceMakerBullseye
  FaceMakerMode = 3
  LengthFwd = 1600
  LengthRev = 0
  Solid = false
  Symmetric = true
FEATURE [Sketcher::SketchObject] Sketch074
  ArcFitTolerance = 0
  AttachmentSupport = -> [Extrude059]
  ExternalGeometry = -> [Extrude059]
  FullyConstrained = false
  MakeInternals = false
  MapMode = 5
  Placement = pos=(0,1.6e-15,0) rot=(1,0,0;1.5708rad)
  sketch-geometry (8):
    g0: Circle CenterX=-700 CenterY=-40.4478 CenterZ=0 NormalX=0 NormalY=0 NormalZ=1 AngleXU=0 Radius=7
    g1: Circle CenterX=700 CenterY=-39.6228 CenterZ=0 NormalX=0 NormalY=0 NormalZ=1 AngleXU=0 Radius=7
    g2: Circle CenterX=-500 CenterY=-40.4478 CenterZ=0 NormalX=0 NormalY=0 NormalZ=1 AngleXU=0 Radius=7
    g3: Circle CenterX=-299.492 CenterY=-40.4478 CenterZ=0 NormalX=0 NormalY=0 NormalZ=1 AngleXU=0 Radius=7
    g4: Circle CenterX=-99.2385 CenterY=-40.4478 CenterZ=0 NormalX=0 NormalY=0 NormalZ=1 AngleXU=0 Radius=7
    g5: Circle CenterX=101.015 CenterY=-40.4478 CenterZ=0 NormalX=0 NormalY=0 NormalZ=1 AngleXU=0 Radius=7
    g6: Circle CenterX=301.269 CenterY=-40.4478 CenterZ=0 NormalX=0 NormalY=0 NormalZ=1 AngleXU=0 Radius=7
    g7: Circle CenterX=501.523 CenterY=-40.4478 CenterZ=0 NormalX=0 NormalY=0 NormalZ=1 AngleXU=0 Radius=7
  constraints (11):
    c: Diameter(g0) = 14
    c: Diameter(g1) = 14
    c: DistanceX(g-3,g0) = 100
    c: DistanceX(g1,g-4) = 100
    c: Equal(g0,g2) = 14
    c: Equal(g0,g3) = 14
    c: Equal(g0,g4) = 14
    c: Equal(g0,g5) = 14
    c: Equal(g0,g6) = 14
    c: Equal(g0,g7) = 14
    c: DistanceX(g0,g2) = 200
FEATURE [Part::Extrusion] Extrude060  label="Extrude062"
  Base = -> Sketch074
  Dir = (0,-1,2e-16)
  DirMode = 2
  FaceMakerClass = Part::FaceMakerBullseye
  FaceMakerMode = 3
  LengthFwd = 10
  LengthRev = 0
  Reversed = true
  Solid = true
  Symmetric = false
FEATURE [Part::Cut] Cut025  label="angle"
  Base = -> Extrude059
  Tool = -> Extrude060
FEATURE [Sketcher::SketchObject] Sketch075
  ArcFitTolerance = 0
  FullyConstrained = false
  MakeInternals = false
  Placement = pos=(0,0,0) rot=(1,0,0;1.5708rad)
  sketch-geometry (67):
    g0: LineSegment StartX=-800 StartY=-70 StartZ=0 EndX=-800 EndY=70 EndZ=0
    g1: LineSegment StartX=-800 StartY=70 StartZ=0 EndX=800 EndY=70 EndZ=0
    g2: LineSegment StartX=800 StartY=70 StartZ=0 EndX=800 EndY=-70 EndZ=0
    g3: LineSegment StartX=800 StartY=-70 StartZ=0 EndX=-800 EndY=-70 EndZ=0
    g4: GeomPoint [constr] X=0 Y=0 Z=0
    g5: Circle CenterX=-700 CenterY=40 CenterZ=0 NormalX=0 NormalY=0 NormalZ=1 AngleXU=0 Radius=7
    g6: Circle CenterX=100 CenterY=40 CenterZ=0 NormalX=0 NormalY=0 NormalZ=1 AngleXU=0 Radius=7
    g7: Circle CenterX=-500 CenterY=40 CenterZ=0 NormalX=0 NormalY=0 NormalZ=1 AngleXU=0 Radius=7
    g8: Circle CenterX=-300 CenterY=40 CenterZ=0 NormalX=0 NormalY=0 NormalZ=1 AngleXU=0 Radius=7
    g9: Circle CenterX=-100 CenterY=40 CenterZ=0 NormalX=0 NormalY=0 NormalZ=1 AngleXU=0 Radius=7
    g10: Circle CenterX=300 CenterY=40 CenterZ=0 NormalX=0 NormalY=0 NormalZ=1 AngleXU=0 Radius=7
    g11: Circle CenterX=500 CenterY=40 CenterZ=0 NormalX=0 NormalY=0 NormalZ=1 AngleXU=0 Radius=7
    g12: Circle CenterX=700 CenterY=40 CenterZ=0 NormalX=0 NormalY=0 NormalZ=1 AngleXU=0 Radius=7
    g13: LineSegment StartX=-743 StartY=5 StartZ=0 EndX=-743 EndY=-45 EndZ=0
    g14: ArcOfCircle CenterX=-750 CenterY=-45 CenterZ=0 NormalX=0 NormalY=0 NormalZ=1 AngleXU=0 Radius=7 StartAngle=3.14159 EndAngle=6.28319
    g15: LineSegment StartX=-757 StartY=-45 StartZ=0 EndX=-757 EndY=5 EndZ=0
    g16: ArcOfCircle CenterX=-750 CenterY=5 CenterZ=0 NormalX=0 NormalY=0 NormalZ=1 AngleXU=0 Radius=7 StartAngle=2e-16 EndAngle=3.14159
    g17: LineSegment StartX=-593 StartY=5 StartZ=0 EndX=-593 EndY=-45 EndZ=0
    g18: ArcOfCircle CenterX=-600 CenterY=-45 CenterZ=0 NormalX=0 NormalY=0 NormalZ=1 AngleXU=0 Radius=7 StartAngle=3.14159 EndAngle=6.28319
    g19: LineSegment StartX=-607 StartY=-45 StartZ=0 EndX=-607 EndY=5 EndZ=0
    g20: ArcOfCircle CenterX=-600 CenterY=5 CenterZ=0 NormalX=0 NormalY=0 NormalZ=1 AngleXU=0 Radius=7 StartAngle=1e-16 EndAngle=3.14159
    g21: LineSegment [constr] StartX=-743 StartY=5 StartZ=0 EndX=-593 EndY=5 EndZ=0
    g22: LineSegment StartX=-443 StartY=5 StartZ=0 EndX=-443 EndY=-45 EndZ=0
    g23: ArcOfCircle CenterX=-450 CenterY=-45 CenterZ=0 NormalX=0 NormalY=0 NormalZ=1 AngleXU=0 Radius=7 StartAngle=3.14159 EndAngle=6.28319
    g24: LineSegment StartX=-457 StartY=-45 StartZ=0 EndX=-457 EndY=5 EndZ=0
    g25: ArcOfCircle CenterX=-450 CenterY=5 CenterZ=0 NormalX=0 NormalY=0 NormalZ=1 AngleXU=0 Radius=7 StartAngle=1e-16 EndAngle=3.14159
    g26: LineSegment [constr] StartX=-593 StartY=5 StartZ=0 EndX=-443 EndY=5 EndZ=0
    g27: LineSegment StartX=-293 StartY=5 StartZ=0 EndX=-293 EndY=-45 EndZ=0
    g28: ArcOfCircle CenterX=-300 CenterY=-45 CenterZ=0 NormalX=0 NormalY=0 NormalZ=1 AngleXU=0 Radius=7 StartAngle=3.14159 EndAngle=6.28319
    g29: LineSegment StartX=-307 StartY=-45 StartZ=0 EndX=-307 EndY=5 EndZ=0
    g30: ArcOfCircle CenterX=-300 CenterY=5 CenterZ=0 NormalX=0 NormalY=0 NormalZ=1 AngleXU=0 Radius=7 StartAngle=1e-16 EndAngle=3.14159
    g31: LineSegment [constr] StartX=-443 StartY=5 StartZ=0 EndX=-293 EndY=5 EndZ=0
    g32: LineSegment StartX=-143 StartY=5 StartZ=0 EndX=-143 EndY=-45 EndZ=0
    g33: ArcOfCircle CenterX=-150 CenterY=-45 CenterZ=0 NormalX=0 NormalY=0 NormalZ=1 AngleXU=0 Radius=7 StartAngle=3.14159 EndAngle=6.28319
    g34: LineSegment StartX=-157 StartY=-45 StartZ=0 EndX=-157 EndY=5 EndZ=0
    g35: ArcOfCircle CenterX=-150 CenterY=5 CenterZ=0 NormalX=0 NormalY=0 NormalZ=1 AngleXU=0 Radius=7 StartAngle=1e-16 EndAngle=3.14159
    g36: LineSegment [constr] StartX=-293 StartY=5 StartZ=0 EndX=-143 EndY=5 EndZ=0
    g37: LineSegment StartX=7 StartY=5 StartZ=0 EndX=7 EndY=-45 EndZ=0
    g38: ArcOfCircle CenterX=-3.42e-14 CenterY=-45 CenterZ=0 NormalX=0 NormalY=0 NormalZ=1 AngleXU=0 Radius=7 StartAngle=3.14159 EndAngle=6.28319
    g39: LineSegment StartX=-7 StartY=-45 StartZ=0 EndX=-7 EndY=5 EndZ=0
    g40: ArcOfCircle CenterX=-3.42e-14 CenterY=5 CenterZ=0 NormalX=0 NormalY=0 NormalZ=1 AngleXU=0 Radius=7 StartAngle=1e-16 EndAngle=3.14159
    g41: LineSegment [constr] StartX=-143 StartY=5 StartZ=0 EndX=7 EndY=5 EndZ=0
    g42: LineSegment StartX=157 StartY=5 StartZ=0 EndX=157 EndY=-45 EndZ=0
    g43: ArcOfCircle CenterX=150 CenterY=-45 CenterZ=0 NormalX=0 NormalY=0 NormalZ=1 AngleXU=0 Radius=7 StartAngle=3.14159 EndAngle=6.28319
    g44: LineSegment StartX=143 StartY=-45 StartZ=0 EndX=143 EndY=5 EndZ=0
    g45: ArcOfCircle CenterX=150 CenterY=5 CenterZ=0 NormalX=0 NormalY=0 NormalZ=1 AngleXU=0 Radius=7 StartAngle=1e-16 EndAngle=3.14159
    g46: LineSegment [constr] StartX=7 StartY=5 StartZ=0 EndX=157 EndY=5 EndZ=0
    g47: LineSegment StartX=307 StartY=5 StartZ=0 EndX=307 EndY=-45 EndZ=0
    g48: ArcOfCircle CenterX=300 CenterY=-45 CenterZ=0 NormalX=0 NormalY=0 NormalZ=1 AngleXU=0 Radius=7 StartAngle=3.14159 EndAngle=6.28319
    g49: LineSegment StartX=293 StartY=-45 StartZ=0 EndX=293 EndY=5 EndZ=0
    g50: ArcOfCircle CenterX=300 CenterY=5 CenterZ=0 NormalX=0 NormalY=0 NormalZ=1 AngleXU=0 Radius=7 StartAngle=1e-16 EndAngle=3.14159
    g51: LineSegment [constr] StartX=157 StartY=5 StartZ=0 EndX=307 EndY=5 EndZ=0
    g52: LineSegment StartX=457 StartY=5 StartZ=0 EndX=457 EndY=-45 EndZ=0
    g53: ArcOfCircle CenterX=450 CenterY=-45 CenterZ=0 NormalX=0 NormalY=0 NormalZ=1 AngleXU=0 Radius=7 StartAngle=3.14159 EndAngle=6.28319
    g54: LineSegment StartX=443 StartY=-45 StartZ=0 EndX=443 EndY=5 EndZ=0
    g55: ArcOfCircle CenterX=450 CenterY=5 CenterZ=0 NormalX=0 NormalY=0 NormalZ=1 AngleXU=0 Radius=7 StartAngle=2e-16 EndAngle=3.14159
    g56: LineSegment [constr] StartX=307 StartY=5 StartZ=0 EndX=457 EndY=5 EndZ=0
    g57: LineSegment StartX=607 StartY=5 StartZ=0 EndX=607 EndY=-45 EndZ=0
    g58: ArcOfCircle CenterX=600 CenterY=-45 CenterZ=0 NormalX=0 NormalY=0 NormalZ=1 AngleXU=0 Radius=7 StartAngle=3.14159 EndAngle=6.28319
    g59: LineSegment StartX=593 StartY=-45 StartZ=0 EndX=593 EndY=5 EndZ=0
    g60: ArcOfCircle CenterX=600 CenterY=5 CenterZ=0 NormalX=0 NormalY=0 NormalZ=1 AngleXU=0 Radius=7 StartAngle=1e-16 EndAngle=3.14159
    g61: LineSegment [constr] StartX=457 StartY=5 StartZ=0 EndX=607 EndY=5 EndZ=0
    g62: LineSegment StartX=757 StartY=5 StartZ=0 EndX=757 EndY=-45 EndZ=0
    g63: ArcOfCircle CenterX=750 CenterY=-45 CenterZ=0 NormalX=0 NormalY=0 NormalZ=1 AngleXU=0 Radius=7 StartAngle=3.14159 EndAngle=6.28319
    g64: LineSegment StartX=743 StartY=-45 StartZ=0 EndX=743 EndY=5 EndZ=0
    g65: ArcOfCircle CenterX=750 CenterY=5 CenterZ=0 NormalX=0 NormalY=0 NormalZ=1 AngleXU=0 Radius=7 StartAngle=1e-16 EndAngle=3.14159
    g66: LineSegment [constr] StartX=607 StartY=5 StartZ=0 EndX=757 EndY=5 EndZ=0
  constraints (160):
    c: Coincident(g0,g1)
    c: Coincident(g1,g2)
    c: Coincident(g2,g3)
    c: Coincident(g3,g0)
    c: Horizontal(g1)
    c: Horizontal(g3)
    c: Vertical(g0)
    c: Vertical(g2)
    c: Symmetric(g1,g0,g4)
    c: Coincident(g4,g-1)
    c: DistanceX(g1,g1) = 1600
    c: DistanceY(g2,g2) = 140
    c: Diameter(g5) = 14
    c: Diameter(g6) = 14
    c: DistanceX(g0,g5) = 100
    c: Distance(g5,g1) = 30
    c: Distance(g6,g1) = 30
    c: Equal(g5,g7) = 14
    c: Equal(g5,g8) = 14
    c: Equal(g5,g9) = 14
    c: Equal(g5,g10) = 14
    c: Equal(g5,g11) = 14
    c: Equal(g5,g12) = 14
    c: DistanceX(g5,g7) = 200
    c: DistanceX(g7,g8) = 200
    c: DistanceX(g8,g9) = 200
    c: DistanceX(g9,g6) = 200
    c: DistanceX(g6,g10) = 200
    c: DistanceX(g10,g11) = 200
    c: DistanceX(g11,g12) = 200
    c: Vertical(g13)
    c: Tangent(g13,g14) = 1.5708
    c: Vertical(g15)
    c: Tangent(g15,g16) = 1.5708
    c: DistanceY(g15,g15) = 50
    c: Tangent(g16,g13) = 1.5708
    c: Tangent(g14,g15) = 1.5708
    c: DistanceX(g15,g13) = 14
    c: Distance(g14,g3) = 25
    c: Distance(g14,g0) = 50
    c: Vertical(g17)
    c: Tangent(g17,g18) = 1.5708
    c: Vertical(g19)
    c: Tangent(g19,g20) = 1.5708
    c: Equal(g15,g19) = 50
    c: Tangent(g20,g17) = 1.5708
    c: Tangent(g18,g19) = 1.5708
    c: DistanceX(g19,g17) = 14
    c: Coincident(g13,g21)
    c: Coincident(g17,g21)
    c: Distance(g21) = 150
    c: Angle(g21) = 0
    c: Vertical(g22)
    c: Tangent(g22,g23) = 1.5708
    c: Vertical(g24)
    c: Tangent(g24,g25) = 1.5708
    c: Equal(g15,g24) = 50
    c: Tangent(g25,g22) = 1.5708
    c: Tangent(g23,g24) = 1.5708
    c: DistanceX(g24,g22) = 14
    c: Coincident(g17,g26)
    c: Coincident(g22,g26)
    c: Equal(g21,g26)
    c: Parallel(g26,g21)
    c: Vertical(g27)
    c: Tangent(g27,g28) = 1.5708
    c: Vertical(g29)
    c: Tangent(g29,g30) = 1.5708
    c: Equal(g15,g29) = 50
    c: Tangent(g30,g27) = 1.5708
    c: Tangent(g28,g29) = 1.5708
    c: DistanceX(g29,g27) = 14
    c: Coincident(g22,g31)
    c: Coincident(g27,g31)
    c: Equal(g21,g31)
    c: Parallel(g31,g21)
    c: Vertical(g32)
    c: Tangent(g32,g33) = 1.5708
    c: Vertical(g34)
    c: Tangent(g34,g35) = 1.5708
    c: Equal(g15,g34) = 50
    c: Tangent(g35,g32) = 1.5708
    c: Tangent(g33,g34) = 1.5708
    c: DistanceX(g34,g32) = 14
    c: Coincident(g27,g36)
    c: Coincident(g32,g36)
    c: Equal(g21,g36)
    c: Parallel(g36,g21)
    c: Vertical(g37)
    c: Tangent(g37,g38) = 1.5708
    c: Vertical(g39)
    c: Tangent(g39,g40) = 1.5708
    c: Equal(g15,g39) = 50
    c: Tangent(g40,g37) = 1.5708
    c: Tangent(g38,g39) = 1.5708
    c: DistanceX(g39,g37) = 14
    c: Coincident(g32,g41)
    c: Coincident(g37,g41)
    c: Equal(g21,g41)
    c: Parallel(g41,g21)
    c: Vertical(g42)
    c: Tangent(g42,g43) = 1.5708
    c: Vertical(g44)
    c: Tangent(g44,g45) = 1.5708
    c: Equal(g15,g44) = 50
    c: Tangent(g45,g42) = 1.5708
    c: Tangent(g43,g44) = 1.5708
    c: DistanceX(g44,g42) = 14
    c: Coincident(g37,g46)
    c: Coincident(g42,g46)
    c: Equal(g21,g46)
    c: Parallel(g46,g21)
    c: Vertical(g47)
    c: Tangent(g47,g48) = 1.5708
    c: Vertical(g49)
    c: Tangent(g49,g50) = 1.5708
    c: Equal(g15,g49) = 50
    c: Tangent(g50,g47) = 1.5708
    c: Tangent(g48,g49) = 1.5708
    c: DistanceX(g49,g47) = 14
    c: Coincident(g42,g51)
    c: Coincident(g47,g51)
    c: Equal(g21,g51)
    c: Parallel(g51,g21)
    c: Vertical(g52)
    c: Tangent(g52,g53) = 1.5708
    c: Vertical(g54)
    c: Tangent(g54,g55) = 1.5708
    c: Equal(g15,g54) = 50
    c: Tangent(g55,g52) = 1.5708
    c: Tangent(g53,g54) = 1.5708
    c: DistanceX(g54,g52) = 14
    c: Coincident(g47,g56)
    c: Coincident(g52,g56)
    c: Equal(g21,g56)
    c: Parallel(g56,g21)
    c: Vertical(g57)
    c: Tangent(g57,g58) = 1.5708
    c: Vertical(g59)
    c: Tangent(g59,g60) = 1.5708
    c: Equal(g15,g59) = 50
    c: Tangent(g60,g57) = 1.5708
    c: Tangent(g58,g59) = 1.5708
    c: DistanceX(g59,g57) = 14
    c: Coincident(g52,g61)
    c: Coincident(g57,g61)
    c: Equal(g21,g61)
    c: Parallel(g61,g21)
    c: Vertical(g62)
    c: Tangent(g62,g63) = 1.5708
    c: Vertical(g64)
    c: Tangent(g64,g65) = 1.5708
    c: Equal(g15,g64) = 50
    c: Tangent(g65,g62) = 1.5708
    c: Tangent(g63,g64) = 1.5708
    c: DistanceX(g64,g62) = 14
    c: Coincident(g57,g66)
    c: Coincident(g62,g66)
    c: Equal(g21,g66)
    c: Parallel(g66,g21)
FEATURE [Part::Extrusion] Extrude061  label="plate_1"
  Base = -> Sketch075
  Dir = (0,-1,2e-16)
  DirMode = 2
  FaceMakerClass = Part::FaceMakerBullseye
  FaceMakerMode = 3
  LengthFwd = 5
  LengthRev = 0
  Placement = pos=(1.14e-13,-2.99e-13,-80.4478) rot=(0,0,1;0rad)
  Solid = true
  Symmetric = false
FEATURE [Sketcher::SketchObject] Sketch076
  ArcFitTolerance = 0
  FullyConstrained = true
  MakeInternals = false
  Placement = pos=(0,0,0) rot=(1,0,0;1.5708rad)
  sketch-geometry (26):
    g0: LineSegment StartX=-800 StartY=-55 StartZ=0 EndX=-800 EndY=55 EndZ=0
    g1: LineSegment StartX=-800 StartY=55 StartZ=0 EndX=800 EndY=55 EndZ=0
    g2: LineSegment StartX=800 StartY=55 StartZ=0 EndX=800 EndY=-55 EndZ=0
    g3: LineSegment StartX=800 StartY=-55 StartZ=0 EndX=-800 EndY=-55 EndZ=0
    g4: GeomPoint [constr] X=0 Y=0 Z=0
    g5: Circle CenterX=-750 CenterY=25 CenterZ=0 NormalX=0 NormalY=0 NormalZ=1 AngleXU=0 Radius=7
    g6: Circle CenterX=-600 CenterY=25 CenterZ=0 NormalX=0 NormalY=0 NormalZ=1 AngleXU=0 Radius=7
    g7: LineSegment [constr] StartX=-750 StartY=25 StartZ=0 EndX=-600 EndY=25 EndZ=0
    g8: Circle CenterX=-450 CenterY=25 CenterZ=0 NormalX=0 NormalY=0 NormalZ=1 AngleXU=0 Radius=7
    g9: LineSegment [constr] StartX=-600 StartY=25 StartZ=0 EndX=-450 EndY=25 EndZ=0
    g10: Circle CenterX=-300 CenterY=25 CenterZ=0 NormalX=0 NormalY=0 NormalZ=1 AngleXU=0 Radius=7
    g11: LineSegment [constr] StartX=-450 StartY=25 StartZ=0 EndX=-300 EndY=25 EndZ=0
    g12: Circle CenterX=-150 CenterY=25 CenterZ=0 NormalX=0 NormalY=0 NormalZ=1 AngleXU=0 Radius=7
    g13: LineSegment [constr] StartX=-300 StartY=25 StartZ=0 EndX=-150 EndY=25 EndZ=0
    g14: Circle CenterX=1.11421e-10 CenterY=25 CenterZ=0 NormalX=0 NormalY=0 NormalZ=1 AngleXU=0 Radius=7
    g15: LineSegment [constr] StartX=-150 StartY=25 StartZ=0 EndX=1.11413e-10 EndY=25 EndZ=0
    g16: Circle CenterX=150 CenterY=25 CenterZ=0 NormalX=0 NormalY=0 NormalZ=1 AngleXU=0 Radius=7
    g17: LineSegment [constr] StartX=1.11421e-10 StartY=25 StartZ=0 EndX=150 EndY=25 EndZ=0
    g18: Circle CenterX=300 CenterY=25 CenterZ=0 NormalX=0 NormalY=0 NormalZ=1 AngleXU=0 Radius=7
    g19: LineSegment [constr] StartX=150 StartY=25 StartZ=0 EndX=300 EndY=25 EndZ=0
    g20: Circle CenterX=450 CenterY=25 CenterZ=0 NormalX=0 NormalY=0 NormalZ=1 AngleXU=0 Radius=7
    g21: LineSegment [constr] StartX=300 StartY=25 StartZ=0 EndX=450 EndY=25 EndZ=0
    g22: Circle CenterX=600 CenterY=25 CenterZ=0 NormalX=0 NormalY=0 NormalZ=1 AngleXU=0 Radius=7
    g23: LineSegment [constr] StartX=450 StartY=25 StartZ=0 EndX=600 EndY=25 EndZ=0
    g24: Circle CenterX=750 CenterY=25 CenterZ=0 NormalX=0 NormalY=0 NormalZ=1 AngleXU=0 Radius=7
    g25: LineSegment [constr] StartX=600 StartY=25 StartZ=0 EndX=750 EndY=25 EndZ=0
  constraints (65):
    c: Coincident(g0,g1)
    c: Coincident(g1,g2)
    c: Coincident(g2,g3)
    c: Coincident(g3,g0)
    c: Horizontal(g1)
    c: Horizontal(g3)
    c: Vertical(g0)
    c: Vertical(g2)
    c: Symmetric(g1,g0,g4)
    c: Coincident(g4,g-1)
    c: DistanceX(g1,g1) = 1600
    c: DistanceY(g2,g2) = 110
    c: Diameter(g5) = 14
    c: Distance(g5,g1) = 30
    c: Distance(g5,g0) = 50
    c: Equal(g5,g6) = 14
    c: Coincident(g5,g7)
    c: Coincident(g6,g7)
    c: Distance(g7) = 150
    c: Angle(g7) = 0
    c: Equal(g5,g8) = 14
    c: Coincident(g6,g9)
    c: Coincident(g8,g9)
    c: Equal(g7,g9)
    c: Parallel(g9,g7)
    c: Equal(g5,g10) = 14
    c: Coincident(g8,g11)
    c: Coincident(g10,g11)
    c: Equal(g7,g11)
    c: Parallel(g11,g7)
    c: Equal(g5,g12) = 14
    c: Coincident(g10,g13)
    c: Coincident(g12,g13)
    c: Equal(g7,g13)
    c: Parallel(g13,g7)
    c: Equal(g5,g14) = 14
    c: Coincident(g12,g15)
    c: Coincident(g14,g15)
    c: Equal(g7,g15)
    c: Parallel(g15,g7)
    c: Equal(g5,g16) = 14
    c: Coincident(g14,g17)
    c: Coincident(g16,g17)
    c: Equal(g7,g17)
    c: Parallel(g17,g7)
    c: Equal(g5,g18) = 14
    c: Coincident(g16,g19)
    c: Coincident(g18,g19)
    c: Equal(g7,g19)
    c: Parallel(g19,g7)
    c: Equal(g5,g20) = 14
    c: Coincident(g18,g21)
    c: Coincident(g20,g21)
    c: Equal(g7,g21)
    c: Parallel(g21,g7)
    c: Equal(g5,g22) = 14
    c: Coincident(g20,g23)
    c: Coincident(g22,g23)
    c: Equal(g7,g23)
    c: Parallel(g23,g7)
    c: Equal(g5,g24) = 14
    c: Coincident(g22,g25)
    c: Coincident(g24,g25)
    c: Equal(g7,g25)
    c: Parallel(g25,g7)
FEATURE [Part::Extrusion] Extrude062  label="rubberPlate"
  Base = -> Sketch076
  Dir = (0,-1,2e-16)
  DirMode = 2
  FaceMakerClass = Part::FaceMakerBullseye
  FaceMakerMode = 3
  LengthFwd = 10
  LengthRev = 0
  Placement = pos=(2.27e-13,-5,-125.45) rot=(0,0,1;0rad)
  Solid = true
  Symmetric = false
FEATURE [Sketcher::SketchObject] Sketch077
  ArcFitTolerance = 0
  FullyConstrained = true
  MakeInternals = false
  Placement = pos=(0,0,0) rot=(1,0,0;1.5708rad)
  sketch-geometry (26):
    g0: LineSegment StartX=-800 StartY=-25 StartZ=0 EndX=-800 EndY=25 EndZ=0
    g1: LineSegment StartX=-800 StartY=25 StartZ=0 EndX=800 EndY=25 EndZ=0
    g2: LineSegment StartX=800 StartY=25 StartZ=0 EndX=800 EndY=-25 EndZ=0
    g3: LineSegment StartX=800 StartY=-25 StartZ=0 EndX=-800 EndY=-25 EndZ=0
    g4: GeomPoint [constr] X=0 Y=0 Z=0
    g5: Circle CenterX=-750 CenterY=0 CenterZ=0 NormalX=0 NormalY=0 NormalZ=1 AngleXU=0 Radius=7
    g6: Circle CenterX=-600 CenterY=0 CenterZ=0 NormalX=0 NormalY=0 NormalZ=1 AngleXU=0 Radius=7
    g7: LineSegment [constr] StartX=-750 StartY=0 StartZ=0 EndX=-600 EndY=0 EndZ=0
    g8: Circle CenterX=-450 CenterY=0 CenterZ=0 NormalX=0 NormalY=0 NormalZ=1 AngleXU=0 Radius=7
    g9: LineSegment [constr] StartX=-600 StartY=0 StartZ=0 EndX=-450 EndY=0 EndZ=0
    g10: Circle CenterX=-300 CenterY=0 CenterZ=0 NormalX=0 NormalY=0 NormalZ=1 AngleXU=0 Radius=7
    g11: LineSegment [constr] StartX=-450 StartY=0 StartZ=0 EndX=-300 EndY=0 EndZ=0
    g12: Circle CenterX=-150 CenterY=0 CenterZ=0 NormalX=0 NormalY=0 NormalZ=1 AngleXU=0 Radius=7
    g13: LineSegment [constr] StartX=-300 StartY=0 StartZ=0 EndX=-150 EndY=0 EndZ=0
    g14: Circle CenterX=5.68e-14 CenterY=0 CenterZ=0 NormalX=0 NormalY=0 NormalZ=1 AngleXU=0 Radius=7
    g15: LineSegment [constr] StartX=-150 StartY=0 StartZ=0 EndX=5.68e-14 EndY=0 EndZ=0
    g16: Circle CenterX=150 CenterY=0 CenterZ=0 NormalX=0 NormalY=0 NormalZ=1 AngleXU=0 Radius=7
    g17: LineSegment [constr] StartX=5.68e-14 StartY=0 StartZ=0 EndX=150 EndY=0 EndZ=0
    g18: Circle CenterX=300 CenterY=0 CenterZ=0 NormalX=0 NormalY=0 NormalZ=1 AngleXU=0 Radius=7
    g19: LineSegment [constr] StartX=150 StartY=0 StartZ=0 EndX=300 EndY=0 EndZ=0
    g20: Circle CenterX=450 CenterY=0 CenterZ=0 NormalX=0 NormalY=0 NormalZ=1 AngleXU=0 Radius=7
    g21: LineSegment [constr] StartX=300 StartY=0 StartZ=0 EndX=450 EndY=0 EndZ=0
    g22: Circle CenterX=600 CenterY=0 CenterZ=0 NormalX=0 NormalY=0 NormalZ=1 AngleXU=0 Radius=7
    g23: LineSegment [constr] StartX=450 StartY=0 StartZ=0 EndX=600 EndY=0 EndZ=0
    g24: Circle CenterX=750 CenterY=0 CenterZ=0 NormalX=0 NormalY=0 NormalZ=1 AngleXU=0 Radius=7
    g25: LineSegment [constr] StartX=600 StartY=0 StartZ=0 EndX=750 EndY=0 EndZ=0
  constraints (65):
    c: Coincident(g0,g1)
    c: Coincident(g1,g2)
    c: Coincident(g2,g3)
    c: Coincident(g3,g0)
    c: Horizontal(g1)
    c: Horizontal(g3)
    c: Vertical(g0)
    c: Vertical(g2)
    c: Symmetric(g1,g0,g4)
    c: Coincident(g4,g-1)
    c: DistanceX(g1,g1) = 1600
    c: DistanceY(g2,g2) = 50
    c: PointOnObject(g5,g-1)
    c: Diameter(g5) = 14
    c: DistanceX(g0,g5) = 50
    c: Equal(g5,g6) = 14
    c: Coincident(g5,g7)
    c: Coincident(g6,g7)
    c: Distance(g7) = 150
    c: Angle(g7) = 0
    c: Equal(g5,g8) = 14
    c: Coincident(g6,g9)
    c: Coincident(g8,g9)
    c: Equal(g7,g9)
    c: Parallel(g9,g7)
    c: Equal(g5,g10) = 14
    c: Coincident(g8,g11)
    c: Coincident(g10,g11)
    c: Equal(g7,g11)
    c: Parallel(g11,g7)
    c: Equal(g5,g12) = 14
    c: Coincident(g10,g13)
    c: Coincident(g12,g13)
    c: Equal(g7,g13)
    c: Parallel(g13,g7)
    c: Equal(g5,g14) = 14
    c: Coincident(g12,g15)
    c: Coincident(g14,g15)
    c: Equal(g7,g15)
    c: Parallel(g15,g7)
    c: Equal(g5,g16) = 14
    c: Coincident(g14,g17)
    c: Coincident(g16,g17)
    c: Equal(g7,g17)
    c: Parallel(g17,g7)
    c: Equal(g5,g18) = 14
    c: Coincident(g16,g19)
    c: Coincident(g18,g19)
    c: Equal(g7,g19)
    c: Parallel(g19,g7)
    c: Equal(g5,g20) = 14
    c: Coincident(g18,g21)
    c: Coincident(g20,g21)
    c: Equal(g7,g21)
    c: Parallel(g21,g7)
    c: Equal(g5,g22) = 14
    c: Coincident(g20,g23)
    c: Coincident(g22,g23)
    c: Equal(g7,g23)
    c: Parallel(g23,g7)
    c: Equal(g5,g24) = 14
    c: Coincident(g22,g25)
    c: Coincident(g24,g25)
    c: Equal(g7,g25)
    c: Parallel(g25,g7)
FEATURE [Part::Extrusion] Extrude063  label="plate_2"
  Base = -> Sketch077
  Dir = (0,-1,2e-16)
  DirMode = 2
  FaceMakerClass = Part::FaceMakerBullseye
  FaceMakerMode = 3
  LengthFwd = 5
  LengthRev = 0
  Placement = pos=(0,-15,-100.45) rot=(0,0,1;0rad)
  Solid = true
  Symmetric = false
FEATURE [App::Part] Part058  label="blade"
  Group = -> [AngleSteel006,Extrude059,Extrude060,Sketch074,Cut025,Sketch075,Extrude061,Sketch076,Extrude062,Sketch077,Extrude063]
  Origin = -> Origin085
  Placement = pos=(800,0,0) rot=(0,0,1;5.49779rad)
  expr: .Placement.Base.x = Spreadsheet009.br
FEATURE [Part::FeaturePython] Array031  # Draft array (typed FeaturePython)
  AlwaysSyncPlacement = false
  Angle = 360
  ArrayType = 0
  Axis = (0,0,1)
  Base = -> Part058
  Center = (0,0,0)
  Count = 7
  ExpandArray = false
  Fuse = false
  IntervalAxis = (0,0,0)
  IntervalX = (960,0,0)
  IntervalY = (0,100,0)
  IntervalZ = (0,0,100)
  NumberCircles = 3
  NumberPolar = 5
  NumberX = 7
  NumberY = 1
  NumberZ = 1
  PlacementList = 7 placements: arithmetic series from (800,0,0) step (960,0,0) to (6560,0,0)
  RadialDistance = 50
  ScaleList = (7) [(1,1,1),(1,1,1),(1,1,1),(1,1,1),(1,1,1),(1,1,1),(1,1,1)]
  Symmetry = 1
  TangentialDistance = 25
  expr: .IntervalX.x = Spreadsheet009.brs
  expr: NumberX = Spreadsheet009.n00
FEATURE [Sketcher::SketchObject] Sketch078
  ArcFitTolerance = 0
  FullyConstrained = true
  MakeInternals = false
  MapMode = 5
  Placement = pos=(0,0,0) rot=(1,0,0;1.5708rad)
  expr: Constraints[10] = Spreadsheet010.L7 * 2
  expr: Constraints[9] = Spreadsheet010.B7
  sketch-geometry (4):
    g0: LineSegment StartX=90 StartY=23 StartZ=0 EndX=-8.967e-12 EndY=23 EndZ=0
    g1: ArcOfCircle CenterX=0 CenterY=0 CenterZ=0 NormalX=0 NormalY=0 NormalZ=1 AngleXU=0 Radius=23 StartAngle=1.5708 EndAngle=4.71239
    g2: LineSegment StartX=-9.439e-13 StartY=-23 StartZ=0 EndX=90 EndY=-23 EndZ=0
    g3: LineSegment StartX=90 StartY=-23 StartZ=0 EndX=90 EndY=23 EndZ=0
  constraints (11):
    c: Horizontal(g0)
    c: Tangent(g0,g1) = -1.5708
    c: PointOnObject(g1,g-2)
    c: Coincident(g1,g2)
    c: Horizontal(g2)
    c: Coincident(g2,g3)
    c: Coincident(g3,g0)
    c: Vertical(g3)
    c: Coincident(g-1,g1)
    c: DistanceX(g0,g0) = 90
    c: Distance(g3) = 46
FEATURE [PartDesign::Pad] Pad001
  Direction = (0,-1,0)
  Length = 40
  Length2 = 10
  Midplane = true
  Placement = pos=(0,0,0) rot=(1,0,0;1.5708rad)
  Profile = -> Sketch078
  ReferenceAxis = -> Sketch078 [N_Axis]
  Suppressed = false
  Type = 0
  expr: Length = Spreadsheet010.D7
FEATURE [Spreadsheet::Sheet] Spreadsheet010
  cells = A2='rodDia dia; B2(dia)=20; A3='length L0; B3(L0)=1270; B4='l; C4='l1; D4='a; E4='b; F4='c; G4='e; H4='f; I4='g; J4='h; K4='i; L4='r; A5='forkEndR; B5=120; D5=40; E5=16; F5=21; G5=24; H5=20; I5=60; J5=10; K5=20; L5=23; A6='turnBackle; B6=150; C6=28; D6=42; E6=23; F6=33; A7='forkEndL; B7=90; D7=40; E7=16; F7=20; G7=24; H7=20; I7=30; L7=23; A8=1; B8=2; C8=3; D8=4; E8=5; F8=6; G8=7; H8=8; I8=9; J8=10; K8=11; L8=12; A9='turnBackle; A10='d; B10='l; C10='l1; D10='a; E10='b; F10='c; A11=10; B11=75; C11=15; D11=24; E11=13; F11=17; A12=12; B12=100; C12=20; D12=30; E12=16; F12=22; A13=16; B13=125; C13=24; D13=36; E13=20; F13=27; A14=20; B14=150; C14=28; D14=42; E14=23; F14=33; A15=22; B15=175; C15=33; D15=48; E15=27; F15=37; A16=24; B16=200; C16=38; D16=54; E16=30; F16=42; A17=30; B17=250; C17=47; D17=66; E17=37; F17=52; A18='forkEnd_L; A19='d; B19='l; C19='a; D19='b; E19='c; F19='e; G19='f; H19='g; I19='r; A20=10; B20=50; C20=20; D20=7; E20=10; F20=12; G20=10; H20=15; I20=12; A21=12; B21=60; C21=25; D21=10; E21=13; F21=16; G21=13; H21=20; I21=15; A22=16; B22=75; C22=30; D22=13; E22=16; F22=20; G22=16; H22=25; I22=19; A23=20; B23=90; C23=40; D23=16; E23=20; F23=24; G23=20; H23=30; I23=23; A24=22; B24=100; C24=45; D24=20; E24=23; F24=28; G24=23; H24=35; I24=27; A25=24; B25=115; C25=50; D25=23; E25=26; F25=32; G25=26; H25=40; I25=30; A26=30; B26=140; C26=65; D26=30; E26=33; F26=40; G26=33; H26=50; I26=38; A27='forkEnd_R; A28='d; B28='l; C28='a; D28='b; E28='c; F28='r; G28='e; H28='f; I28='g; J28='h; K28='i; A29=10; B29=60; C29=20; D29=7; E29=11; F29=12; G29=12; H29=10; I29=30; J29=5; K29=10; A30=12; B30=80; +64 more cells
FEATURE [Sketcher::SketchObject] Sketch079
  ArcFitTolerance = 0
  AttachmentSupport = -> [Pad001]
  FullyConstrained = true
  MakeInternals = false
  MapMode = 5
  Placement = pos=(0,-20,0) rot=(1,0,0;1.5708rad)
  expr: Constraints[1] = Spreadsheet010.F7 / 2
  sketch-geometry (1):
    g0: Circle CenterX=0 CenterY=0 CenterZ=0 NormalX=0 NormalY=0 NormalZ=1 AngleXU=0 Radius=10
  constraints (2):
    c: Coincident(g0,g-1)
    c: Radius(g0) = 10
FEATURE [Part::Extrusion] Extrude064
  Base = -> Sketch079
  Dir = (0,-1,2e-16)
  DirMode = 2
  FaceMakerClass = Part::FaceMakerBullseye
  FaceMakerMode = 3
  LengthFwd = 65
  LengthRev = 0
  Reversed = true
  Solid = true
  Symmetric = false
FEATURE [Sketcher::SketchObject] Sketch080
  ArcFitTolerance = 0
  FullyConstrained = true
  MakeInternals = false
  Placement = pos=(0,0,0) rot=(1,0,0;1.5708rad)
  expr: Constraints[11] = Spreadsheet010.I5
  expr: Constraints[1] = Spreadsheet010.F5 / 2
  expr: Constraints[3] = Spreadsheet010.L5
  sketch-geometry (5):
    g0: Circle CenterX=0 CenterY=0 CenterZ=0 NormalX=0 NormalY=0 NormalZ=1 AngleXU=0 Radius=10.5
    g1: ArcOfCircle CenterX=0 CenterY=0 CenterZ=0 NormalX=0 NormalY=0 NormalZ=1 AngleXU=0 Radius=23 StartAngle=4.71239 EndAngle=7.85398
    g2: LineSegment StartX=-1.34e-14 StartY=23 StartZ=0 EndX=-60 EndY=23 EndZ=0
    g3: LineSegment StartX=-60 StartY=23 StartZ=0 EndX=-60 EndY=-23 EndZ=0
    g4: LineSegment StartX=-60 StartY=-23 StartZ=0 EndX=-7.1e-15 EndY=-23 EndZ=0
  constraints (12):
    c: Coincident(g0,g-1)
    c: Radius(g0) = 10.5
    c: Coincident(g1,g0)
    c: Radius(g1) = 23
    c: Horizontal(g2)
    c: Coincident(g2,g3)
    c: Vertical(g3)
    c: Coincident(g3,g4)
    c: Horizontal(g4)
    c: Tangent(g1,g2) = -1.5708
    c: Tangent(g1,g4) = -1.5708
    c: Distance(g2) = 60
FEATURE [Part::Extrusion] Extrude065
  Base = -> Sketch080
  Dir = (0,-1,2e-16)
  DirMode = 2
  FaceMakerClass = Part::FaceMakerBullseye
  FaceMakerMode = 3
  LengthFwd = 40
  LengthRev = 0
  Solid = true
  Symmetric = true
  expr: LengthFwd = Spreadsheet010.D5
FEATURE [Sketcher::SketchObject] Sketch081
  ArcFitTolerance = 0
  AttachmentSupport = -> [Extrude065]
  ExternalGeometry = -> [Extrude065]
  FullyConstrained = true
  MakeInternals = false
  MapMode = 5
  Placement = pos=(0,5.1e-15,23) rot=(0,0,1;0rad)
  expr: Constraints[10] = Spreadsheet010.E5
  expr: Constraints[24] = Spreadsheet010.G5
  expr: Constraints[25] = Spreadsheet010.K5
  expr: Constraints[26] = Spreadsheet010.H5
  expr: Constraints[31] = Spreadsheet010.E5 / 2
  expr: Constraints[32] = Spreadsheet010.G5 / 2
  expr: Constraints[9] = Spreadsheet010.L5
  sketch-geometry (12):
    g0: LineSegment StartX=23 StartY=8 StartZ=0 EndX=-20 EndY=8 EndZ=0
    g1: LineSegment StartX=-21 StartY=12 StartZ=0 EndX=-39 EndY=12 EndZ=0
    g2: LineSegment StartX=-40 StartY=11 StartZ=0 EndX=-40 EndY=-11 EndZ=0
    g3: LineSegment StartX=-39 StartY=-12 StartZ=0 EndX=-21 EndY=-12 EndZ=0
    g4: LineSegment StartX=-20 StartY=-11 StartZ=0 EndX=-20 EndY=-8 EndZ=0
    g5: LineSegment StartX=-20 StartY=-8 StartZ=0 EndX=23 EndY=-8 EndZ=0
    g6: LineSegment StartX=23 StartY=-8 StartZ=0 EndX=23 EndY=8 EndZ=0
    g7: ArcOfCircle CenterX=-21 CenterY=11 CenterZ=0 NormalX=0 NormalY=0 NormalZ=1 AngleXU=0 Radius=1 StartAngle=6.28317 EndAngle=7.85398
    g8: ArcOfCircle CenterX=-21 CenterY=-11 CenterZ=0 NormalX=0 NormalY=0 NormalZ=1 AngleXU=0 Radius=1 StartAngle=4.71239 EndAngle=6.28319
    g9: ArcOfCircle CenterX=-39 CenterY=11 CenterZ=0 NormalX=0 NormalY=0 NormalZ=1 AngleXU=0 Radius=1 StartAngle=1.5708 EndAngle=3.14159
    g10: ArcOfCircle CenterX=-39 CenterY=-11 CenterZ=0 NormalX=0 NormalY=0 NormalZ=1 AngleXU=0 Radius=1 StartAngle=3.14159 EndAngle=4.71239
    g11: LineSegment StartX=-20 StartY=8 StartZ=0 EndX=-20 EndY=11 EndZ=0
  constraints (33):
    c: Horizontal(g0)
    c: Horizontal(g1)
    c: Vertical(g2)
    c: Horizontal(g3)
    c: Coincident(g4,g5)
    c: Horizontal(g5)
    c: Coincident(g5,g6)
    c: Coincident(g6,g0)
    c: Vertical(g6)
    c: DistanceX(g-1,g5) = 23
    c: Distance(g6) = 16
    c: Vertical(g4)
    c: Vertical(g4,g0)
    c: Tangent(g1,g7) = -1.5708
    c: Tangent(g4,g8) = -1.5708
    c: Tangent(g3,g8) = -1.5708
    c: Tangent(g2,g9) = -1.5708
    c: Tangent(g1,g9) = -1.5708
    c: Tangent(g3,g10) = -1.5708
    c: Tangent(g2,g10) = -1.5708
    c: Radius(g7) = 1
    c: Radius(g8) = 1
    c: Equal(g10,g9)
    c: Radius(g10) = 1
    c: DistanceY(g3,g1) = 24
    c: DistanceX(g-3,g2) = 20
    c: DistanceX(g4,g-1) = 20
    c: Equal(g3,g1)
    c: Coincident(g11,g0)
    c: Coincident(g11,g7)
    c: Vertical(g11)
    c: DistanceY(g-1,g0) = 8
    c: DistanceY(g-1,g1) = 12
FEATURE [Part::Extrusion] Extrude066
  Base = -> Sketch081
  Dir = (0,0,1)
  DirMode = 2
  FaceMakerClass = Part::FaceMakerBullseye
  FaceMakerMode = 3
  LengthFwd = 80
  LengthRev = 0
  Reversed = true
  Solid = true
  Symmetric = false
FEATURE [Part::Cut] Cut026
  Base = -> Extrude065
  Tool = -> Extrude066
FEATURE [Part::Cylinder] Cylinder004  label="円柱002"
  Angle = 360
  AttacherType = Attacher::AttachEngine3D
  FirstAngle = 0
  Height = 120
  Placement = pos=(-60,0,0) rot=(0,-1,0;1.5708rad)
  Radius = 10
  SecondAngle = 0
  expr: .Placement.Base.x = -Spreadsheet010.I5
  expr: Height = Spreadsheet010.B5
  expr: Radius = Spreadsheet010.dia / 2
FEATURE [Part::MultiFuse] Fusion008  label="forkEndR"
  Shapes = -> [Cut026,Cylinder004]
FEATURE [Sketcher::SketchObject] Sketch082
  ArcFitTolerance = 0
  FullyConstrained = true
  MakeInternals = false
  Placement = pos=(0,0,0) rot=(1,0,0;1.5708rad)
  expr: Constraints[10] = Spreadsheet010.C6
  expr: Constraints[11] = Spreadsheet010.B6
  expr: Constraints[12] = Spreadsheet010.D6 / 2
  expr: Constraints[13] = Spreadsheet010.F6 / 2
  expr: Constraints[14] = Spreadsheet010.B6 / 2
  expr: Constraints[17] = Spreadsheet010.C6
  sketch-geometry (6):
    g0: LineSegment StartX=-75 StartY=0 StartZ=0 EndX=-75 EndY=16.5 EndZ=0
    g1: LineSegment StartX=-75 StartY=16.5 StartZ=0 EndX=-47 EndY=21 EndZ=0
    g2: LineSegment StartX=-47 StartY=21 StartZ=0 EndX=47 EndY=21 EndZ=0
    g3: LineSegment StartX=47 StartY=21 StartZ=0 EndX=75 EndY=16.5 EndZ=0
    g4: LineSegment StartX=75 StartY=16.5 StartZ=0 EndX=75 EndY=0 EndZ=0
    g5: LineSegment StartX=75 StartY=0 StartZ=0 EndX=-75 EndY=0 EndZ=0
  constraints (18):
    c: PointOnObject(g0,g-1)
    c: Vertical(g0)
    c: Coincident(g0,g1)
    c: Coincident(g1,g2)
    c: Horizontal(g2)
    c: Coincident(g2,g3)
    c: Coincident(g3,g4)
    c: PointOnObject(g4,g-1)
    c: Vertical(g4)
    c: Coincident(g4,g5)
    c: DistanceX(g2,g3) = 28
    c: DistanceX(g0,g3) = 150
    c: Distance(g1,g5) = 21
    c: Distance(g4) = 16.5
    c: DistanceX(g-1,g4) = 75
    c: Horizontal(g0,g3)
    c: Coincident(g5,g0)
    c: DistanceX(g0,g1) = 28
FEATURE [Part::Revolution] Revolve015
  Angle = 360
  Axis = (-1,0,0)
  AxisLink = -> Sketch082 [Edge6]
  Base = (-75,0,0)
  FaceMakerClass = Part::FaceMakerBullseye
  Solid = true
  Source = -> Sketch082
  Symmetric = false
FEATURE [Sketcher::SketchObject] Sketch083
  ArcFitTolerance = 0
  FullyConstrained = false
  MakeInternals = false
  Placement = pos=(0,0,0) rot=(0.57735,0.57735,0.57735;2.0944rad)
  expr: Constraints[16] = Spreadsheet010.F6
  expr: Constraints[17] = Spreadsheet010.F6 / 2
  sketch-geometry (8):
    g0: LineSegment StartX=-16.5 StartY=39.685 StartZ=0 EndX=-31.5 EndY=39.685 EndZ=0
    g1: LineSegment StartX=-31.5 StartY=39.685 StartZ=0 EndX=-31.5 EndY=-39.3666 EndZ=0
    g2: LineSegment StartX=-31.5 StartY=-39.3666 StartZ=0 EndX=-16.5 EndY=-39.3666 EndZ=0
    g3: LineSegment StartX=-16.5 StartY=-39.3666 StartZ=0 EndX=-16.5 EndY=39.685 EndZ=0
    g4: LineSegment StartX=16.5 StartY=39.685 StartZ=0 EndX=31.5 EndY=39.685 EndZ=0
    g5: LineSegment StartX=31.5 StartY=39.685 StartZ=0 EndX=31.5 EndY=-40.315 EndZ=0
    g6: LineSegment StartX=31.5 StartY=-40.315 StartZ=0 EndX=16.5 EndY=-40.315 EndZ=0
    g7: LineSegment StartX=16.5 StartY=-40.315 StartZ=0 EndX=16.5 EndY=39.685 EndZ=0
  constraints (22):
    c: Coincident(g0,g1)
    c: Coincident(g1,g2)
    c: Coincident(g2,g3)
    c: Coincident(g3,g0)
    c: Horizontal(g0)
    c: Horizontal(g2)
    c: Vertical(g1)
    c: Vertical(g3)
    c: Coincident(g4,g5)
    c: Coincident(g5,g6)
    c: Coincident(g6,g7)
    c: Coincident(g7,g4)
    c: Horizontal(g4)
    c: Horizontal(g6)
    c: Vertical(g5)
    c: Vertical(g7)
    c: DistanceX(g0,g4) = 33
    c: Distance(g-1,g7) = 16.5
    c: Distance(g5) = 80
    c: Distance(g4) = 15
    c: Distance(g0) = 15
    c: Horizontal(g0,g4)
FEATURE [Part::Extrusion] Extrude067
  Base = -> Sketch083
  Dir = (1,0,0)
  DirMode = 2
  FaceMakerClass = Part::FaceMakerBullseye
  FaceMakerMode = 3
  LengthFwd = 300
  LengthRev = 0
  Solid = true
  Symmetric = true
FEATURE [Part::Cut] Cut027
  Base = -> Revolve015
  Tool = -> Extrude067
FEATURE [Sketcher::SketchObject] Sketch013
  ArcFitTolerance = 0
  FullyConstrained = true
  MakeInternals = false
  Placement = pos=(0,0,0) rot=(1,0,0;1.5708rad)
  expr: Constraints[17] = Spreadsheet010.E6
  expr: Constraints[18] = Spreadsheet010.B6 - 2 * Spreadsheet010.C6
  expr: Constraints[19] = (Spreadsheet010.B6 - 2 * Spreadsheet010.C6) / 2
  expr: Constraints[20] = Spreadsheet010.E6 / 2
  sketch-geometry (9):
    g0: LineSegment StartX=47 StartY=6.5 StartZ=0 EndX=47 EndY=-6.5 EndZ=0
    g1: LineSegment StartX=42 StartY=-11.5 StartZ=0 EndX=-42 EndY=-11.5 EndZ=0
    g2: LineSegment StartX=-47 StartY=-6.5 StartZ=0 EndX=-47 EndY=6.5 EndZ=0
    g3: LineSegment StartX=-42 StartY=11.5 StartZ=0 EndX=42 EndY=11.5 EndZ=0
    g4: GeomPoint [constr] X=0 Y=0 Z=0
    g5: ArcOfCircle CenterX=-42 CenterY=6.5 CenterZ=0 NormalX=0 NormalY=0 NormalZ=1 AngleXU=0 Radius=5 StartAngle=1.5708 EndAngle=3.14159
    g6: ArcOfCircle CenterX=-42 CenterY=-6.5 CenterZ=0 NormalX=0 NormalY=0 NormalZ=1 AngleXU=0 Radius=5 StartAngle=3.14159 EndAngle=4.71239
    g7: ArcOfCircle CenterX=42 CenterY=-6.5 CenterZ=0 NormalX=0 NormalY=0 NormalZ=1 AngleXU=0 Radius=5 StartAngle=4.71239 EndAngle=6.28319
    g8: ArcOfCircle CenterX=42 CenterY=6.5 CenterZ=0 NormalX=0 NormalY=0 NormalZ=1 AngleXU=0 Radius=5 StartAngle=0 EndAngle=1.5708
  constraints (21):
    c: Horizontal(g1)
    c: Horizontal(g3)
    c: Vertical(g0)
    c: Vertical(g2)
    c: Coincident(g4,g-1)
    c: Tangent(g3,g5) = 1.5708
    c: Tangent(g2,g5) = 1.5708
    c: Tangent(g1,g6) = 1.5708
    c: Tangent(g2,g6) = 1.5708
    c: Tangent(g1,g7) = 1.5708
    c: Tangent(g0,g7) = 1.5708
    c: Tangent(g0,g8) = 1.5708
    c: Tangent(g3,g8) = 1.5708
    c: Radius(g8) = 5
    c: Equal(g8,g7)
    c: Equal(g7,g6)
    c: Equal(g6,g5)
    c: DistanceY(g1,g3) = 23
    c: DistanceX(g2,g0) = 94
    c: Distance(g4,g2) = 47
    c: Distance(g4,g1) = 11.5
FEATURE [Part::Extrusion] Extrude068
  Base = -> Sketch013
  Dir = (0,-1,2e-16)
  DirMode = 2
  FaceMakerClass = Part::FaceMakerBullseye
  FaceMakerMode = 3
  LengthFwd = 60
  LengthRev = 0
  Solid = true
  Symmetric = true
FEATURE [Part::Cut] Cut028
  Base = -> Cut027
  Tool = -> Extrude068
FEATURE [Sketcher::SketchObject] Sketch084
  ArcFitTolerance = 0
  FullyConstrained = true
  MakeInternals = false
  Placement = pos=(0,0,0) rot=(0.57735,0.57735,0.57735;2.0944rad)
  expr: Constraints[1] = Spreadsheet010.dia / 2
  sketch-geometry (1):
    g0: Circle CenterX=0 CenterY=0 CenterZ=0 NormalX=0 NormalY=0 NormalZ=1 AngleXU=0 Radius=10
  constraints (2):
    c: Coincident(g0,g-1)
    c: Radius(g0) = 10
FEATURE [Part::Extrusion] Extrude069
  Base = -> Sketch084
  Dir = (1,0,0)
  DirMode = 2
  FaceMakerClass = Part::FaceMakerBullseye
  FaceMakerMode = 3
  LengthFwd = 300
  LengthRev = 0
  Solid = true
  Symmetric = true
FEATURE [Part::Cut] Cut006  label="turnBackle"
  Base = -> Cut028
  Placement = pos=(-200,0,0) rot=(0,0,1;0rad)
  Tool = -> Extrude069
  expr: .Placement.Base.x = -(Spreadsheet010.B5 + Spreadsheet010.I5 + Spreadsheet010.dia)
FEATURE [Part::Cylinder] Cylinder001  label="rod003"
  Angle = 360
  AttacherType = Attacher::AttachEngine3D
  FirstAngle = 0
  Height = 996
  Placement = pos=(-220,0,-8.8e-14) rot=(0,-1,0;1.5708rad)
  Radius = 10
  SecondAngle = 0
  expr: .Placement.Base.x = -(Spreadsheet010.B5 + Spreadsheet010.I5 + Spreadsheet010.dia * 2)
  expr: Height = Spreadsheet010.L0 - (Spreadsheet010.B5 + Spreadsheet010.I5 + Spreadsheet010.B6 - 4 * Spreadsheet010.dia - 2 * Spreadsheet010.C6) - Spreadsheet010.B7 + Spreadsheet010.I7 - Spreadsheet010.dia
  expr: Radius = Spreadsheet010.dia / 2
FEATURE [Sketcher::SketchObject] Sketch085
  ArcFitTolerance = 0
  FullyConstrained = true
  MakeInternals = false
  MapMode = 5
  Placement = pos=(90,0,0) rot=(0.57735,0.57735,0.57735;2.0944rad)
  expr: Constraints[1] = Spreadsheet010.dia
  sketch-geometry (1):
    g0: Circle CenterX=0 CenterY=0 CenterZ=0 NormalX=0 NormalY=0 NormalZ=1 AngleXU=0 Radius=10
  constraints (2):
    c: Coincident(g0,g-1)
    c: Diameter(g0) = 20
FEATURE [Part::Extrusion] Extrude070
  Base = -> Sketch085
  Dir = (1,0,0)
  DirMode = 2
  FaceMakerClass = Part::FaceMakerBullseye
  FaceMakerMode = 3
  LengthFwd = 30
  LengthRev = 0
  Solid = true
  Symmetric = false
  expr: LengthFwd = Spreadsheet010.I7
FEATURE [Sketcher::SketchObject] Sketch086
  ArcFitTolerance = 0
  ExternalGeometry = -> [Pad001]
  FullyConstrained = true
  MakeInternals = false
  expr: Constraints[17] = Spreadsheet010.G7
  expr: Constraints[18] = Spreadsheet010.G7 / 2
  expr: Constraints[27] = Spreadsheet010.E7 / 2
  expr: Constraints[31] = Spreadsheet010.I7
  expr: Constraints[32] = Spreadsheet010.L7
  expr: Constraints[6] = Spreadsheet010.E7
  expr: Constraints[7] = Spreadsheet010.H7
  sketch-geometry (12):
    g0: LineSegment StartX=-23 StartY=8 StartZ=0 EndX=20 EndY=8 EndZ=0
    g1: LineSegment StartX=22 StartY=12 StartZ=0 EndX=58 EndY=12 EndZ=0
    g2: LineSegment StartX=60 StartY=10 StartZ=0 EndX=60 EndY=-10 EndZ=0
    g3: LineSegment StartX=58 StartY=-12 StartZ=0 EndX=22 EndY=-12 EndZ=0
    g4: LineSegment StartX=20 StartY=-10 StartZ=0 EndX=20 EndY=-8 EndZ=0
    g5: LineSegment StartX=20 StartY=-8 StartZ=0 EndX=-23 EndY=-8 EndZ=0
    g6: LineSegment StartX=-23 StartY=-8 StartZ=0 EndX=-23 EndY=8 EndZ=0
    g7: ArcOfCircle CenterX=22 CenterY=10 CenterZ=0 NormalX=0 NormalY=0 NormalZ=1 AngleXU=0 Radius=2 StartAngle=1.5708 EndAngle=3.14159
    g8: ArcOfCircle CenterX=22 CenterY=-10 CenterZ=0 NormalX=0 NormalY=0 NormalZ=1 AngleXU=0 Radius=2 StartAngle=3.14159 EndAngle=4.71239
    g9: ArcOfCircle CenterX=58 CenterY=-10 CenterZ=0 NormalX=0 NormalY=0 NormalZ=1 AngleXU=0 Radius=2 StartAngle=4.71239 EndAngle=6.28319
    g10: ArcOfCircle CenterX=58 CenterY=10 CenterZ=0 NormalX=0 NormalY=0 NormalZ=1 AngleXU=0 Radius=2 StartAngle=5e-16 EndAngle=1.5708
    g11: LineSegment StartX=20 StartY=8 StartZ=0 EndX=20 EndY=10 EndZ=0
  constraints (33):
    c: Horizontal(g0)
    c: Coincident(g4,g5)
    c: Horizontal(g5)
    c: Coincident(g5,g6)
    c: Coincident(g6,g0)
    c: Vertical(g6)
    c: DistanceY(g6,g6) = 16
    c: DistanceX(g-1,g0) = 20
    c: Horizontal(g1)
    c: Horizontal(g3)
    c: Coincident(g11,g0)
    c: Vertical(g11)
    c: Vertical(g2)
    c: Tangent(g9,g2) = 1.5708
    c: Tangent(g1,g10) = 1.5708
    c: Tangent(g10,g2) = 1.5708
    c: Tangent(g1,g7) = 1.5708
    c: DistanceY(g3,g1) = 24
    c: DistanceY(g-1,g1) = 12
    c: Radius(g10) = 2
    c: Equal(g10,g9)
    c: Equal(g9,g7)
    c: Radius(g8) = 2
    c: Vertical(g4)
    c: Vertical(g4,g0)
    c: Tangent(g8,g4) = 1.5708
    c: Vertical(g8,g8)
    c: DistanceY(g-1,g0) = 8
    c: Tangent(g9,g3) = 1.5708
    c: Tangent(g7,g11) = 1.5708
    c: Coincident(g8,g3)
    c: DistanceX(g2,g-3) = 30
    c: DistanceX(g0,g-1) = 23
FEATURE [Part::Extrusion] Extrude071
  Base = -> Sketch086
  Dir = (0,0,1)
  DirMode = 2
  FaceMakerClass = Part::FaceMakerBullseye
  FaceMakerMode = 3
  LengthFwd = 150
  LengthRev = 0
  Solid = true
  Symmetric = true
FEATURE [Part::Cut] Cut029
  Base = -> Pad001
  Tool = -> Extrude071
FEATURE [Part::Cut] Cut030  label="Cut007"
  Base = -> Cut029
  Tool = -> Extrude070
FEATURE [Part::Cut] Cut031  label="forkEndL"
  Base = -> Cut030
  Placement = pos=(-1270,0,0) rot=(0,0,1;0rad)
  Tool = -> Extrude064
  expr: .Placement.Base.x = -Spreadsheet010.L0
FEATURE [App::Part] Part060  label="TurnBackle"
  Group = -> [Spreadsheet010,Sketch080,Cylinder004,Cut026,Sketch081,Extrude065,Extrude066,Fusion008,Revolve015,Sketch083,Cut028,Cut027,Extrude067,Extrude068,Extrude069,Sketch013,Sketch082,Sketch084,Cut006,Cylinder001,Extrude064,Sketch079,Extrude070,Extrude071,Cut029,Cut030,Sketch085,Pad001,Sketch078,Sketch086,Cut031]
  Origin = -> Origin087
  Placement = pos=(85.3515,-391.5,1628.18) rot=(0,-1,0;2.4836rad)
FEATURE [Part::FeaturePython] Clone013  label="TurnBackle001"  # Draft clone (typed FeaturePython)
  AttacherType = Attacher::AttachEngine3D
  Fuse = false
  Objects = -> [Part060]
  Placement = pos=(85.464,392,1628.12) rot=(0,1,0;3.79958rad)
  Scale = (1,1,1)
FEATURE [App::Part] Part059  label="rakeAssy"
  Group = -> [Part058,Part056,Array031,Spreadsheet009,Part060,Clone013]
  Origin = -> Origin086
  Placement = pos=(1059.84,-2.274e-13,945.714) rot=(0,1,0;-0.101229rad)
  mass = 619.955
FEATURE [Spreadsheet::Sheet] Spreadsheet011
  cells = A2='tankDia; B2(dia)=16500
FEATURE [Part::FeaturePython] Flange_Reducer  # WARN: FeaturePython — macro-defined, semantics opaque (R4)
  Fittings = 04_Flange Reducer
  Placement = pos=(2.40399e-05,1.33348e-05,915.9) rot=(0,1,0;1.5708rad)
  dia = 32
FEATURE [App::FeaturePython] GroundedJoint  # Assembly grounded joint (typed FeaturePython)
  ObjectToGround = -> Flange_Reducer
  Placement = pos=(2.40399e-05,1.33348e-05,915.9) rot=(0,1,0;1.5708rad)
FEATURE [Part::FeaturePython] F90Elbow  # WARN: FeaturePython — macro-defined, semantics opaque (R4)
  Fittings = 05_F90Elbow
  Placement = pos=(-0.000198999,1.33348e-05,-453.1) rot=(1,0,0;4.71239rad)
  dia = 7
FEATURE [App::FeaturePython] Joint  label="Fixed"  # Assembly joint (typed FeaturePython)
  Activated = true
  AngleMax = 0
  AngleMin = 0
  Detach1 = false
  Detach2 = false
  Distance = 0
  Distance2 = 0
  EnableAngleMax = false
  EnableAngleMin = false
  EnableLengthMax = false
  EnableLengthMin = false
  JointType = 0 (Fixed)
  LengthMax = 0
  LengthMin = 0
  Offset2 = pos=(0,0,0) rot=(0,0,1;1.5708rad)
  Placement1 = pos=(3.293e-13,-659,-1.81e-13) rot=(-0.57735,-0.57735,-0.57735;2.0944rad)
  Placement2 = pos=(710,-2.844e-13,-2.745e-13) rot=(-0.57735,-0.57735,0.57735;2.0944rad)
  Reference1 = -> Part036 [Assembly.F90Elbow.Edge2,Assembly.F90Elbow.Edge2]
  Reference2 = -> Part036 [Assembly.Flange_Reducer.Edge69,Assembly.Flange_Reducer.Edge69]
FEATURE [Part::FeaturePython] K_Short_tube_No_1th  # WARN: FeaturePython — macro-defined, semantics opaque (R4)
  Fittings = 16_K_Short tube No.1th
  Placement = pos=(939,1.33348e-05,-453.1) rot=(0,0.707107,0.707107;3.14159rad)
  dia = 7
FEATURE [App::FeaturePython] Joint001  label="Fixed001"  # Assembly joint (typed FeaturePython)
  Activated = true
  AngleMax = 0
  AngleMin = 0
  Detach1 = false
  Detach2 = false
  Distance = 0
  Distance2 = 0
  EnableAngleMax = false
  EnableAngleMin = false
  EnableLengthMax = false
  EnableLengthMin = false
  JointType = 0 (Fixed)
  LengthMax = 0
  LengthMin = 0
  Placement1 = pos=(280,-5.68e-14,-6.05e-14) rot=(0,-1,0;1.5708rad)
  Placement2 = pos=(659,3.411e-13,6.62e-14) rot=(0,1,0;4.71239rad)
  Reference1 = -> Part036 [Assembly.K_Short_tube_No_1th.Edge21,Assembly.K_Short_tube_No_1th.Edge21]
  Reference2 = -> Part036 [Assembly.F90Elbow.Edge59,Assembly.F90Elbow.Edge59]
FEATURE [Part::FeaturePython] K_5Elbow  # WARN: FeaturePython — macro-defined, semantics opaque (R4)
  Fittings = 09_K_5_5/8Bent tube
  Placement = pos=(1520,1.33348e-05,-453.1) rot=(0.539582,-0.595337,0.595337;2.15197rad)
  dia = 2
FEATURE [App::FeaturePython] Joint002  label="Fixed002"  # Assembly joint (typed FeaturePython)
  Activated = true
  AngleMax = 0
  AngleMin = 0
  Detach1 = false
  Detach2 = false
  Distance = 0
  Distance2 = 0
  EnableAngleMax = false
  EnableAngleMin = false
  EnableLengthMax = false
  EnableLengthMin = false
  JointType = 0 (Fixed)
  LengthMax = 0
  LengthMin = 0
  Offset2 = pos=(0,0,0) rot=(0,0,-1;1.5708rad)
  Placement1 = pos=(67.7298,687.673,-1.261e-13) rot=(-0.997595,0.049009,-0.049009;1.5732rad)
  Placement2 = pos=(110,-5.68e-14,-2.41e-14) rot=(-0.57735,-0.57735,-0.57735;4.18879rad)
  Reference1 = -> Part036 [Assembly.K_5Elbow.Edge31,Assembly.K_5Elbow.Edge31]
  Reference2 = -> Part036 [Assembly.K_Short_tube_No_1th.Edge11,Assembly.K_Short_tube_No_1th.Edge11]
FEATURE [Part::FeaturePython] K_Straight_tube  # WARN: FeaturePython — macro-defined, semantics opaque (R4)
  Fittings = 00_K_Straight tube
  L = 6000
  Placement = pos=(8139.97,1.33348e-05,198.909) rot=(-0.049068,0,0.998795;3.14159rad)
  dia = 7
FEATURE [App::FeaturePython] Joint003  label="Fixed003"  # Assembly joint (typed FeaturePython)
  Activated = true
  AngleMax = 0
  AngleMin = 0
  Detach1 = false
  Detach2 = false
  Distance = 0
  Distance2 = 0
  EnableAngleMax = false
  EnableAngleMin = false
  EnableLengthMax = false
  EnableLengthMin = false
  JointType = 0 (Fixed)
  LengthMax = 0
  LengthMin = 0
  Placement1 = pos=(6110,-2.125e-13,-3.0695e-12) rot=(-0.707107,0,-0.707107;3.14159rad)
  Placement2 = pos=(-3.411e-13,-542,1.027e-13) rot=(-1,0,0;1.5708rad)
  Reference1 = -> Part036 [Assembly.K_Straight_tube.Edge17,Assembly.K_Straight_tube.Edge17]
  Reference2 = -> Part036 [Assembly.K_5Elbow.Edge17,Assembly.K_5Elbow.Edge17]
FEATURE [Part::FeaturePython] Single_Flange_Length_Tube  # WARN: FeaturePython — macro-defined, semantics opaque (R4)
  Fittings = 01_Single Flange Length Tube
  L0 = 1250
  Placement = pos=(9274.48,1.33348e-05,310.648) rot=(-0.049068,0,0.998795;3.14159rad)
  dia = 7
FEATURE [App::FeaturePython] Joint004  label="Fixed004"  # Assembly joint (typed FeaturePython)
  Activated = true
  AngleMax = 0
  AngleMin = 0
  Detach1 = false
  Detach2 = false
  Distance = 0
  Distance2 = 0
  EnableAngleMax = false
  EnableAngleMin = false
  EnableLengthMax = false
  EnableLengthMin = false
  JointType = 0 (Fixed)
  LengthMax = 0
  LengthMin = 0
  Placement1 = pos=(1250,-4.37e-14,2.274e-13) rot=(-0.707107,0,-0.707107;3.14159rad)
  Placement2 = pos=(110,-4.3e-15,-1.137e-13) rot=(-0.707107,0,-0.707107;3.14159rad)
  Reference1 = -> Part036 [Assembly.Single_Flange_Length_Tube.Edge22,Assembly.Single_Flange_Length_Tube.Edge22]
  Reference2 = -> Part036 [Assembly.K_Straight_tube.Edge11,Assembly.K_Straight_tube.Edge11]
FEATURE [Assembly::JointGroup] Joints
  Group = -> [GroundedJoint,Joint,Joint001,Joint002,Joint003,Joint004]
FEATURE [Assembly::AssemblyObject] Assembly  label="inflow"
  Group = -> [Joints,Flange_Reducer,GroundedJoint,F90Elbow,Joint,K_Short_tube_No_1th,Joint001,K_5Elbow,Joint002,K_Straight_tube,Joint003,Single_Flange_Length_Tube,Joint004]
  Origin = -> Origin088
  Type = Assembly
  mass = 1694.36
FEATURE [Part::Feature] Part__Feature030  label="body"
  shape: bbox 18720 x 18750 x 6460 mm, 75 faces, 3 solids (baked)
FEATURE [Part::Part2DObjectPython] Rectangle  # Draft 2D object (typed FeaturePython)
  Area = 1.73732e+08
  ChamferSize = 0
  Columns = 1
  FilletRadius = 0
  Height = 8623.96
  Length = 20145.3
  MakeFace = true
  Placement = pos=(-9461.69,4.37e-13,-1792.21) rot=(1,0,0;1.5708rad)
  Rows = 1
FEATURE [Part::FeaturePython] Slice  # WARN: FeaturePython — macro-defined, semantics opaque (R4)
  Base = -> Part__Feature030
  Mode = 1
  Tolerance = 0
  Tools = -> [Rectangle]
FEATURE [Part::FeaturePython] Slice_child0  label="Slice.0"  # WARN: FeaturePython — macro-defined, semantics opaque (R4)
  Base = -> Slice
  FilterType = 1
  Invert = false
  OverrideMaxVal = 0
  WindowFrom = 80
  WindowTo = 100
  items = 0
FEATURE [Part::FeaturePython] Slice_child1  label="Slice.1"  # WARN: FeaturePython — macro-defined, semantics opaque (R4)
  Base = -> Slice
  FilterType = 1
  Invert = false
  OverrideMaxVal = 0
  WindowFrom = 80
  WindowTo = 100
  items = 1
FEATURE [App::DocumentObjectGroup] GrExplode_Slice  label="Exploded Slice"
  Group = -> [Slice_child0,Slice_child1]
FEATURE [App::Part] Part061  label="body16.5m"
  Group = -> [Part__Feature030,Rectangle,Slice,Slice_child0,Slice_child1,GrExplode_Slice]
  Origin = -> Origin089
FEATURE [Sketcher::SketchObject] Sketch
  ArcFitTolerance = 0
  FullyConstrained = true
  MakeInternals = false
  Placement = pos=(0,0,0) rot=(1,0,0;1.5708rad)
  expr: Constraints[11] = Spreadsheet.dia / 2
  expr: Constraints[9] = Spreadsheet.h0
  sketch-geometry (4):
    g0: LineSegment StartX=1645 StartY=0 StartZ=0 EndX=1650 EndY=0 EndZ=0
    g1: LineSegment StartX=1650 StartY=0 StartZ=0 EndX=1650 EndY=1920 EndZ=0
    g2: LineSegment StartX=1650 StartY=1920 StartZ=0 EndX=1645 EndY=1920 EndZ=0
    g3: LineSegment StartX=1645 StartY=1920 StartZ=0 EndX=1645 EndY=0 EndZ=0
  constraints (12):
    c: Coincident(g0,g1)
    c: Coincident(g1,g2)
    c: Coincident(g2,g3)
    c: Coincident(g3,g0)
    c: Horizontal(g0)
    c: Horizontal(g2)
    c: Vertical(g1)
    c: Vertical(g3)
    c: DistanceX(g2,g2) = 5
    c: DistanceY(g1,g1) = 1920
    c: PointOnObject(g0,g-1)
    c: DistanceX(g-1,g0) = 1650
FEATURE [Part::Revolution] Revolve
  Angle = 360
  Axis = (0,0,1)
  Base = (0,0,0)
  FaceMakerClass = Part::FaceMakerBullseye
  Solid = true
  Source = -> Sketch
  Symmetric = false
FEATURE [Part::FeaturePython] AngleSteel018  label="AngleSteel020"  # WARN: FeaturePython — macro-defined, semantics opaque (R4)
  A = 75
  B = 75
  L = 1000
  Placement = pos=(1650,0,0) rot=(0,0,1;0rad)
  Solid = false
  g0 = 7.85
  mass = 0
  size = 10
  standard = SS_Equal
  t = 6
  expr: .Placement.Base.x = Spreadsheet.dia / 2
FEATURE [Part::Revolution] Revolve016
  Angle = 360
  Axis = (0,0,1)
  Base = (0,0,0)
  FaceMakerClass = Part::FaceMakerBullseye
  Solid = false
  Source = -> AngleSteel018
  Symmetric = false
FEATURE [Part::FeaturePython] AngleSteel019  label="AngleSteel021"  # WARN: FeaturePython — macro-defined, semantics opaque (R4)
  A = 75
  B = 75
  L = 1000
  Placement = pos=(1650,0,1920) rot=(0,1,0;1.5708rad)
  Solid = false
  g0 = 7.85
  mass = 0
  size = 10
  standard = SS_Equal
  t = 6
  expr: .Placement.Base.x = Spreadsheet.dia / 2
  expr: .Placement.Base.z = Spreadsheet.h0
FEATURE [Part::Revolution] Revolve017
  Angle = 360
  Axis = (0,0,1)
  Base = (0,0,0)
  FaceMakerClass = Part::FaceMakerBullseye
  Solid = false
  Source = -> AngleSteel019
  Symmetric = false
FEATURE [Sketcher::SketchObject] Sketch001
  ArcFitTolerance = 0
  FullyConstrained = true
  MakeInternals = false
  Placement = pos=(0,0,0) rot=(1,0,0;1.5708rad)
  sketch-geometry (4):
    g0: LineSegment StartX=-275 StartY=1400 StartZ=0 EndX=275 EndY=1400 EndZ=0
    g1: LineSegment StartX=275 StartY=1400 StartZ=0 EndX=275 EndY=1920 EndZ=0
    g2: LineSegment StartX=275 StartY=1920 StartZ=0 EndX=-275 EndY=1920 EndZ=0
    g3: LineSegment StartX=-275 StartY=1920 StartZ=0 EndX=-275 EndY=1400 EndZ=0
  constraints (12):
    c: Coincident(g0,g1)
    c: Coincident(g1,g2)
    c: Coincident(g2,g3)
    c: Coincident(g3,g0)
    c: Horizontal(g0)
    c: Horizontal(g2)
    c: Vertical(g1)
    c: Vertical(g3)
    c: DistanceX(g0,g0) = 550
    c: DistanceY(g1,g1) = 520
    c: PointOnObject(g1,g-3)
    c: DistanceX(g-1,g0) = 275
FEATURE [Part::Extrusion] Extrude
  Base = -> Sketch001
  Dir = (0,-1,2e-16)
  DirMode = 2
  FaceMakerClass = Part::FaceMakerBullseye
  FaceMakerMode = 3
  LengthFwd = 2500
  LengthRev = 0
  Solid = true
  Symmetric = false
FEATURE [Part::MultiFuse] Fusion  label="Fusion004"
  Shapes = -> [Revolve,Revolve016,Revolve017]
FEATURE [Part::Cut] Cut
  Base = -> Fusion
  Tool = -> Extrude
FEATURE [Sketcher::SketchObject] Sketch002
  ArcFitTolerance = 0
  FullyConstrained = true
  MakeInternals = false
  MapMode = 5
  Placement = pos=(0,3.48e-13,0) rot=(0,0,1;0rad)
  sketch-geometry (4):
    g0: LineSegment StartX=-275 StartY=-1260.58 StartZ=0 EndX=-275 EndY=-1290.58 EndZ=0
    g1: LineSegment StartX=-275 StartY=-1260.58 StartZ=0 EndX=275 EndY=-1260.58 EndZ=0
    g2: LineSegment StartX=275 StartY=-1260.58 StartZ=0 EndX=275 EndY=-1290.58 EndZ=0
    g3: ArcOfCircle CenterX=0 CenterY=0 CenterZ=0 NormalX=0 NormalY=0 NormalZ=1 AngleXU=0 Radius=1319.55 StartAngle=4.50245 EndAngle=4.92233
  constraints (13):
    c: Vertical(g0)
    c: Coincident(g0,g1)
    c: Horizontal(g1)
    c: Coincident(g1,g2)
    c: Vertical(g2)
    c: Coincident(g3,g0)
    c: Coincident(g3,g2)
    c: PointOnObject(g-3,g0)
    c: PointOnObject(g-4,g2)
    c: DistanceY(g-3,g0) = 10
    c: DistanceY(g0,g0) = 30
    c: Coincident(g3,g-1)
    c: DistanceY(g-1,g1) = -1260.58  'brg'
FEATURE [Part::Extrusion] Extrude001
  Base = -> Sketch002
  Dir = (0,0,1)
  DirMode = 2
  FaceMakerClass = Part::FaceMakerBullseye
  FaceMakerMode = 3
  LengthFwd = 5
  LengthRev = 0
  Placement = pos=(0,-350,1400) rot=(0,0,1;0rad)
  Solid = true
  Symmetric = false
  expr: .Placement.Base.y = -(<<Spreadsheet_feedWell>>.dia - 2600) / 2
  expr: .Placement.Base.z = <<Spreadsheet_feedWell>>.h0 - 520
FEATURE [Sketcher::SketchObject] Sketch087
  ArcFitTolerance = 0
  ExternalGeometry = -> [Extrude001]
  FullyConstrained = true
  MakeInternals = false
  MapMode = 5
  Placement = pos=(0,7.323e-12,1405) rot=(0,0,1;0rad)
  expr: .Placement.Base.z = <<Spreadsheet_feedWell>>.h0 - 520 + 5
  sketch-geometry (4):
    g0: LineSegment StartX=-275 StartY=-1625.58 StartZ=0 EndX=275 EndY=-1625.58 EndZ=0
    g1: LineSegment StartX=275 StartY=-1625.58 StartZ=0 EndX=275 EndY=-1615.58 EndZ=0
    g2: LineSegment StartX=275 StartY=-1615.58 StartZ=0 EndX=-275 EndY=-1615.58 EndZ=0
    g3: LineSegment StartX=-275 StartY=-1615.58 StartZ=0 EndX=-275 EndY=-1625.58 EndZ=0
  constraints (12):
    c: Coincident(g0,g1)
    c: Coincident(g1,g2)
    c: Coincident(g2,g3)
    c: Coincident(g3,g0)
    c: Horizontal(g0)
    c: Horizontal(g2)
    c: Vertical(g1)
    c: Vertical(g3)
    c: DistanceY(g1,g-3) = 5
    c: DistanceY(g1,g1) = 10
    c: PointOnObject(g1,g-4)
    c: PointOnObject(g2,g-5)
FEATURE [Part::Extrusion] Extrude002
  Base = -> Sketch087
  Dir = (0,0,1)
  DirMode = 2
  FaceMakerClass = Part::FaceMakerBullseye
  FaceMakerMode = 3
  LengthFwd = 515
  LengthRev = 0
  Solid = true
  Symmetric = false
FEATURE [Sketcher::SketchObject] Sketch004
  ArcFitTolerance = 0
  FullyConstrained = true
  MakeInternals = false
  MapMode = 5
  Placement = pos=(0,-2500,7.07e-12) rot=(1,0,0;1.5708rad)
  sketch-geometry (4):
    g0: LineSegment StartX=-170 StartY=1920 StartZ=0 EndX=-170 EndY=1680 EndZ=0
    g1: ArcOfCircle CenterX=0 CenterY=1680 CenterZ=0 NormalX=0 NormalY=0 NormalZ=1 AngleXU=0 Radius=170 StartAngle=3.14159 EndAngle=6.28318
    g2: LineSegment StartX=170 StartY=1680 StartZ=0 EndX=170 EndY=1920 EndZ=0
    g3: LineSegment StartX=170 StartY=1920 StartZ=0 EndX=-170 EndY=1920 EndZ=0
  constraints (12):
    c: Vertical(g0)
    c: Tangent(g0,g1) = -1.5708
    c: Coincident(g1,g2)
    c: Vertical(g2)
    c: Coincident(g2,g3)
    c: Coincident(g3,g0)
    c: Horizontal(g3)
    c: Radius(g1) = 170
    c: DistanceX(g-2,g1) = 170
    c: PointOnObject(g2,g-3)
    c: Distance(g1,g3) = 240
    c: PointOnObject(g1,g-2)
FEATURE [Part::Extrusion] Extrude072
  Base = -> Sketch004
  Dir = (0,-1,6.1e-15)
  DirMode = 2
  FaceMakerClass = Part::FaceMakerBullseye
  FaceMakerMode = 3
  LengthFwd = 1000
  LengthRev = 0
  Reversed = true
  Solid = true
  Symmetric = false
FEATURE [Part::Cut] Cut001
  Base = -> Extrude002
  Tool = -> Extrude072
FEATURE [Sketcher::SketchObject] Sketch005
  ArcFitTolerance = 0
  FullyConstrained = true
  MakeInternals = false
  MapMode = 5
  Placement = pos=(0,-2500,7.07e-12) rot=(1,0,0;1.5708rad)
  sketch-geometry (9):
    g0: Circle CenterX=-200 CenterY=1730 CenterZ=0 NormalX=0 NormalY=0 NormalZ=1 AngleXU=0 Radius=6
    g1: Circle CenterX=-200 CenterY=1870 CenterZ=0 NormalX=0 NormalY=0 NormalZ=1 AngleXU=0 Radius=6
    g2: Circle CenterX=200 CenterY=1870 CenterZ=0 NormalX=0 NormalY=0 NormalZ=1 AngleXU=0 Radius=6
    g3: Circle CenterX=200 CenterY=1730 CenterZ=0 NormalX=0 NormalY=0 NormalZ=1 AngleXU=0 Radius=6
    g4: Circle CenterX=-200 CenterY=1630 CenterZ=0 NormalX=0 NormalY=0 NormalZ=1 AngleXU=0 Radius=6
    g5: Circle CenterX=-200 CenterY=1460 CenterZ=0 NormalX=0 NormalY=0 NormalZ=1 AngleXU=0 Radius=6
    g6: Circle CenterX=200 CenterY=1630 CenterZ=0 NormalX=0 NormalY=0 NormalZ=1 AngleXU=0 Radius=6
    g7: Circle CenterX=200 CenterY=1460 CenterZ=0 NormalX=0 NormalY=0 NormalZ=1 AngleXU=0 Radius=6
    g8: Circle CenterX=0 CenterY=1460 CenterZ=0 NormalX=0 NormalY=0 NormalZ=1 AngleXU=0 Radius=6
  constraints (26):
    c: Radius(g0) = 6
    c: DistanceY(g-3,g0) = 50
    c: Radius(g1) = 6
    c: Vertical(g0,g1)
    c: Equal(g0,g3) = 6
    c: Equal(g1,g2) = 6
    c: Vertical(g3,g2)
    c: Radius(g4) = 6
    c: Equal(g4,g5) = 6
    c: DistanceY(g5,g4) = 170
    c: Vertical(g5,g4)
    c: Equal(g4,g6) = 6
    c: Equal(g6,g7) = 6
    c: DistanceY(g7,g6) = 170
    c: Vertical(g7,g6)
    c: PointOnObject(g8,g-2)
    c: Radius(g8) = 6
    c: Horizontal(g8,g5)
    c: DistanceY(g4,g-3) = 50
    c: Symmetric(g4,g6,g-2)
    c: Vertical(g4,g0)
    c: DistanceX(g5,g7) = 400
    c: DistanceY(g0,g1) = 140
    c: Horizontal(g0,g3)
    c: Horizontal(g1,g2)
    c: Vertical(g6,g3)
FEATURE [Part::Extrusion] Extrude004
  Base = -> Sketch005
  Dir = (0,-1,6.1e-15)
  DirMode = 2
  FaceMakerClass = Part::FaceMakerBullseye
  FaceMakerMode = 3
  LengthFwd = 1000
  LengthRev = 0
  Reversed = true
  Solid = true
  Symmetric = false
FEATURE [Part::Cut] Cut002
  Base = -> Cut001
  Tool = -> Extrude004
FEATURE [Spreadsheet::Sheet] Spreadsheet  label="Spreadsheet_feedWell"
  cells = A2='tankDia   D0; B2(D0)=16500; A3='depth of water  hw; B3(hw)=3200; A4='feedWell dia  dia; B4(dia)==D0 * 0.2; A5='feedWell hight  h0; B5(h0)==hw * 0.6; A6='bracket hight h1; B6(h1)=1000; A7='bracket angle ba; B7(ba)=0
FEATURE [Sketcher::SketchObject] Sketch006
  ArcFitTolerance = 0
  FullyConstrained = false
  MakeInternals = false
  Placement = pos=(0,0,0) rot=(1,0,0;1.5708rad)
  sketch-geometry (23):
    g0: LineSegment StartX=-235 StartY=2.04e-14 StartZ=0 EndX=-166.5 EndY=2.04e-14 EndZ=0
    g1: LineSegment StartX=235 StartY=0 StartZ=0 EndX=235 EndY=240 EndZ=0
    g2: LineSegment StartX=235 StartY=240 StartZ=0 EndX=-235 EndY=240 EndZ=0
    g3: LineSegment StartX=-235 StartY=240 StartZ=0 EndX=-235 EndY=2.84e-14 EndZ=0
    g4: ArcOfCircle CenterX=0 CenterY=0 CenterZ=0 NormalX=0 NormalY=0 NormalZ=1 AngleXU=0 Radius=166.5 StartAngle=0 EndAngle=3.14159
    g5: ArcOfCircle CenterX=200 CenterY=200 CenterZ=0 NormalX=0 NormalY=0 NormalZ=1 AngleXU=0 Radius=7 StartAngle=-9e-16 EndAngle=3.14159
    g6: ArcOfCircle CenterX=200 CenterY=180 CenterZ=0 NormalX=0 NormalY=0 NormalZ=1 AngleXU=0 Radius=7 StartAngle=3.14159 EndAngle=6.28319
    g7: LineSegment StartX=193 StartY=200 StartZ=0 EndX=193 EndY=180 EndZ=0
    g8: LineSegment StartX=207 StartY=180 StartZ=0 EndX=207 EndY=200 EndZ=0
    g9: ArcOfCircle CenterX=200 CenterY=60 CenterZ=0 NormalX=0 NormalY=0 NormalZ=1 AngleXU=0 Radius=7 StartAngle=0 EndAngle=3.14159
    g10: ArcOfCircle CenterX=200 CenterY=40 CenterZ=0 NormalX=0 NormalY=0 NormalZ=1 AngleXU=0 Radius=7 StartAngle=3.14159 EndAngle=6.28319
    g11: LineSegment StartX=193 StartY=60 StartZ=0 EndX=193 EndY=40 EndZ=0
    g12: LineSegment StartX=207 StartY=40 StartZ=0 EndX=207 EndY=60 EndZ=0
    g13: ArcOfCircle CenterX=-200 CenterY=200.393 CenterZ=0 NormalX=0 NormalY=0 NormalZ=1 AngleXU=0 Radius=7 StartAngle=3e-16 EndAngle=3.14159
    g14: ArcOfCircle CenterX=-200 CenterY=180.393 CenterZ=0 NormalX=0 NormalY=0 NormalZ=1 AngleXU=0 Radius=7 StartAngle=3.14159 EndAngle=6.28319
    g15: LineSegment StartX=-207 StartY=200.393 StartZ=0 EndX=-207 EndY=180.393 EndZ=0
    g16: LineSegment StartX=-193 StartY=180.393 StartZ=0 EndX=-193 EndY=200.393 EndZ=0
    g17: ArcOfCircle CenterX=-200 CenterY=60.3929 CenterZ=0 NormalX=0 NormalY=0 NormalZ=1 AngleXU=0 Radius=7 StartAngle=0 EndAngle=3.14159
    g18: ArcOfCircle CenterX=-200 CenterY=40.3929 CenterZ=0 NormalX=0 NormalY=0 NormalZ=1 AngleXU=0 Radius=7 StartAngle=3.14159 EndAngle=6.28319
    g19: LineSegment StartX=-207 StartY=60.3929 StartZ=0 EndX=-207 EndY=40.3929 EndZ=0
    g20: LineSegment StartX=-193 StartY=40.3929 StartZ=0 EndX=-193 EndY=60.3929 EndZ=0
    g21: LineSegment [constr] StartX=207.004 StartY=200.734 StartZ=0 EndX=-193 EndY=200.393 EndZ=0
    g22: LineSegment StartX=166.5 StartY=0 StartZ=0 EndX=235 EndY=0 EndZ=0
  constraints (58):
    c: Coincident(g22,g1)
    c: Coincident(g1,g2)
    c: Coincident(g2,g3)
    c: Coincident(g3,g0)
    c: Horizontal(g0)
    c: Vertical(g1)
    c: Vertical(g3)
    c: PointOnObject(g0,g-1)
    c: Coincident(g4,g-1)
    c: Radius(g4) = 166.5
    c: DistanceX(g2,g2) = 470
    c: Symmetric(g1,g2,g-2)
    c: DistanceY(g1,g1) = 240
    c: DistanceX(g5,g5) = 14
    c: DistanceY(g7,g7) = 20
    c: DistanceY(g5,g1) = 40
    c: DistanceX(g4,g5) = 200
    c: Tangent(g9,g11) = -1.5708
    c: Tangent(g11,g10) = -1.5708
    c: Tangent(g10,g12) = -1.5708
    c: Tangent(g12,g9) = -1.5708
    c: Equal(g9,g10)
    c: Vertical(g11)
    c: Equal(g5,g9) = 14
    c: Equal(g7,g11) = 20
    c: Vertical(g9,g6)
    c: DistanceY(g9,g5) = 140
    c: Equal(g5,g13) = 14
    c: Equal(g7,g15) = 20
    c: Tangent(g17,g19) = -1.5708
    c: Tangent(g19,g18) = -1.5708
    c: Tangent(g18,g20) = -1.5708
    c: Tangent(g20,g17) = -1.5708
    c: Equal(g17,g18)
    c: Vertical(g19)
    c: Equal(g13,g17) = 14
    c: Equal(g15,g19) = 20
    c: Vertical(g17,g14)
    c: DistanceY(g17,g13) = 140
    c: Angle(g21) = -3.14074
    c: Coincident(g0,g4)
    c: Coincident(g22,g4)
    c: Horizontal(g22)
    c: PointOnObject(g1,g-1)
    c: Vertical(g16)
    c: Vertical(g15)
    c: Coincident(g13,g21)
    c: Tangent(g5,g8) = -1.5708
    c: Tangent(g16,g13) = -1.5708
    c: Tangent(g15,g14) = -1.5708
    c: Tangent(g16,g14) = -1.5708
    c: Tangent(g15,g13) = -1.5708
    c: DistanceX(g13,g4) = 200
    c: Vertical(g8)
    c: Vertical(g7)
    c: Tangent(g5,g7) = -1.5708
    c: Tangent(g7,g6) = -1.5708
    c: Tangent(g8,g6) = -1.5708
FEATURE [Part::Extrusion] Extrude005
  Base = -> Sketch006
  Dir = (0,-1,2e-16)
  DirMode = 2
  FaceMakerClass = Part::FaceMakerBullseye
  FaceMakerMode = 3
  LengthFwd = 10
  LengthRev = 0
  Solid = true
  Symmetric = false
FEATURE [Sketcher::SketchObject] Sketch007
  ArcFitTolerance = 0
  ExternalGeometry = -> [Extrude005]
  FullyConstrained = false
  MakeInternals = false
  Placement = pos=(0,0,0) rot=(1,0,0;1.5708rad)
  sketch-geometry (26):
    g0: LineSegment StartX=-235 StartY=0 StartZ=0 EndX=-166.5 EndY=-2.04e-14 EndZ=0
    g1: LineSegment StartX=235 StartY=0 StartZ=0 EndX=235 EndY=-267.623 EndZ=0
    g2: LineSegment StartX=235 StartY=-267.623 StartZ=0 EndX=-235 EndY=-267.623 EndZ=0
    g3: LineSegment StartX=-235 StartY=-267.623 StartZ=0 EndX=-235 EndY=0 EndZ=0
    g4: ArcOfCircle CenterX=0 CenterY=-2.04e-14 CenterZ=0 NormalX=0 NormalY=0 NormalZ=1 AngleXU=0 Radius=166.5 StartAngle=3.14159 EndAngle=6.28319
    g5: ArcOfCircle CenterX=200 CenterY=-40 CenterZ=0 NormalX=0 NormalY=0 NormalZ=1 AngleXU=0 Radius=7 StartAngle=3e-16 EndAngle=3.14159
    g6: ArcOfCircle CenterX=200 CenterY=-60 CenterZ=0 NormalX=0 NormalY=0 NormalZ=1 AngleXU=0 Radius=7 StartAngle=3.14159 EndAngle=6.28319
    g7: LineSegment StartX=193 StartY=-40 StartZ=0 EndX=193 EndY=-60 EndZ=0
    g8: LineSegment StartX=207 StartY=-60 StartZ=0 EndX=207 EndY=-40 EndZ=0
    g9: ArcOfCircle CenterX=200 CenterY=-210 CenterZ=0 NormalX=0 NormalY=0 NormalZ=1 AngleXU=0 Radius=7 StartAngle=0 EndAngle=3.14159
    g10: ArcOfCircle CenterX=200 CenterY=-230 CenterZ=0 NormalX=0 NormalY=0 NormalZ=1 AngleXU=0 Radius=7 StartAngle=3.14159 EndAngle=6.28319
    g11: LineSegment StartX=193 StartY=-210 StartZ=0 EndX=193 EndY=-230 EndZ=0
    g12: LineSegment StartX=207 StartY=-230 StartZ=0 EndX=207 EndY=-210 EndZ=0
    g13: ArcOfCircle CenterX=-200 CenterY=-40 CenterZ=0 NormalX=0 NormalY=0 NormalZ=1 AngleXU=0 Radius=7 StartAngle=0 EndAngle=3.14159
    g14: ArcOfCircle CenterX=-200 CenterY=-60 CenterZ=0 NormalX=0 NormalY=0 NormalZ=1 AngleXU=0 Radius=7 StartAngle=3.14159 EndAngle=6.28319
    g15: LineSegment StartX=-207 StartY=-40 StartZ=0 EndX=-207 EndY=-60 EndZ=0
    g16: LineSegment StartX=-193 StartY=-60 StartZ=0 EndX=-193 EndY=-40 EndZ=0
    g17: ArcOfCircle CenterX=-200 CenterY=-210 CenterZ=0 NormalX=0 NormalY=0 NormalZ=1 AngleXU=0 Radius=7 StartAngle=1.4e-15 EndAngle=3.14159
    g18: ArcOfCircle CenterX=-200 CenterY=-230 CenterZ=0 NormalX=0 NormalY=0 NormalZ=1 AngleXU=0 Radius=7 StartAngle=3.14159 EndAngle=6.28319
    g19: LineSegment StartX=-207 StartY=-210 StartZ=0 EndX=-207 EndY=-230 EndZ=0
    g20: LineSegment StartX=-193 StartY=-230 StartZ=0 EndX=-193 EndY=-210 EndZ=0
    g21: LineSegment StartX=166.5 StartY=-2.04e-14 StartZ=0 EndX=235 EndY=0 EndZ=0
    g22: ArcOfCircle CenterX=0 CenterY=-210 CenterZ=0 NormalX=0 NormalY=0 NormalZ=1 AngleXU=0 Radius=7 StartAngle=-9e-16 EndAngle=3.14159
    g23: ArcOfCircle CenterX=0 CenterY=-230 CenterZ=0 NormalX=0 NormalY=0 NormalZ=1 AngleXU=0 Radius=7 StartAngle=3.14159 EndAngle=6.28319
    g24: LineSegment StartX=-7 StartY=-210 StartZ=0 EndX=-7 EndY=-230 EndZ=0
    g25: LineSegment StartX=7 StartY=-230 StartZ=0 EndX=7 EndY=-210 EndZ=0
  constraints (65):
    c: Coincident(g21,g1)
    c: Coincident(g1,g2)
    c: Coincident(g2,g3)
    c: Coincident(g3,g0)
    c: Horizontal(g2)
    c: Vertical(g1)
    c: Vertical(g3)
    c: Coincident(g21,g-3)
    c: Coincident(g0,g-4)
    c: Coincident(g4,g-1)
    c: Horizontal(g4,g4)
    c: Horizontal(g4,g4)
    c: Tangent(g5,g7) = -1.5708
    c: Tangent(g7,g6) = -1.5708
    c: Tangent(g6,g8) = -1.5708
    c: Tangent(g8,g5) = -1.5708
    c: Equal(g5,g6)
    c: Vertical(g7)
    c: DistanceY(g8,g8) = 20
    c: DistanceX(g5,g5) = 14
    c: Vertical(g5,g-5)
    c: DistanceY(g5,g4) = 40
    c: Tangent(g9,g11) = -1.5708
    c: Tangent(g11,g10) = -1.5708
    c: Tangent(g10,g12) = -1.5708
    c: Tangent(g12,g9) = -1.5708
    c: Equal(g9,g10)
    c: Vertical(g11)
    c: Equal(g8,g12) = 20
    c: Equal(g5,g9) = 14
    c: Vertical(g6,g9)
    c: Tangent(g13,g15) = -1.5708
    c: Tangent(g15,g14) = -1.5708
    c: Tangent(g14,g16) = -1.5708
    c: Tangent(g16,g13) = -1.5708
    c: Equal(g13,g14)
    c: Vertical(g15)
    c: Equal(g8,g16) = 20
    c: Equal(g5,g13) = 14
    c: Tangent(g17,g19) = -1.5708
    c: Tangent(g19,g18) = -1.5708
    c: Tangent(g18,g20) = -1.5708
    c: Tangent(g20,g17) = -1.5708
    c: Equal(g17,g18)
    c: Vertical(g19)
    c: Equal(g16,g20) = 20
    c: Equal(g13,g17) = 14
    c: Vertical(g14,g17)
    c: Tangent(g22,g24) = -1.5708
    c: Tangent(g24,g23) = -1.5708
    c: Tangent(g23,g25) = -1.5708
    c: Tangent(g25,g22) = -1.5708
    c: Equal(g22,g23)
    c: Vertical(g24)
    c: DistanceX(g22,g22) = 14
    c: DistanceY(g24,g24) = 20
    c: PointOnObject(g22,g-2)
    c: Horizontal(g9,g22)
    c: DistanceY(g9,g5) = 170
    c: DistanceY(g17,g13) = 170
    c: DistanceX(g14,g6) = 400
    c: DistanceY(g13,g0) = 40
    c: Coincident(g0,g4)
    c: Coincident(g4,g21)
    c: Radius(g4) = 166.5
FEATURE [Part::Extrusion] Extrude006
  Base = -> Sketch007
  Dir = (0,-1,2e-16)
  DirMode = 2
  FaceMakerClass = Part::FaceMakerBullseye
  FaceMakerMode = 3
  LengthFwd = 10
  LengthRev = 0
  Solid = true
  Symmetric = false
FEATURE [App::Part] Part  label="pipeBrg"
  Group = -> [Sketch006,Sketch007,Extrude005,Extrude006]
  Origin = -> Origin
  Placement = pos=(0,-1625.6,1680) rot=(0,0,1;0rad)
  expr: .Placement.Base.y = -<<Spreadsheet_feedWell>>.dia / 2 + 24.4
  expr: .Placement.Base.z = <<Spreadsheet_feedWell>>.h0 - 260 + 20
FEATURE [Sketcher::SketchObject] Sketch008
  ArcFitTolerance = 0
  FullyConstrained = false
  MakeInternals = false
  sketch-geometry (4):
    g0: LineSegment StartX=1299.04 StartY=50 StartZ=0 EndX=1507.04 EndY=50 EndZ=0
    g1: LineSegment StartX=1507.04 StartY=50 StartZ=0 EndX=1507.04 EndY=-50 EndZ=0
    g2: LineSegment StartX=1507.04 StartY=-50 StartZ=0 EndX=1299.04 EndY=-50 EndZ=0
    g3: ArcOfCircle CenterX=-0.0298456 CenterY=4.574e-13 CenterZ=0 NormalX=0 NormalY=0 NormalZ=1 AngleXU=0 Radius=1300.03 StartAngle=6.24472 EndAngle=6.32166
  constraints (12):
    c: Horizontal(g0)
    c: Coincident(g0,g1)
    c: Vertical(g1)
    c: Coincident(g1,g2)
    c: Horizontal(g2)
    c: DistanceY(g-1,g0) = 50
    c: DistanceY(g1,g1) = 100
    c: Coincident(g3,g2)
    c: Coincident(g3,g0)
    c: PointOnObject(g0,g-5)
    c: PointOnObject(g2,g-6)
    c: DistanceX(g0,g0) = 208
FEATURE [Part::Extrusion] Extrude007
  Base = -> Sketch008
  Dir = (0,0,1)
  DirMode = 2
  FaceMakerClass = Part::FaceMakerBullseye
  FaceMakerMode = 3
  LengthFwd = 10
  LengthRev = 0
  Solid = true
  Symmetric = false
FEATURE [Sketcher::SketchObject] Sketch009
  ArcFitTolerance = 0
  ExternalGeometry = -> [Extrude007]
  FullyConstrained = true
  MakeInternals = false
  MapMode = 5
  Placement = pos=(0,0,10) rot=(0,0,1;0rad)
  sketch-geometry (8):
    g0: LineSegment StartX=1299.04 StartY=50 StartZ=0 EndX=1507.04 EndY=50 EndZ=0
    g1: LineSegment StartX=1507.04 StartY=50 StartZ=0 EndX=1507.04 EndY=45 EndZ=0
    g2: LineSegment StartX=1507.04 StartY=45 StartZ=0 EndX=1299.04 EndY=45 EndZ=0
    g3: LineSegment StartX=1299.04 StartY=45 StartZ=0 EndX=1299.04 EndY=50 EndZ=0
    g4: LineSegment StartX=1299.04 StartY=-50 StartZ=0 EndX=1507.04 EndY=-50 EndZ=0
    g5: LineSegment StartX=1507.04 StartY=-50 StartZ=0 EndX=1507.04 EndY=-45 EndZ=0
    g6: LineSegment StartX=1507.04 StartY=-45 StartZ=0 EndX=1299.04 EndY=-45 EndZ=0
    g7: LineSegment StartX=1299.04 StartY=-45 StartZ=0 EndX=1299.04 EndY=-50 EndZ=0
  constraints (22):
    c: Coincident(g0,g1)
    c: Coincident(g1,g2)
    c: Coincident(g2,g3)
    c: Coincident(g3,g0)
    c: Horizontal(g0)
    c: Horizontal(g2)
    c: Vertical(g1)
    c: Vertical(g3)
    c: Coincident(g4,g5)
    c: Coincident(g5,g6)
    c: Coincident(g6,g7)
    c: Coincident(g7,g4)
    c: Horizontal(g4)
    c: Horizontal(g6)
    c: Vertical(g5)
    c: Vertical(g7)
    c: Coincident(g0,g-3)
    c: DistanceY(g1,g1) = 5
    c: DistanceY(g5,g5) = 5
    c: Coincident(g4,g-3)
    c: Vertical(g2,g6)
    c: PointOnObject(g4,g-4)
FEATURE [Part::Extrusion] Extrude008
  Base = -> Sketch009
  Dir = (0,0,1)
  DirMode = 2
  FaceMakerClass = Part::FaceMakerBullseye
  FaceMakerMode = 3
  LengthFwd = 200
  LengthRev = 0
  Solid = true
  Symmetric = false
FEATURE [Part::Chamfer] Chamfer001
  Base = -> Extrude008
  EdgeLinks = -> Extrude008 [Edge7,Edge19]
  Edges = 2 edges: [Edge7 r1=130 r2=70,Edge19 r1=130 r2=70]
FEATURE [Part::Compound] Compound002  label="gusset"
  Links = -> [Extrude007,Chamfer001]
FEATURE [Sketcher::SketchObject] Sketch088
  ArcFitTolerance = 0
  ExternalGeometry = -> [Compound002]
  FullyConstrained = true
  MakeInternals = false
  MapMode = 5
  Placement = pos=(0,0,10) rot=(0,0,1;0rad)
  sketch-geometry (1):
    g0: Circle CenterX=1532.04 CenterY=0 CenterZ=0 NormalX=0 NormalY=0 NormalZ=1 AngleXU=0 Radius=7
  constraints (3):
    c: Diameter(g0) = 14
    c: PointOnObject(g0,g-1)
    c: Distance(g0,g-3) = 25
FEATURE [Part::Extrusion] Extrude009
  Base = -> Sketch088
  Dir = (0,0,1)
  DirMode = 2
  FaceMakerClass = Part::FaceMakerBullseye
  FaceMakerMode = 3
  LengthFwd = 10
  LengthRev = 0
  Reversed = true
  Solid = true
  Symmetric = false
FEATURE [Part::Cut] Cut003
  Base = -> Compound002
  Placement = pos=(350,0,998.5) rot=(0,0,1;0rad)
  Tool = -> Extrude009
  expr: .Placement.Base.x = (<<Spreadsheet_feedWell>>.dia - 2600) / 2
  expr: .Placement.Base.z = Spreadsheet.h1 - 1.5
FEATURE [Sketcher::SketchObject] Sketch014
  ArcFitTolerance = 0
  FullyConstrained = true
  MakeInternals = false
  Placement = pos=(0,0,0) rot=(1,0,0;1.5708rad)
  sketch-geometry (4):
    g0: LineSegment StartX=0 StartY=0 StartZ=0 EndX=150 EndY=0 EndZ=0
    g1: LineSegment StartX=150 StartY=0 StartZ=0 EndX=150 EndY=300 EndZ=0
    g2: LineSegment StartX=150 StartY=300 StartZ=0 EndX=0 EndY=300 EndZ=0
    g3: LineSegment StartX=0 StartY=300 StartZ=0 EndX=0 EndY=0 EndZ=0
  constraints (11):
    c: Coincident(g0,g1)
    c: Coincident(g1,g2)
    c: Coincident(g2,g3)
    c: Coincident(g3,g0)
    c: Horizontal(g0)
    c: Horizontal(g2)
    c: Vertical(g1)
    c: Vertical(g3)
    c: Coincident(g0,g-1)
    c: DistanceX(g2,g2) = 150
    c: DistanceY(g1,g1) = 300
FEATURE [Part::Extrusion] Extrude073
  Base = -> Sketch014
  Dir = (0,-1,2e-16)
  DirMode = 2
  FaceMakerClass = Part::FaceMakerBullseye
  FaceMakerMode = 3
  LengthFwd = 6
  LengthRev = 0
  Solid = true
  Symmetric = true
FEATURE [Part::FeaturePython] AngleSteel020  label="AngleSteel022"  # WARN: FeaturePython — macro-defined, semantics opaque (R4)
  A = 75
  B = 75
  L = 300
  Placement = pos=(117.5,40.5,0) rot=(0,0,1;3.14159rad)
  Solid = true
  g0 = 7.85
  size = 10
  standard = SS_Equal
  t = 6
FEATURE [Part::Mirroring] Mirror004  label="AngleSteel003 (mirrored)"
  Base = (200,0,0)
  Normal = (0,1,0)
  Source = -> AngleSteel020
FEATURE [Part::Compound] Compound055  label="gusset001"
  Links = -> [Extrude073,Mirror004,AngleSteel020]
  Placement = pos=(7950,-1769.5,700) rot=(0,0,1;0rad)
  expr: .Placement.Base.x = Spreadsheet.D0 / 2 - 300
  expr: .Placement.Base.y = -<<Spreadsheet_feedWell>>.dia / 2 - 119.5
  expr: .Placement.Base.z = <<Spreadsheet_support>>.H0 - 150
FEATURE [Part::FeaturePython] Array  # Draft array (typed FeaturePython)
  AlwaysSyncPlacement = false
  Angle = 360
  ArrayType = 1
  Axis = (0,0,1)
  Base = -> Cut003
  Center = (0,0,0)
  Count = 4
  ExpandArray = false
  Fuse = false
  IntervalAxis = (0,0,0)
  IntervalX = (50,0,0)
  IntervalY = (0,50,0)
  IntervalZ = (0,0,50)
  NumberCircles = 3
  NumberPolar = 4
  NumberX = 2
  NumberY = 2
  NumberZ = 1
  PlacementList = 4 placements: [(350,0,998.5),(0,350,998.5),(-350,4.28626e-14,998.5),(-7.77156e-14,-350,998.5)]
  RadialDistance = 50
  ScaleList = (4) [(1,1,1),(1,1,1),(1,1,1),(1,1,1)]
  Symmetry = 1
  TangentialDistance = 25
  expr: .Placement.Rotation.Angle = <<Spreadsheet_feedWell>>.ba
FEATURE [App::Part] Part001  label="centerWell"
  Group = -> [Chamfer001,Sketch005,Sketch088,Sketch009,Sketch008,Compound002,Revolve,Revolve016,Revolve017,Extrude001,Extrude008,Extrude004,Extrude072,Extrude,Extrude002,Extrude007,Extrude009,Sketch001,Sketch087,Sketch,Sketch002,Sketch004,AngleSteel018,AngleSteel019,Cut003,Fusion,Cut001,Cut,Cut002,Array,Part]
  Origin = -> Origin001
  Placement = pos=(0,0,0) rot=(0,0,1;1.5708rad)
  mass = 951.819
FEATURE [Part::Mirroring] Mirror009  label="gusset001 (mirrored)"
  Base = (0,0,0)
  Normal = (1,0,0)
  Source = -> Compound055
FEATURE [Part::Mirroring] Mirror020  label="gusset001 (mirrored) (mirrored)"
  Base = (0,0,0)
  Normal = (0,1,0)
  Source = -> Mirror009
FEATURE [Part::Mirroring] Mirror021  label="gusset001 (mirrored)001"
  Base = (0,0,0)
  Normal = (0,1,0)
  Source = -> Compound055
FEATURE [Part::FeaturePython] ChannelSteel009  label="ChannelSteel"  # WARN: FeaturePython — macro-defined, semantics opaque (R4)
  B = 65
  H = 125
  L = 3520
  Placement = pos=(1820,-1750,0) rot=(-1,0,0;1.5708rad)
  Solid = true
  g0 = 7.85
  size = 2
  standard = SS
  t1 = 6
  t2 = 8
  expr: .Placement.Base.x = Spreadsheet.dia / 2 + 170
  expr: .Placement.Base.y = -<<Spreadsheet_feedWell>>.dia / 2 - 100
  expr: L = Spreadsheet.dia + 220
FEATURE [Sketcher::SketchObject] Sketch089
  ArcFitTolerance = 0
  FullyConstrained = false
  MakeInternals = false
  Placement = pos=(0,0,0) rot=(1,0,0;1.5708rad)
  expr: Constraints[2] = Spreadsheet012.Gb0
  expr: Constraints[5] = Spreadsheet012.rp0
  expr: Constraints[8] = Spreadsheet012.H0 - 60
  sketch-geometry (3):
    g0: LineSegment StartX=200 StartY=44.4 StartZ=0 EndX=850 EndY=834.4 EndZ=0
    g1: LineSegment StartX=850 StartY=834.4 StartZ=0 EndX=1500 EndY=44.4 EndZ=0
    g2: LineSegment [constr] StartX=850 StartY=834.4 StartZ=0 EndX=850 EndY=523.531 EndZ=0
  constraints (9):
    c: Coincident(g0,g1)
    c: Horizontal(g0,g1)
    c: DistanceX(g-1,g0) = 200
    c: Coincident(g2,g0)
    c: Symmetric(g1,g0,g2)
    c: DistanceX(g0,g1) = 1300
    c: DistanceY(g-1,g-4) = 14.4
    c: DistanceY(g-4,g0) = 30
    c: DistanceY(g0,g0) = 790
FEATURE [Sketcher::SketchObject] Sketch090
  ArcFitTolerance = 0
  ExternalGeometry = -> [Sketch089]
  FullyConstrained = true
  MakeInternals = false
  Placement = pos=(0,0,14.4) rot=(1,0,0;1.5708rad)
  expr: Constraints[23] = Spreadsheet012.Lb0
  expr: Constraints[24] = Spreadsheet012.H0 - 20
  expr: Constraints[25] = Spreadsheet012.Lb0 / 2
  sketch-geometry (9):
    g0: LineSegment StartX=200 StartY=91.4639 StartZ=0 EndX=776.404 EndY=840 EndZ=0
    g1: LineSegment StartX=808.333 StartY=758.536 StartZ=0 EndX=231.929 EndY=10 EndZ=0
    g2: LineSegment StartX=808.333 StartY=758.536 StartZ=0 EndX=1384.74 EndY=10 EndZ=0
    g3: LineSegment StartX=1416.67 StartY=91.4639 StartZ=0 EndX=840.262 EndY=840 EndZ=0
    g4: LineSegment StartX=776.404 StartY=840 StartZ=0 EndX=840.262 EndY=840 EndZ=0
    g5: LineSegment StartX=1384.74 StartY=10 StartZ=0 EndX=1416.67 EndY=10 EndZ=0
    g6: LineSegment StartX=1416.67 StartY=10 StartZ=0 EndX=1416.67 EndY=91.4639 EndZ=0
    g7: LineSegment StartX=231.929 StartY=10 StartZ=0 EndX=200 EndY=10 EndZ=0
    g8: LineSegment StartX=200 StartY=10 StartZ=0 EndX=200 EndY=91.4639 EndZ=0
  constraints (27):
    c: Coincident(g7,g8)
    c: Coincident(g0,g8)
    c: Coincident(g1,g7)
    c: Coincident(g0,g4)
    c: Coincident(g1,g2)
    c: Coincident(g3,g4)
    c: Coincident(g2,g5)
    c: Coincident(g5,g6)
    c: Coincident(g3,g6)
    c: Horizontal(g7)
    c: Horizontal(g4)
    c: Vertical(g8)
    c: Vertical(g7,g-4)
    c: Horizontal(g0,g3)
    c: Horizontal(g5)
    c: Horizontal(g1,g2)
    c: Vertical(g6)
    c: PointOnObject(g-3,g6)
    c: Parallel(g1,g-4)
    c: Parallel(g1,g0)
    c: Parallel(g2,g-3)
    c: Parallel(g-3,g3)
    c: Vertical(g1,g-4)
    c: Distance(g1,g0) = 75
    c: DistanceY(g2,g3) = 830
    c: Distance(g1,g-4) = 37.5
    c: DistanceY(g-5,g7) = 10
FEATURE [Part::Extrusion] Extrude074
  Base = -> Sketch090
  Dir = (0,-1,2e-16)
  DirMode = 2
  FaceMakerClass = Part::FaceMakerBullseye
  FaceMakerMode = 3
  LengthFwd = 6
  LengthRev = 0
  Placement = pos=(0,28.8,0) rot=(0,0,1;0rad)
  Solid = true
  Symmetric = false
FEATURE [Part::FeaturePython] Array033  # Draft array (typed FeaturePython)
  AlwaysSyncPlacement = false
  Angle = 360
  ArrayType = 0
  Axis = (0,0,1)
  Base = -> Extrude074
  Center = (0,0,0)
  Count = 12
  ExpandArray = false
  Fuse = false
  IntervalAxis = (0,0,0)
  IntervalX = (1300,0,0)
  IntervalY = (0,100,0)
  IntervalZ = (0,0,100)
  NumberCircles = 3
  NumberPolar = 5
  NumberX = 12
  NumberY = 1
  NumberZ = 1
  PlacementList = 12 placements: arithmetic series from (0,28.8,0) step (1300,0,0) to (14300,28.8,0)
  RadialDistance = 50
  ScaleList = (12) [(1,1,1),(1,1,1),(1,1,1),(1,1,1),(1,1,1),(1,1,1),(1,1,1),(1,1,1),(1,1,1),(1,1,1),(1,1,1),(1,1,1)]
  Symmetry = 1
  TangentialDistance = 25
  expr: .IntervalX.x = Spreadsheet012.rp0
  expr: NumberX = Spreadsheet012.rn0
FEATURE [Spreadsheet::Sheet] Spreadsheet012  label="Spreadsheet_support"
  cells = A2='梁成H0; B2(H0)=850; A3='梁長L0; B3(L0)=16000; A4='玄材shp; B4(shp)='90x90x7; A5='玄材ゲージラインGL0; B5(GL0)=40; A6='ラチス材Lshp; B6(Lshp)='6x75; A7='ラチス材幅Lb0; B7(Lb0)=75; A8='ラチス材厚Lt0; B8(Gt0)=6; A9='ガセットプレート幅Gb0; B9(Gb0)=200; A10='ラチスピッチrp0; B10(rp0)==(L0 - 2 * Gb0) / rn0; A11='ラチス配列数rn0; B11(rn0)=12; B16='t; C16='A; D16='GLine; A17='40x40x3; B17=3; C17=40; D17=22; A18='40x40x5; B18=5; C18=40; D18=22; A19='50x50x4; B19=4; C19=50; D19=30; A20='50x50x6; B20=6; C20=50; D20=30; A21='65x65x6; B21=6; C21=65; D21=35; A22='65x65x8; B22=8; C22=65; D22=35; A23='75x75x6; B23=6; C23=75; D23=40; A24='75x75x9; B24=9; C24=75; D24=40; A25='75x75x12; B25=12; C25=75; D25=40; A26='90x90x7; B26=7; C26=90; D26=50; A27='90x90x10; B27=10; C27=90; D27=50; A28='90x90x13; B28=13; C28=90; D28=50; A29='100x100x7; B29=7; C29=100; D29=55; A30='100x100x10; B30=10; C30=100; D30=55; A31='100x100x13; B31=13; C31=100; D31=55; A34='6x38; B34=6; C34=38; A35='9x38; B35=9; C35=38; A36='6x44; B36=6; C36=44; A37='9x44; B37=9; C37=44; A38='4.5x50; B38=4.5; C38=50; A39='6x50; B39=6; C39=50; A40='9x50; B40=9; C40=50; A41='6x65; B41=6; C41=65; A42='9x65; B42=9; C42=65; A43='6x75; B43=6; C43=75; A44='9x75; B44=9; C44=75; A45='6x90; B45=6; C45=90; A46='9x90; B46=9; C46=90
FEATURE [Sketcher::SketchObject] Sketch091
  ArcFitTolerance = 0
  FullyConstrained = true
  MakeInternals = false
  Placement = pos=(0,0,14.4) rot=(1,0,0;1.5708rad)
  expr: Constraints[21] = Spreadsheet012.L0
  expr: Constraints[22] = <<Spreadsheet_support>>.H0 - 20
  sketch-geometry (8):
    g0: LineSegment StartX=0 StartY=10 StartZ=0 EndX=200 EndY=10 EndZ=0
    g1: LineSegment StartX=200 StartY=10 StartZ=0 EndX=200 EndY=840 EndZ=0
    g2: LineSegment StartX=200 StartY=840 StartZ=0 EndX=0 EndY=840 EndZ=0
    g3: LineSegment StartX=0 StartY=840 StartZ=0 EndX=0 EndY=10 EndZ=0
    g4: LineSegment StartX=16000 StartY=840 StartZ=0 EndX=15800 EndY=840 EndZ=0
    g5: LineSegment StartX=15800 StartY=840 StartZ=0 EndX=15800 EndY=10 EndZ=0
    g6: LineSegment StartX=15800 StartY=10 StartZ=0 EndX=16000 EndY=10 EndZ=0
    g7: LineSegment StartX=16000 StartY=10 StartZ=0 EndX=16000 EndY=840 EndZ=0
  constraints (23):
    c: Coincident(g0,g1)
    c: Coincident(g1,g2)
    c: Coincident(g2,g3)
    c: Coincident(g3,g0)
    c: Horizontal(g0)
    c: Horizontal(g2)
    c: Vertical(g1)
    c: Vertical(g3)
    c: Vertical(g-1,g0)
    c: Coincident(g0,g-3)
    c: Coincident(g4,g5)
    c: Coincident(g5,g6)
    c: Coincident(g6,g7)
    c: Coincident(g7,g4)
    c: Horizontal(g4)
    c: Horizontal(g6)
    c: Vertical(g5)
    c: Vertical(g7)
    c: Equal(g0,g6)
    c: Horizontal(g6,g0)
    c: Horizontal(g1,g4)
    c: DistanceX(g0,g6) = 16000
    c: DistanceY(g1,g1) = 830
FEATURE [Part::Extrusion] Extrude075
  Base = -> Sketch091
  Dir = (0,-1,2e-16)
  DirMode = 2
  FaceMakerClass = Part::FaceMakerBullseye
  FaceMakerMode = 3
  LengthFwd = 6
  LengthRev = 0
  Placement = pos=(0,28.8,0) rot=(0,0,1;0rad)
  Solid = true
  Symmetric = false
  expr: LengthFwd = Spreadsheet012.Gt0
FEATURE [Part::FeaturePython] AngleSteel021  label="AngleSteel004"  # WARN: FeaturePython — macro-defined, semantics opaque (R4)
  A = 90
  B = 90
  L = 1000
  Placement = pos=(0,28.8,14.4) rot=(0,0,1;1.5708rad)
  Solid = false
  g0 = 7.85
  mass = 0
  size = 13
  standard = SS_Equal
  t = 8
FEATURE [Part::Mirroring] Mirror022  label="AngleSteel (mirrored)"
  Base = (-2.54e-14,114.396,14.3963)
  Normal = (0,0,-1)
  Placement = pos=(0,0,850) rot=(0,0,1;0rad)
  Source = -> AngleSteel021
  expr: .Placement.Base.z = Spreadsheet012.H0
FEATURE [Part::Extrusion] Extrude076
  Base = -> AngleSteel021
  Dir = (-1,-2e-16,0)
  DirMode = 2
  FaceMakerClass = Part::FaceMakerBullseye
  FaceMakerMode = 3
  LengthFwd = 16000
  LengthRev = 0
  Reversed = true
  Solid = false
  Symmetric = false
  expr: LengthFwd = Spreadsheet012.L0
FEATURE [Part::Extrusion] Extrude077
  Base = -> Mirror022
  Dir = (-1,-2e-16,0)
  DirMode = 2
  FaceMakerClass = Part::FaceMakerBullseye
  FaceMakerMode = 3
  LengthFwd = 16000
  LengthRev = 0
  Reversed = true
  Solid = false
  Symmetric = false
  expr: LengthFwd = Spreadsheet012.L0
FEATURE [Part::MultiFuse] Fusion001
  Shapes = -> [Extrude077,Extrude076]
FEATURE [Part::Mirroring] Mirror001  label="Fusion (mirrored)001"
  Base = (-3.2e-15,28.7963,514.396)
  Normal = (0,-1,0)
  Placement = pos=(0,-6,0) rot=(0,0,1;0rad)
  Source = -> Fusion001
  expr: .Placement.Base.y = -Spreadsheet012.Gt0
FEATURE [Part::Compound] Compound
  Links = -> [Mirror001,Fusion001]
FEATURE [App::Part] Part005  label="latticeBeam"
  Group = -> [Sketch089,Sketch091,Sketch090,Fusion001,Mirror022,Mirror001,Extrude074,Extrude075,Extrude077,Extrude076,Array033,AngleSteel021,Compound]
  Origin = -> Origin005
  Placement = pos=(-8000,1750,384) rot=(0,0,1;0rad)
  expr: .Placement.Base.x = -<<Spreadsheet_support>>.L0 / 2
  expr: .Placement.Base.y = <<Spreadsheet_feedWell>>.dia / 2 + 100
  expr: .Placement.Base.z = 534 - (<<Spreadsheet_support>>.H0 - 700)
FEATURE [Part::Mirroring] Mirror023  label="latticeBeam (mirrored)"
  Base = (150,0,334)
  Normal = (0,-1,0)
  Source = -> Part005
FEATURE [Part::FeaturePython] Array034  # Draft array (typed FeaturePython)
  AlwaysSyncPlacement = false
  Angle = 360
  ArrayType = 0
  Axis = (0,0,1)
  Base = -> ChannelSteel009
  Center = (0,0,0)
  Count = 3
  ExpandArray = false
  Fuse = false
  IntervalAxis = (0,0,0)
  IntervalX = (2000,0,0)
  IntervalY = (0,100,0)
  IntervalZ = (0,0,100)
  NumberCircles = 3
  NumberPolar = 5
  NumberX = 3
  NumberY = 1
  NumberZ = 1
  Placement = pos=(0,0,1186) rot=(0,0,1;0rad)
  PlacementList = 3 placements: arithmetic series from (1820,-1750,0) step (2000,0,0) to (5820,-1750,0)
  RadialDistance = 50
  ScaleList = (3) [(1,1,1),(1,1,1),(1,1,1)]
  Symmetry = 1
  TangentialDistance = 25
FEATURE [Part::Mirroring] Mirror013  label="Array002 (mirrored)"
  Base = (0,0,0)
  Normal = (1,0,0)
  Source = -> Array034
FEATURE [App::Part] Part002  label="centerWellSupport"
  Group = -> [Extrude073,Mirror004,Sketch014,Mirror009,Mirror020,Compound055,AngleSteel020,Mirror021,ChannelSteel009,Part005,Mirror023,Array034,Mirror013]
  Origin = -> Origin002
  Placement = pos=(0,0,-250) rot=(0,0,1;0rad)
  mass = 852.489
  expr: .Placement.Base.z = <<Spreadsheet_feedWell>>.h1 - 1250
FEATURE [App::Part] Part004  label="feedWell"
  Group = -> [Part002,Part001,Spreadsheet,Spreadsheet012]
  Origin = -> Origin004
  Placement = pos=(0,0,3204) rot=(0,0,1;0rad)
FEATURE [Part::FeaturePython] Array035  # Draft array (typed FeaturePython)
  AlwaysSyncPlacement = false
  Angle = 360
  ArrayType = 1
  Axis = (0,0,1)
  Base = -> Part059
  Center = (0,0,0)
  Count = 2
  ExpandArray = false
  Fuse = false
  IntervalAxis = (0,0,0)
  IntervalX = (50,0,0)
  IntervalY = (0,50,0)
  IntervalZ = (0,0,50)
  NumberCircles = 3
  NumberPolar = 2
  NumberX = 2
  NumberY = 2
  NumberZ = 1
  PlacementList = 2 placements: [(1059.84,-2.274e-13,945.714),(-1059.84,3.57193e-13,945.714)]
  RadialDistance = 50
  ScaleList = (2) [(1,1,1),(1,1,1)]
  Symmetry = 1
  TangentialDistance = 25
FEATURE [App::Part] Part055  label="movingParts"
  Group = -> [Part041,Part047,Part059,Array035]
  Origin = -> Origin082
FEATURE [PartDesign::Body] Body
  AllowCompound = false
  Origin = -> Origin090
FEATURE [Sketcher::SketchObject] Sketch092
  ArcFitTolerance = 1e-06
  AttachmentSupport = -> [XY_Plane090]
  FullyConstrained = true
  MakeInternals = false
  MapMode = 5
  sketch-geometry (5):
    g0: LineSegment StartX=-525 StartY=-525 StartZ=0 EndX=525 EndY=-525 EndZ=0
    g1: LineSegment StartX=525 StartY=-525 StartZ=0 EndX=525 EndY=525 EndZ=0
    g2: LineSegment StartX=525 StartY=525 StartZ=0 EndX=-525 EndY=525 EndZ=0
    g3: LineSegment StartX=-525 StartY=525 StartZ=0 EndX=-525 EndY=-525 EndZ=0
    g4: GeomPoint [constr] X=0 Y=0 Z=0
  constraints (12):
    c: Coincident(g0,g1)
    c: Coincident(g1,g2)
    c: Coincident(g2,g3)
    c: Coincident(g3,g0)
    c: Horizontal(g0)
    c: Horizontal(g2)
    c: Vertical(g1)
    c: Vertical(g3)
    c: Symmetric(g2,g0,g4)
    c: Coincident(g4,g-1)
    c: DistanceX(g2,g2) = 1050
    c: DistanceY(g1,g1) = 1050
FEATURE [PartDesign::Pad] Pad002
  Direction = (0,0,1)
  Length = 750
  Length2 = 10
  Profile = -> Sketch092
  ReferenceAxis = -> Sketch092 [N_Axis]
  Refine = true
  Suppressed = false
  Type = 0
FEATURE [PartDesign::Chamfer] Chamfer002
  Angle = 45
  Base = -> Pad002 [Edge4,Edge10]
  BaseFeature = -> Pad002
  ChamferType = 0
  FlipDirection = false
  Refine = true
  Size = 200
  Size2 = 1
  SupportTransform = false
  Suppressed = false
  UseAllEdges = false
FEATURE [Part::FeaturePython] AngleSteel022  label="AngleSteel023"  # WARN: FeaturePython — macro-defined, semantics opaque (R4)
  A = 50
  B = 50
  L = 5500
  Placement = pos=(525,0,0) rot=(0,0,1;0rad)
  Solid = false
  g0 = 7.85
  mass = 0
  size = 7
  standard = SS_Equal
  t = 6
  type = 00_Angle
FEATURE [Part::Sweep] Sweep010
  Frenet = true
  Sections = -> [AngleSteel022]
  Solid = true
  Spine = -> Chamfer002 [Edge12,Edge13,Edge7,Edge3]
  Transition = 1
FEATURE [Part::Thickness] Thickness
  Faces = -> Chamfer002 [Face4]
  Intersection = false
  Join = 1
  Mode = 0
  SelfIntersection = false
  Value = 3
FEATURE [App::Part] Part062  label="driveUnitCover"
  Group = -> [Body,Thickness,Chamfer002,Pad002,Sketch092,AngleSteel022,Sweep010]
  Origin = -> Origin091
  Placement = pos=(0,0,5901.7) rot=(0,0,1;0rad)
  mass = 112.037
FEATURE [App::Part] Part036  label="pillar_thickner_16.5m"
  Group = -> [Part037,Part038,Part039,Part043,Part__Feature027,Single_flange_straight_pipe,Part051,Part055,Spreadsheet011,Assembly,Part061,Part004,Sketch015,Array006,Revolve006,Cut007,Sketch020,Revolve010,Part062]
  Origin = -> Origin059
  Placement = pos=(-1.99e-13,0,-5555.9) rot=(0,0,1;0rad)
FEATURE [Spreadsheet::Sheet] Parts_List
  cells = A1='No; B1='Name; C1='Standard; D1='Count; E1='Unit[kg]; F1='Mass[kg]; A2=1; B2='sludgePipe; D2=1; E2=244.94; F2=244.94; A3=2; B3='buffle; D3=1; E3=804.44; F3=804.44; A4=3; B4='centerPost001; D4=1; E4=1462.82; F4=1462.82; A5=4; B5='covering; D5=1; E5=1420.74; F5=1420.74; A6=5; B6='centerCage; D6=1; E6=1513.41; F6=1513.41; A7=6; B7='bridge; D7=1; E7=2505.75; F7=2505.75; A8=7; B8='driveUnit; D8=1; E8=829.84; F8=829.84; A9=8; B9='skimmerBrade001; D9=1; E9=104.21; F9=104.21; A10=9; B10='pipeSkimmerBrg; D10=1; E10=86.99; F10=86.99; A11=10; B11='pipeSkimmerBody; D11=1; E11=288.08; F11=288.08; A12=11; B12='pipeSkimmerControlDevice; D12=1; E12=120; F12=120; A13=12; B13='rakeAssy; D13=2; E13=619.96; F13=1239.91; A14=13; B14='inflow; D14=1; E14=1694.36; F14=1694.36; A15=14; B15='centerWell; D15=1; E15=951.82; F15=951.82; A16=15; B16='centerWellSupport; D16=1; E16=852.49; F16=852.49; A17=16; B17='driveUnitCover; D17=1; E17=112.04; F17=112.04; F18=14231.84
